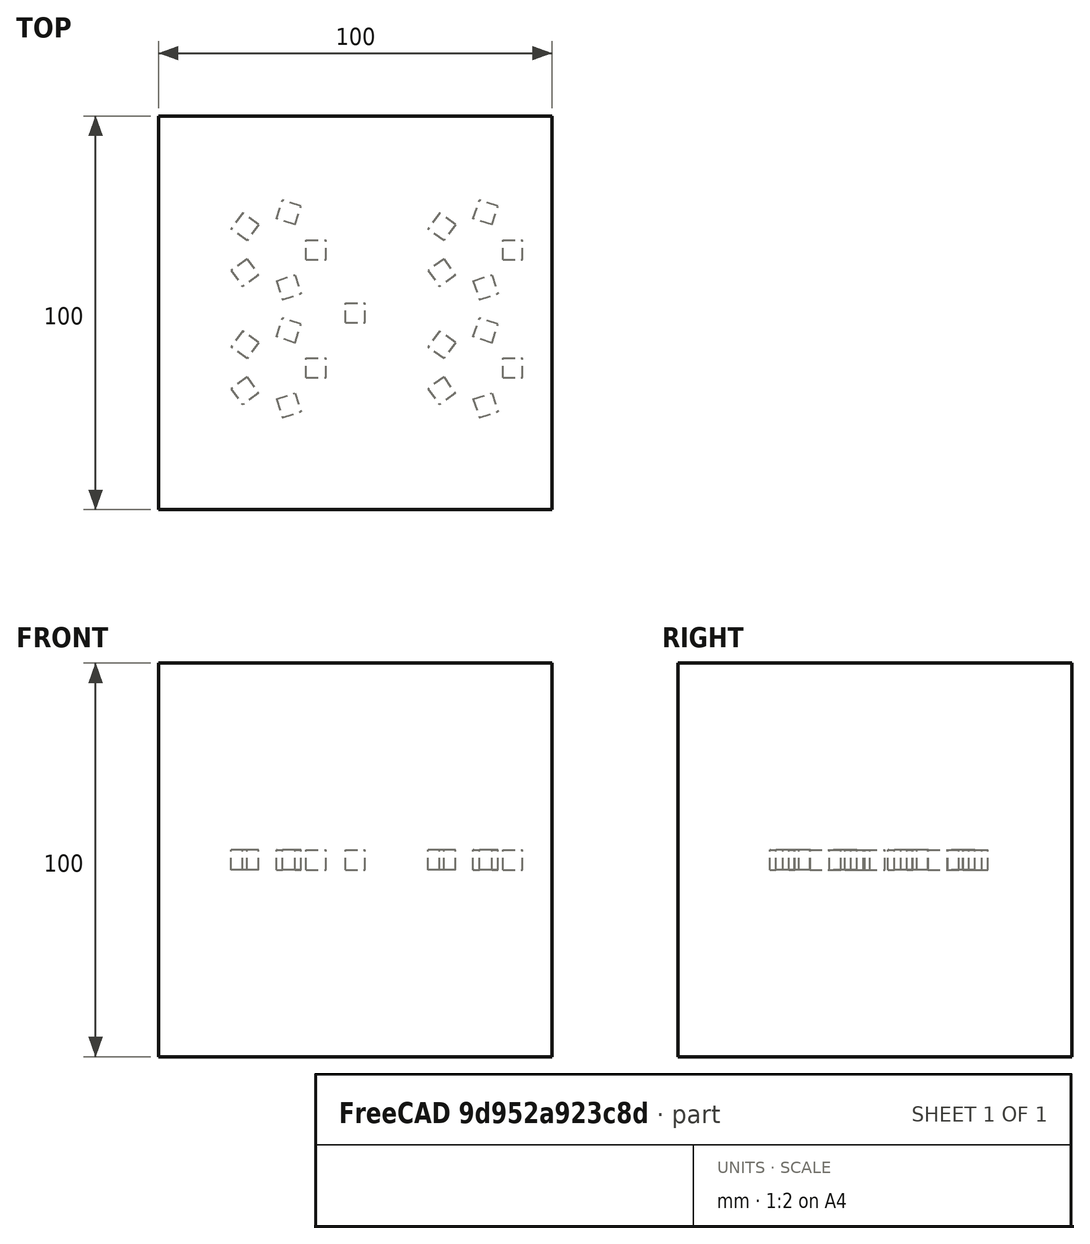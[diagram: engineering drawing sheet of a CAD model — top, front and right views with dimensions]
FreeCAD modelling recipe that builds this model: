
FCSTD DOCUMENT  (FreeCAD 0.19RUnknown)
Label: arrayTest-1
License: All rights reserved
LicenseURL: http://en.wikipedia.org/wiki/All_rights_reserved
objects: App::DocumentObjectGroupPython×1248, Part::FeaturePython×4, App::Part×3
note: 4 computed .brp shape members not serialized (recipe doc carries the construction recipe); baked Part::Feature solids carry a one-line shape summary decoded from their .brp

FEATURE [App::DocumentObjectGroupPython] HALFPI  # scripted group (container) (typed FeaturePython)
  name = HALFPI
  value = pi/2.
FEATURE [App::DocumentObjectGroupPython] PI  # scripted group (container) (typed FeaturePython)
  name = PI
  value = 1.*pi
FEATURE [App::DocumentObjectGroupPython] TWOPI  # scripted group (container) (typed FeaturePython)
  name = TWOPI
  value = 2.*pi
FEATURE [App::DocumentObjectGroupPython] Constants  # scripted group (container) (typed FeaturePython)
  Group = -> [HALFPI,PI,TWOPI]
FEATURE [App::DocumentObjectGroupPython] Variables  # scripted group (container) (typed FeaturePython)
FEATURE [App::DocumentObjectGroupPython] Quantities  # scripted group (container) (typed FeaturePython)
FEATURE [App::DocumentObjectGroupPython] Isotopes  # scripted group (container) (typed FeaturePython)
FEATURE [App::DocumentObjectGroupPython] Elements  # scripted group (container) (typed FeaturePython)
FEATURE [App::DocumentObjectGroupPython] G4Isotopes  # scripted group (container) (typed FeaturePython)
FEATURE [App::DocumentObjectGroupPython] H_element  # scripted group (container) (typed FeaturePython)
  Z = 1
  atom_value = 1.008
  formula = H
  name = H_element
FEATURE [App::DocumentObjectGroupPython] He_element  # scripted group (container) (typed FeaturePython)
  Z = 2
  atom_value = 4.0026
  formula = He
  name = He_element
FEATURE [App::DocumentObjectGroupPython] Li_element  # scripted group (container) (typed FeaturePython)
  Z = 3
  atom_value = 6.94
  formula = Li
  name = Li_element
FEATURE [App::DocumentObjectGroupPython] Be_element  # scripted group (container) (typed FeaturePython)
  Z = 4
  atom_value = 9.01218
  formula = Be
  name = Be_element
FEATURE [App::DocumentObjectGroupPython] B_element  # scripted group (container) (typed FeaturePython)
  Z = 5
  atom_value = 10.81
  formula = B
  name = B_element
FEATURE [App::DocumentObjectGroupPython] C_element  # scripted group (container) (typed FeaturePython)
  Z = 6
  atom_value = 12.011
  formula = C
  name = C_element
FEATURE [App::DocumentObjectGroupPython] N_element  # scripted group (container) (typed FeaturePython)
  Z = 7
  atom_value = 14.007
  formula = N
  name = N_element
FEATURE [App::DocumentObjectGroupPython] O_element  # scripted group (container) (typed FeaturePython)
  Z = 8
  atom_value = 15.999
  formula = O
  name = O_element
FEATURE [App::DocumentObjectGroupPython] F_element  # scripted group (container) (typed FeaturePython)
  Z = 9
  atom_value = 18.9984
  formula = F
  name = F_element
FEATURE [App::DocumentObjectGroupPython] Ne_element  # scripted group (container) (typed FeaturePython)
  Z = 10
  atom_value = 20.1797
  formula = Ne
  name = Ne_element
FEATURE [App::DocumentObjectGroupPython] Na_element  # scripted group (container) (typed FeaturePython)
  Z = 11
  atom_value = 22.9898
  formula = Na
  name = Na_element
FEATURE [App::DocumentObjectGroupPython] Mg_element  # scripted group (container) (typed FeaturePython)
  Z = 12
  atom_value = 24.305
  formula = Mg
  name = Mg_element
FEATURE [App::DocumentObjectGroupPython] Al_element  # scripted group (container) (typed FeaturePython)
  Z = 13
  atom_value = 26.9815
  formula = Al
  name = Al_element
FEATURE [App::DocumentObjectGroupPython] Si_element  # scripted group (container) (typed FeaturePython)
  Z = 14
  atom_value = 28.085
  formula = Si
  name = Si_element
FEATURE [App::DocumentObjectGroupPython] P_element  # scripted group (container) (typed FeaturePython)
  Z = 15
  atom_value = 30.9738
  formula = P
  name = P_element
FEATURE [App::DocumentObjectGroupPython] S_element  # scripted group (container) (typed FeaturePython)
  Z = 16
  atom_value = 32.06
  formula = S
  name = S_element
FEATURE [App::DocumentObjectGroupPython] Cl_element  # scripted group (container) (typed FeaturePython)
  Z = 17
  atom_value = 35.45
  formula = Cl
  name = Cl_element
FEATURE [App::DocumentObjectGroupPython] Ar_element  # scripted group (container) (typed FeaturePython)
  Z = 18
  atom_value = 39.95
  formula = Ar
  name = Ar_element
FEATURE [App::DocumentObjectGroupPython] K_element  # scripted group (container) (typed FeaturePython)
  Z = 19
  atom_value = 39.0983
  formula = K
  name = K_element
FEATURE [App::DocumentObjectGroupPython] Ca_element  # scripted group (container) (typed FeaturePython)
  Z = 20
  atom_value = 40.078
  formula = Ca
  name = Ca_element
FEATURE [App::DocumentObjectGroupPython] Sc_element  # scripted group (container) (typed FeaturePython)
  Z = 21
  atom_value = 44.9559
  formula = Sc
  name = Sc_element
FEATURE [App::DocumentObjectGroupPython] Ti_element  # scripted group (container) (typed FeaturePython)
  Z = 22
  atom_value = 47.867
  formula = Ti
  name = Ti_element
FEATURE [App::DocumentObjectGroupPython] V_element  # scripted group (container) (typed FeaturePython)
  Z = 23
  atom_value = 50.9415
  formula = V
  name = V_element
FEATURE [App::DocumentObjectGroupPython] Cr_element  # scripted group (container) (typed FeaturePython)
  Z = 24
  atom_value = 51.9961
  formula = Cr
  name = Cr_element
FEATURE [App::DocumentObjectGroupPython] Mn_element  # scripted group (container) (typed FeaturePython)
  Z = 25
  atom_value = 54.938
  formula = Mn
  name = Mn_element
FEATURE [App::DocumentObjectGroupPython] Fe_element  # scripted group (container) (typed FeaturePython)
  Z = 26
  atom_value = 55.845
  formula = Fe
  name = Fe_element
FEATURE [App::DocumentObjectGroupPython] Co_element  # scripted group (container) (typed FeaturePython)
  Z = 27
  atom_value = 58.9332
  formula = Co
  name = Co_element
FEATURE [App::DocumentObjectGroupPython] Ni_element  # scripted group (container) (typed FeaturePython)
  Z = 28
  atom_value = 58.6934
  formula = Ni
  name = Ni_element
FEATURE [App::DocumentObjectGroupPython] Cu_element  # scripted group (container) (typed FeaturePython)
  Z = 29
  atom_value = 63.546
  formula = Cu
  name = Cu_element
FEATURE [App::DocumentObjectGroupPython] Zn_element  # scripted group (container) (typed FeaturePython)
  Z = 30
  atom_value = 65.38
  formula = Zn
  name = Zn_element
FEATURE [App::DocumentObjectGroupPython] Ga_element  # scripted group (container) (typed FeaturePython)
  Z = 31
  atom_value = 69.723
  formula = Ga
  name = Ga_element
FEATURE [App::DocumentObjectGroupPython] Ge_element  # scripted group (container) (typed FeaturePython)
  Z = 32
  atom_value = 72.63
  formula = Ge
  name = Ge_element
FEATURE [App::DocumentObjectGroupPython] As_element  # scripted group (container) (typed FeaturePython)
  Z = 33
  atom_value = 74.9216
  formula = As
  name = As_element
FEATURE [App::DocumentObjectGroupPython] Se_element  # scripted group (container) (typed FeaturePython)
  Z = 34
  atom_value = 78.971
  formula = Se
  name = Se_element
FEATURE [App::DocumentObjectGroupPython] Br_element  # scripted group (container) (typed FeaturePython)
  Z = 35
  atom_value = 79.904
  formula = Br
  name = Br_element
FEATURE [App::DocumentObjectGroupPython] Kr_element  # scripted group (container) (typed FeaturePython)
  Z = 36
  atom_value = 83.798
  formula = Kr
  name = Kr_element
FEATURE [App::DocumentObjectGroupPython] Rb_element  # scripted group (container) (typed FeaturePython)
  Z = 37
  atom_value = 85.4678
  formula = Rb
  name = Rb_element
FEATURE [App::DocumentObjectGroupPython] Sr_element  # scripted group (container) (typed FeaturePython)
  Z = 38
  atom_value = 87.62
  formula = Sr
  name = Sr_element
FEATURE [App::DocumentObjectGroupPython] Y_element  # scripted group (container) (typed FeaturePython)
  Z = 39
  atom_value = 88.9058
  formula = Y
  name = Y_element
FEATURE [App::DocumentObjectGroupPython] Zr_element  # scripted group (container) (typed FeaturePython)
  Z = 40
  atom_value = 91.224
  formula = Zr
  name = Zr_element
FEATURE [App::DocumentObjectGroupPython] Nb_element  # scripted group (container) (typed FeaturePython)
  Z = 41
  atom_value = 92.9064
  formula = Nb
  name = Nb_element
FEATURE [App::DocumentObjectGroupPython] Mo_element  # scripted group (container) (typed FeaturePython)
  Z = 42
  atom_value = 95.95
  formula = Mo
  name = Mo_element
FEATURE [App::DocumentObjectGroupPython] Tc_element  # scripted group (container) (typed FeaturePython)
  Z = 43
  atom_value = 97
  formula = Tc
  name = Tc_element
FEATURE [App::DocumentObjectGroupPython] Ru_element  # scripted group (container) (typed FeaturePython)
  Z = 44
  atom_value = 101.07
  formula = Ru
  name = Ru_element
FEATURE [App::DocumentObjectGroupPython] Rh_element  # scripted group (container) (typed FeaturePython)
  Z = 45
  atom_value = 102.905
  formula = Rh
  name = Rh_element
FEATURE [App::DocumentObjectGroupPython] Pd_element  # scripted group (container) (typed FeaturePython)
  Z = 46
  atom_value = 106.42
  formula = Pd
  name = Pd_element
FEATURE [App::DocumentObjectGroupPython] Ag_element  # scripted group (container) (typed FeaturePython)
  Z = 47
  atom_value = 107.868
  formula = Ag
  name = Ag_element
FEATURE [App::DocumentObjectGroupPython] Cd_element  # scripted group (container) (typed FeaturePython)
  Z = 48
  atom_value = 112.414
  formula = Cd
  name = Cd_element
FEATURE [App::DocumentObjectGroupPython] In_element  # scripted group (container) (typed FeaturePython)
  Z = 49
  atom_value = 114.818
  formula = In
  name = In_element
FEATURE [App::DocumentObjectGroupPython] Sn_element  # scripted group (container) (typed FeaturePython)
  Z = 50
  atom_value = 118.71
  formula = Sn
  name = Sn_element
FEATURE [App::DocumentObjectGroupPython] Sb_element  # scripted group (container) (typed FeaturePython)
  Z = 51
  atom_value = 121.76
  formula = Sb
  name = Sb_element
FEATURE [App::DocumentObjectGroupPython] Te_element  # scripted group (container) (typed FeaturePython)
  Z = 52
  atom_value = 127.6
  formula = Te
  name = Te_element
FEATURE [App::DocumentObjectGroupPython] I_element  # scripted group (container) (typed FeaturePython)
  Z = 53
  atom_value = 126.904
  formula = I
  name = I_element
FEATURE [App::DocumentObjectGroupPython] Xe_element  # scripted group (container) (typed FeaturePython)
  Z = 54
  atom_value = 131.293
  formula = Xe
  name = Xe_element
FEATURE [App::DocumentObjectGroupPython] Cs_element  # scripted group (container) (typed FeaturePython)
  Z = 55
  atom_value = 132.905
  formula = Cs
  name = Cs_element
FEATURE [App::DocumentObjectGroupPython] Ba_element  # scripted group (container) (typed FeaturePython)
  Z = 56
  atom_value = 137.327
  formula = Ba
  name = Ba_element
FEATURE [App::DocumentObjectGroupPython] La_element  # scripted group (container) (typed FeaturePython)
  Z = 57
  atom_value = 138.905
  formula = La
  name = La_element
FEATURE [App::DocumentObjectGroupPython] Ce_element  # scripted group (container) (typed FeaturePython)
  Z = 58
  atom_value = 140.116
  formula = Ce
  name = Ce_element
FEATURE [App::DocumentObjectGroupPython] Pr_element  # scripted group (container) (typed FeaturePython)
  Z = 59
  atom_value = 140.908
  formula = Pr
  name = Pr_element
FEATURE [App::DocumentObjectGroupPython] Nd_element  # scripted group (container) (typed FeaturePython)
  Z = 60
  atom_value = 144.242
  formula = Nd
  name = Nd_element
FEATURE [App::DocumentObjectGroupPython] Pm_element  # scripted group (container) (typed FeaturePython)
  Z = 61
  atom_value = 145
  formula = Pm
  name = Pm_element
FEATURE [App::DocumentObjectGroupPython] Sm_element  # scripted group (container) (typed FeaturePython)
  Z = 62
  atom_value = 150.36
  formula = Sm
  name = Sm_element
FEATURE [App::DocumentObjectGroupPython] Eu_element  # scripted group (container) (typed FeaturePython)
  Z = 63
  atom_value = 151.964
  formula = Eu
  name = Eu_element
FEATURE [App::DocumentObjectGroupPython] Gd_element  # scripted group (container) (typed FeaturePython)
  Z = 64
  atom_value = 157.25
  formula = Gd
  name = Gd_element
FEATURE [App::DocumentObjectGroupPython] Tb_element  # scripted group (container) (typed FeaturePython)
  Z = 65
  atom_value = 158.925
  formula = Tb
  name = Tb_element
FEATURE [App::DocumentObjectGroupPython] Dy_element  # scripted group (container) (typed FeaturePython)
  Z = 66
  atom_value = 162.5
  formula = Dy
  name = Dy_element
FEATURE [App::DocumentObjectGroupPython] Ho_element  # scripted group (container) (typed FeaturePython)
  Z = 67
  atom_value = 164.93
  formula = Ho
  name = Ho_element
FEATURE [App::DocumentObjectGroupPython] Er_element  # scripted group (container) (typed FeaturePython)
  Z = 68
  atom_value = 167.259
  formula = Er
  name = Er_element
FEATURE [App::DocumentObjectGroupPython] Tm_element  # scripted group (container) (typed FeaturePython)
  Z = 69
  atom_value = 168.934
  formula = Tm
  name = Tm_element
FEATURE [App::DocumentObjectGroupPython] Yb_element  # scripted group (container) (typed FeaturePython)
  Z = 70
  atom_value = 173.045
  formula = Yb
  name = Yb_element
FEATURE [App::DocumentObjectGroupPython] Lu_element  # scripted group (container) (typed FeaturePython)
  Z = 71
  atom_value = 174.967
  formula = Lu
  name = Lu_element
FEATURE [App::DocumentObjectGroupPython] Hf_element  # scripted group (container) (typed FeaturePython)
  Z = 72
  atom_value = 178.49
  formula = Hf
  name = Hf_element
FEATURE [App::DocumentObjectGroupPython] Ta_element  # scripted group (container) (typed FeaturePython)
  Z = 73
  atom_value = 180.948
  formula = Ta
  name = Ta_element
FEATURE [App::DocumentObjectGroupPython] W_element  # scripted group (container) (typed FeaturePython)
  Z = 74
  atom_value = 183.84
  formula = W
  name = W_element
FEATURE [App::DocumentObjectGroupPython] Re_element  # scripted group (container) (typed FeaturePython)
  Z = 75
  atom_value = 186.207
  formula = Re
  name = Re_element
FEATURE [App::DocumentObjectGroupPython] Os_element  # scripted group (container) (typed FeaturePython)
  Z = 76
  atom_value = 190.23
  formula = Os
  name = Os_element
FEATURE [App::DocumentObjectGroupPython] Ir_element  # scripted group (container) (typed FeaturePython)
  Z = 77
  atom_value = 192.217
  formula = Ir
  name = Ir_element
FEATURE [App::DocumentObjectGroupPython] Pt_element  # scripted group (container) (typed FeaturePython)
  Z = 78
  atom_value = 195.084
  formula = Pt
  name = Pt_element
FEATURE [App::DocumentObjectGroupPython] Au_element  # scripted group (container) (typed FeaturePython)
  Z = 79
  atom_value = 196.967
  formula = Au
  name = Au_element
FEATURE [App::DocumentObjectGroupPython] Hg_element  # scripted group (container) (typed FeaturePython)
  Z = 80
  atom_value = 200.592
  formula = Hg
  name = Hg_element
FEATURE [App::DocumentObjectGroupPython] Tl_element  # scripted group (container) (typed FeaturePython)
  Z = 81
  atom_value = 204.38
  formula = Tl
  name = Tl_element
FEATURE [App::DocumentObjectGroupPython] Pb_element  # scripted group (container) (typed FeaturePython)
  Z = 82
  atom_value = 207.2
  formula = Pb
  name = Pb_element
FEATURE [App::DocumentObjectGroupPython] Bi_element  # scripted group (container) (typed FeaturePython)
  Z = 83
  atom_value = 208.98
  formula = Bi
  name = Bi_element
FEATURE [App::DocumentObjectGroupPython] Po_element  # scripted group (container) (typed FeaturePython)
  Z = 84
  atom_value = 209
  formula = Po
  name = Po_element
FEATURE [App::DocumentObjectGroupPython] At_element  # scripted group (container) (typed FeaturePython)
  Z = 85
  atom_value = 210
  formula = At
  name = At_element
FEATURE [App::DocumentObjectGroupPython] Rn_element  # scripted group (container) (typed FeaturePython)
  Z = 86
  atom_value = 222
  formula = Rn
  name = Rn_element
FEATURE [App::DocumentObjectGroupPython] Fr_element  # scripted group (container) (typed FeaturePython)
  Z = 87
  atom_value = 223
  formula = Fr
  name = Fr_element
FEATURE [App::DocumentObjectGroupPython] Ra_element  # scripted group (container) (typed FeaturePython)
  Z = 88
  atom_value = 226
  formula = Ra
  name = Ra_element
FEATURE [App::DocumentObjectGroupPython] Ac_element  # scripted group (container) (typed FeaturePython)
  Z = 89
  atom_value = 227
  formula = Ac
  name = Ac_element
FEATURE [App::DocumentObjectGroupPython] Th_element  # scripted group (container) (typed FeaturePython)
  Z = 90
  atom_value = 232.038
  formula = Th
  name = Th_element
FEATURE [App::DocumentObjectGroupPython] Pa_element  # scripted group (container) (typed FeaturePython)
  Z = 91
  atom_value = 231.036
  formula = Pa
  name = Pa_element
FEATURE [App::DocumentObjectGroupPython] U_element  # scripted group (container) (typed FeaturePython)
  Z = 92
  atom_value = 238.029
  formula = U
  name = U_element
FEATURE [App::DocumentObjectGroupPython] Np_element  # scripted group (container) (typed FeaturePython)
  Z = 93
  atom_value = 237
  formula = Np
  name = Np_element
FEATURE [App::DocumentObjectGroupPython] Pu_element  # scripted group (container) (typed FeaturePython)
  Z = 94
  atom_value = 244
  formula = Pu
  name = Pu_element
FEATURE [App::DocumentObjectGroupPython] Am_element  # scripted group (container) (typed FeaturePython)
  Z = 95
  atom_value = 243
  formula = Am
  name = Am_element
FEATURE [App::DocumentObjectGroupPython] Cm_element  # scripted group (container) (typed FeaturePython)
  Z = 96
  atom_value = 247
  formula = Cm
  name = Cm_element
FEATURE [App::DocumentObjectGroupPython] Bk_element  # scripted group (container) (typed FeaturePython)
  Z = 97
  atom_value = 247
  formula = Bk
  name = Bk_element
FEATURE [App::DocumentObjectGroupPython] Cf_element  # scripted group (container) (typed FeaturePython)
  Z = 98
  atom_value = 251
  formula = Cf
  name = Cf_element
FEATURE [App::DocumentObjectGroupPython] G4Elements  # scripted group (container) (typed FeaturePython)
  Group = -> [H_element,He_element,Li_element,Be_element,B_element,C_element,N_element,O_element,F_element,Ne_element,Na_element,Mg_element,Al_element,Si_element,P_element,S_element,Cl_element,Ar_element,K_element,Ca_element,Sc_element,Ti_element,V_element,Cr_element,Mn_element,Fe_element,Co_element,Ni_element,Cu_element,Zn_element,Ga_element,Ge_element,As_element,Se_element,Br_element,Kr_element,Rb_element,+61 more]
FEATURE [App::DocumentObjectGroupPython] H_element001  label="H_element : 0.101"  # scripted group (container) (typed FeaturePython)
  n = 0.101327
FEATURE [App::DocumentObjectGroupPython] C_element001  label="C_element : 0.775"  # scripted group (container) (typed FeaturePython)
  n = 0.7755
FEATURE [App::DocumentObjectGroupPython] N_element001  label="N_element : 0.035"  # scripted group (container) (typed FeaturePython)
  n = 0.035057
FEATURE [App::DocumentObjectGroupPython] O_element001  label="O_element : 0.052"  # scripted group (container) (typed FeaturePython)
  n = 0.0523159
FEATURE [App::DocumentObjectGroupPython] F_element001  label="F_element : 0.017"  # scripted group (container) (typed FeaturePython)
  n = 0.017422
FEATURE [App::DocumentObjectGroupPython] Ca_element001  label="Ca_element : 0.018"  # scripted group (container) (typed FeaturePython)
  n = 0.018378
FEATURE [App::DocumentObjectGroupPython] G4_A_150_TISSUE  label="G4_A-150_TISSUE"  # scripted group (container) (typed FeaturePython)
  Dunit = g/cm3
  Dvalue = 1.127
  Group = -> [H_element001,C_element001,N_element001,O_element001,F_element001,Ca_element001]
  conduct = 2
  density = 1
  expand = 3
  formula = G4_A-150_TISSUE
  name = G4_A-150_TISSUE
  specific = 4
FEATURE [App::DocumentObjectGroupPython] C_element002  label="C_element : 3"  # scripted group (container) (typed FeaturePython)
  n = 3
  ref = C_element
FEATURE [App::DocumentObjectGroupPython] H_element002  label="H_element : 6"  # scripted group (container) (typed FeaturePython)
  n = 6
  ref = H_element
FEATURE [App::DocumentObjectGroupPython] O_element002  label="O_element : 1"  # scripted group (container) (typed FeaturePython)
  n = 1
  ref = O_element
FEATURE [App::DocumentObjectGroupPython] G4_ACETONE  # scripted group (container) (typed FeaturePython)
  Dunit = g/cm3
  Dvalue = 0.7899
  Group = -> [C_element002,H_element002,O_element002]
  conduct = 2
  density = 1
  expand = 3
  formula = G4_ACETONE
  name = G4_ACETONE
  specific = 4
FEATURE [App::DocumentObjectGroupPython] C_element003  label="C_element : 2"  # scripted group (container) (typed FeaturePython)
  n = 2
  ref = C_element
FEATURE [App::DocumentObjectGroupPython] H_element003  label="H_element : 2"  # scripted group (container) (typed FeaturePython)
  n = 2
  ref = H_element
FEATURE [App::DocumentObjectGroupPython] G4_ACETYLENE  # scripted group (container) (typed FeaturePython)
  Dunit = g/cm3
  Dvalue = 0.0010967
  Group = -> [C_element003,H_element003]
  conduct = 2
  density = 1
  expand = 3
  formula = G4_ACETYLENE
  name = G4_ACETYLENE
  specific = 4
FEATURE [App::DocumentObjectGroupPython] C_element004  label="C_element : 5"  # scripted group (container) (typed FeaturePython)
  n = 5
  ref = C_element
FEATURE [App::DocumentObjectGroupPython] H_element004  label="H_element : 5"  # scripted group (container) (typed FeaturePython)
  n = 5
  ref = H_element
FEATURE [App::DocumentObjectGroupPython] N_element002  label="N_element : 5"  # scripted group (container) (typed FeaturePython)
  n = 5
  ref = N_element
FEATURE [App::DocumentObjectGroupPython] G4_ADENINE  # scripted group (container) (typed FeaturePython)
  Dunit = g/cm3
  Dvalue = 1.6
  Group = -> [C_element004,H_element004,N_element002]
  conduct = 2
  density = 1
  expand = 3
  formula = G4_ADENINE
  name = G4_ADENINE
  specific = 4
FEATURE [App::DocumentObjectGroupPython] H_element005  label="H_element : 0.114"  # scripted group (container) (typed FeaturePython)
  n = 0.114
FEATURE [App::DocumentObjectGroupPython] C_element005  label="C_element : 0.598"  # scripted group (container) (typed FeaturePython)
  n = 0.598
FEATURE [App::DocumentObjectGroupPython] N_element003  label="N_element : 0.007"  # scripted group (container) (typed FeaturePython)
  n = 0.007
FEATURE [App::DocumentObjectGroupPython] O_element003  label="O_element : 0.278"  # scripted group (container) (typed FeaturePython)
  n = 0.278
FEATURE [App::DocumentObjectGroupPython] Na_element001  label="Na_element : 0.001"  # scripted group (container) (typed FeaturePython)
  n = 0.001
FEATURE [App::DocumentObjectGroupPython] S_element001  label="S_element : 0.001"  # scripted group (container) (typed FeaturePython)
  n = 0.001
FEATURE [App::DocumentObjectGroupPython] Cl_element001  label="Cl_element : 0.001"  # scripted group (container) (typed FeaturePython)
  n = 0.001
FEATURE [App::DocumentObjectGroupPython] G4_ADIPOSE_TISSUE_ICRP  # scripted group (container) (typed FeaturePython)
  Dunit = g/cm3
  Dvalue = 0.95
  Group = -> [H_element005,C_element005,N_element003,O_element003,Na_element001,S_element001,Cl_element001]
  conduct = 2
  density = 1
  expand = 3
  formula = G4_ADIPOSE_TISSUE_ICRP
  name = G4_ADIPOSE_TISSUE_ICRP
  specific = 4
FEATURE [App::DocumentObjectGroupPython] C_element006  label="C_element : 0.000"  # scripted group (container) (typed FeaturePython)
  n = 0.000124
FEATURE [App::DocumentObjectGroupPython] N_element004  label="N_element : 0.755"  # scripted group (container) (typed FeaturePython)
  n = 0.755268
FEATURE [App::DocumentObjectGroupPython] O_element004  label="O_element : 0.232"  # scripted group (container) (typed FeaturePython)
  n = 0.231781
FEATURE [App::DocumentObjectGroupPython] Ar_element001  label="Ar_element : 0.013"  # scripted group (container) (typed FeaturePython)
  n = 0.012827
FEATURE [App::DocumentObjectGroupPython] G4_AIR  # scripted group (container) (typed FeaturePython)
  Dunit = g/cm3
  Dvalue = 0.00120479
  Group = -> [C_element006,N_element004,O_element004,Ar_element001]
  conduct = 2
  density = 1
  expand = 3
  formula = G4_AIR
  name = G4_AIR
  specific = 4
FEATURE [App::DocumentObjectGroupPython] C_element007  label="C_element : 006"  # scripted group (container) (typed FeaturePython)
  n = 3
  ref = C_element
FEATURE [App::DocumentObjectGroupPython] H_element006  label="H_element : 7"  # scripted group (container) (typed FeaturePython)
  n = 7
  ref = H_element
FEATURE [App::DocumentObjectGroupPython] N_element005  label="N_element : 1"  # scripted group (container) (typed FeaturePython)
  n = 1
  ref = N_element
FEATURE [App::DocumentObjectGroupPython] O_element005  label="O_element : 2"  # scripted group (container) (typed FeaturePython)
  n = 2
  ref = O_element
FEATURE [App::DocumentObjectGroupPython] G4_ALANINE  # scripted group (container) (typed FeaturePython)
  Dunit = g/cm3
  Dvalue = 1.42
  Group = -> [C_element007,H_element006,N_element005,O_element005]
  conduct = 2
  density = 1
  expand = 3
  formula = G4_ALANINE
  name = G4_ALANINE
  specific = 4
FEATURE [App::DocumentObjectGroupPython] Al_element001  label="Al_element : 2"  # scripted group (container) (typed FeaturePython)
  n = 2
  ref = Al_element
FEATURE [App::DocumentObjectGroupPython] O_element006  label="O_element : 3"  # scripted group (container) (typed FeaturePython)
  n = 3
  ref = O_element
FEATURE [App::DocumentObjectGroupPython] G4_ALUMINUM_OXIDE  # scripted group (container) (typed FeaturePython)
  Dunit = g/cm3
  Dvalue = 3.97
  Group = -> [Al_element001,O_element006]
  conduct = 2
  density = 1
  expand = 3
  formula = G4_ALUMINUM_OXIDE
  name = G4_ALUMINUM_OXIDE
  specific = 4
FEATURE [App::DocumentObjectGroupPython] H_element007  label="H_element : 0.106"  # scripted group (container) (typed FeaturePython)
  n = 0.10593
FEATURE [App::DocumentObjectGroupPython] C_element008  label="C_element : 0.789"  # scripted group (container) (typed FeaturePython)
  n = 0.788974
FEATURE [App::DocumentObjectGroupPython] O_element007  label="O_element : 0.105"  # scripted group (container) (typed FeaturePython)
  n = 0.105096
FEATURE [App::DocumentObjectGroupPython] G4_AMBER  # scripted group (container) (typed FeaturePython)
  Dunit = g/cm3
  Dvalue = 1.1
  Group = -> [H_element007,C_element008,O_element007]
  conduct = 2
  density = 1
  expand = 3
  formula = G4_AMBER
  name = G4_AMBER
  specific = 4
FEATURE [App::DocumentObjectGroupPython] N_element006  label="N_element : 006"  # scripted group (container) (typed FeaturePython)
  n = 1
  ref = N_element
FEATURE [App::DocumentObjectGroupPython] H_element008  label="H_element : 3"  # scripted group (container) (typed FeaturePython)
  n = 3
  ref = H_element
FEATURE [App::DocumentObjectGroupPython] G4_AMMONIA  # scripted group (container) (typed FeaturePython)
  Dunit = g/cm3
  Dvalue = 0.000826019
  Group = -> [N_element006,H_element008]
  conduct = 2
  density = 1
  expand = 3
  formula = G4_AMMONIA
  name = G4_AMMONIA
  specific = 4
FEATURE [App::DocumentObjectGroupPython] C_element009  label="C_element : 6"  # scripted group (container) (typed FeaturePython)
  n = 6
  ref = C_element
FEATURE [App::DocumentObjectGroupPython] H_element009  label="H_element : 008"  # scripted group (container) (typed FeaturePython)
  n = 7
  ref = H_element
FEATURE [App::DocumentObjectGroupPython] N_element007  label="N_element : 007"  # scripted group (container) (typed FeaturePython)
  n = 1
  ref = N_element
FEATURE [App::DocumentObjectGroupPython] G4_ANILINE  # scripted group (container) (typed FeaturePython)
  Dunit = g/cm3
  Dvalue = 1.0235
  Group = -> [C_element009,H_element009,N_element007]
  conduct = 2
  density = 1
  expand = 3
  formula = G4_ANILINE
  name = G4_ANILINE
  specific = 4
FEATURE [App::DocumentObjectGroupPython] C_element010  label="C_element : 14"  # scripted group (container) (typed FeaturePython)
  n = 14
  ref = C_element
FEATURE [App::DocumentObjectGroupPython] H_element010  label="H_element : 10"  # scripted group (container) (typed FeaturePython)
  n = 10
  ref = H_element
FEATURE [App::DocumentObjectGroupPython] G4_ANTHRACENE  # scripted group (container) (typed FeaturePython)
  Dunit = g/cm3
  Dvalue = 1.283
  Group = -> [C_element010,H_element010]
  conduct = 2
  density = 1
  expand = 3
  formula = G4_ANTHRACENE
  name = G4_ANTHRACENE
  specific = 4
FEATURE [App::DocumentObjectGroupPython] H_element011  label="H_element : 0.065"  # scripted group (container) (typed FeaturePython)
  n = 0.0654709
FEATURE [App::DocumentObjectGroupPython] C_element011  label="C_element : 0.537"  # scripted group (container) (typed FeaturePython)
  n = 0.536944
FEATURE [App::DocumentObjectGroupPython] N_element008  label="N_element : 0.021"  # scripted group (container) (typed FeaturePython)
  n = 0.0215
FEATURE [App::DocumentObjectGroupPython] O_element008  label="O_element : 0.032"  # scripted group (container) (typed FeaturePython)
  n = 0.032085
FEATURE [App::DocumentObjectGroupPython] F_element002  label="F_element : 0.167"  # scripted group (container) (typed FeaturePython)
  n = 0.167411
FEATURE [App::DocumentObjectGroupPython] Ca_element002  label="Ca_element : 0.177"  # scripted group (container) (typed FeaturePython)
  n = 0.176589
FEATURE [App::DocumentObjectGroupPython] G4_B_100_BONE  label="G4_B-100_BONE"  # scripted group (container) (typed FeaturePython)
  Dunit = g/cm3
  Dvalue = 1.45
  Group = -> [H_element011,C_element011,N_element008,O_element008,F_element002,Ca_element002]
  conduct = 2
  density = 1
  expand = 3
  formula = G4_B-100_BONE
  name = G4_B-100_BONE
  specific = 4
FEATURE [App::DocumentObjectGroupPython] H_element012  label="H_element : 0.057"  # scripted group (container) (typed FeaturePython)
  n = 0.057441
FEATURE [App::DocumentObjectGroupPython] C_element012  label="C_element : 0.790"  # scripted group (container) (typed FeaturePython)
  n = 0.774591
FEATURE [App::DocumentObjectGroupPython] O_element009  label="O_element : 0.168"  # scripted group (container) (typed FeaturePython)
  n = 0.167968
FEATURE [App::DocumentObjectGroupPython] G4_BAKELITE  # scripted group (container) (typed FeaturePython)
  Dunit = g/cm3
  Dvalue = 1.25
  Group = -> [H_element012,C_element012,O_element009]
  conduct = 2
  density = 1
  expand = 3
  formula = G4_BAKELITE
  name = G4_BAKELITE
  specific = 4
FEATURE [App::DocumentObjectGroupPython] Ba_element001  label="Ba_element : 1"  # scripted group (container) (typed FeaturePython)
  n = 1
  ref = Ba_element
FEATURE [App::DocumentObjectGroupPython] F_element003  label="F_element : 2"  # scripted group (container) (typed FeaturePython)
  n = 2
  ref = F_element
FEATURE [App::DocumentObjectGroupPython] G4_BARIUM_FLUORIDE  # scripted group (container) (typed FeaturePython)
  Dunit = g/cm3
  Dvalue = 4.89
  Group = -> [Ba_element001,F_element003]
  conduct = 2
  density = 1
  expand = 3
  formula = G4_BARIUM_FLUORIDE
  name = G4_BARIUM_FLUORIDE
  specific = 4
FEATURE [App::DocumentObjectGroupPython] Ba_element002  label="Ba_element : 002"  # scripted group (container) (typed FeaturePython)
  n = 1
  ref = Ba_element
FEATURE [App::DocumentObjectGroupPython] S_element002  label="S_element : 1"  # scripted group (container) (typed FeaturePython)
  n = 1
  ref = S_element
FEATURE [App::DocumentObjectGroupPython] O_element010  label="O_element : 4"  # scripted group (container) (typed FeaturePython)
  n = 4
  ref = O_element
FEATURE [App::DocumentObjectGroupPython] G4_BARIUM_SULFATE  # scripted group (container) (typed FeaturePython)
  Dunit = g/cm3
  Dvalue = 4.5
  Group = -> [Ba_element002,S_element002,O_element010]
  conduct = 2
  density = 1
  expand = 3
  formula = G4_BARIUM_SULFATE
  name = G4_BARIUM_SULFATE
  specific = 4
FEATURE [App::DocumentObjectGroupPython] C_element013  label="C_element : 007"  # scripted group (container) (typed FeaturePython)
  n = 6
  ref = C_element
FEATURE [App::DocumentObjectGroupPython] H_element013  label="H_element : 009"  # scripted group (container) (typed FeaturePython)
  n = 6
  ref = H_element
FEATURE [App::DocumentObjectGroupPython] G4_BENZENE  # scripted group (container) (typed FeaturePython)
  Dunit = g/cm3
  Dvalue = 0.87865
  Group = -> [C_element013,H_element013]
  conduct = 2
  density = 1
  expand = 3
  formula = G4_BENZENE
  name = G4_BENZENE
  specific = 4
FEATURE [App::DocumentObjectGroupPython] Be_element001  label="Be_element : 1"  # scripted group (container) (typed FeaturePython)
  n = 1
  ref = Be_element
FEATURE [App::DocumentObjectGroupPython] O_element011  label="O_element : 005"  # scripted group (container) (typed FeaturePython)
  n = 1
  ref = O_element
FEATURE [App::DocumentObjectGroupPython] G4_BERYLLIUM_OXIDE  # scripted group (container) (typed FeaturePython)
  Dunit = g/cm3
  Dvalue = 3.01
  Group = -> [Be_element001,O_element011]
  conduct = 2
  density = 1
  expand = 3
  formula = G4_BERYLLIUM_OXIDE
  name = G4_BERYLLIUM_OXIDE
  specific = 4
FEATURE [App::DocumentObjectGroupPython] Bi_element001  label="Bi_element : 4"  # scripted group (container) (typed FeaturePython)
  n = 4
  ref = Bi_element
FEATURE [App::DocumentObjectGroupPython] Ge_element001  label="Ge_element : 3"  # scripted group (container) (typed FeaturePython)
  n = 3
  ref = Ge_element
FEATURE [App::DocumentObjectGroupPython] O_element012  label="O_element : 12"  # scripted group (container) (typed FeaturePython)
  n = 12
  ref = O_element
FEATURE [App::DocumentObjectGroupPython] G4_BGO  # scripted group (container) (typed FeaturePython)
  Dunit = g/cm3
  Dvalue = 7.13
  Group = -> [Bi_element001,Ge_element001,O_element012]
  conduct = 2
  density = 1
  expand = 3
  formula = G4_BGO
  name = G4_BGO
  specific = 4
FEATURE [App::DocumentObjectGroupPython] H_element014  label="H_element : 0.102"  # scripted group (container) (typed FeaturePython)
  n = 0.102
FEATURE [App::DocumentObjectGroupPython] C_element014  label="C_element : 0.110"  # scripted group (container) (typed FeaturePython)
  n = 0.11
FEATURE [App::DocumentObjectGroupPython] N_element009  label="N_element : 0.033"  # scripted group (container) (typed FeaturePython)
  n = 0.033
FEATURE [App::DocumentObjectGroupPython] O_element013  label="O_element : 0.745"  # scripted group (container) (typed FeaturePython)
  n = 0.745
FEATURE [App::DocumentObjectGroupPython] Na_element002  label="Na_element : 0.002"  # scripted group (container) (typed FeaturePython)
  n = 0.001
FEATURE [App::DocumentObjectGroupPython] P_element001  label="P_element : 0.001"  # scripted group (container) (typed FeaturePython)
  n = 0.001
FEATURE [App::DocumentObjectGroupPython] S_element003  label="S_element : 0.002"  # scripted group (container) (typed FeaturePython)
  n = 0.002
FEATURE [App::DocumentObjectGroupPython] Cl_element002  label="Cl_element : 0.003"  # scripted group (container) (typed FeaturePython)
  n = 0.003
FEATURE [App::DocumentObjectGroupPython] K_element001  label="K_element : 0.002"  # scripted group (container) (typed FeaturePython)
  n = 0.002
FEATURE [App::DocumentObjectGroupPython] Fe_element001  label="Fe_element : 0.001"  # scripted group (container) (typed FeaturePython)
  n = 0.001
FEATURE [App::DocumentObjectGroupPython] G4_BLOOD_ICRP  # scripted group (container) (typed FeaturePython)
  Dunit = g/cm3
  Dvalue = 1.06
  Group = -> [H_element014,C_element014,N_element009,O_element013,Na_element002,P_element001,S_element003,Cl_element002,K_element001,Fe_element001]
  conduct = 2
  density = 1
  expand = 3
  formula = G4_BLOOD_ICRP
  name = G4_BLOOD_ICRP
  specific = 4
FEATURE [App::DocumentObjectGroupPython] H_element015  label="H_element : 0.064"  # scripted group (container) (typed FeaturePython)
  n = 0.064
FEATURE [App::DocumentObjectGroupPython] C_element015  label="C_element : 0.278"  # scripted group (container) (typed FeaturePython)
  n = 0.278
FEATURE [App::DocumentObjectGroupPython] N_element010  label="N_element : 0.027"  # scripted group (container) (typed FeaturePython)
  n = 0.027
FEATURE [App::DocumentObjectGroupPython] O_element014  label="O_element : 0.410"  # scripted group (container) (typed FeaturePython)
  n = 0.41
FEATURE [App::DocumentObjectGroupPython] Mg_element001  label="Mg_element : 0.002"  # scripted group (container) (typed FeaturePython)
  n = 0.002
FEATURE [App::DocumentObjectGroupPython] P_element002  label="P_element : 0.070"  # scripted group (container) (typed FeaturePython)
  n = 0.07
FEATURE [App::DocumentObjectGroupPython] S_element004  label="S_element : 0.003"  # scripted group (container) (typed FeaturePython)
  n = 0.002
FEATURE [App::DocumentObjectGroupPython] Ca_element003  label="Ca_element : 0.147"  # scripted group (container) (typed FeaturePython)
  n = 0.147
FEATURE [App::DocumentObjectGroupPython] G4_BONE_COMPACT_ICRU  # scripted group (container) (typed FeaturePython)
  Dunit = g/cm3
  Dvalue = 1.85
  Group = -> [H_element015,C_element015,N_element010,O_element014,Mg_element001,P_element002,S_element004,Ca_element003]
  conduct = 2
  density = 1
  expand = 3
  formula = G4_BONE_COMPACT_ICRU
  name = G4_BONE_COMPACT_ICRU
  specific = 4
FEATURE [App::DocumentObjectGroupPython] H_element016  label="H_element : 0.034"  # scripted group (container) (typed FeaturePython)
  n = 0.034
FEATURE [App::DocumentObjectGroupPython] C_element016  label="C_element : 0.155"  # scripted group (container) (typed FeaturePython)
  n = 0.155
FEATURE [App::DocumentObjectGroupPython] N_element011  label="N_element : 0.042"  # scripted group (container) (typed FeaturePython)
  n = 0.042
FEATURE [App::DocumentObjectGroupPython] O_element015  label="O_element : 0.435"  # scripted group (container) (typed FeaturePython)
  n = 0.435
FEATURE [App::DocumentObjectGroupPython] Na_element003  label="Na_element : 0.003"  # scripted group (container) (typed FeaturePython)
  n = 0.001
FEATURE [App::DocumentObjectGroupPython] Mg_element002  label="Mg_element : 0.003"  # scripted group (container) (typed FeaturePython)
  n = 0.002
FEATURE [App::DocumentObjectGroupPython] P_element003  label="P_element : 0.103"  # scripted group (container) (typed FeaturePython)
  n = 0.103
FEATURE [App::DocumentObjectGroupPython] S_element005  label="S_element : 0.004"  # scripted group (container) (typed FeaturePython)
  n = 0.003
FEATURE [App::DocumentObjectGroupPython] Ca_element004  label="Ca_element : 0.225"  # scripted group (container) (typed FeaturePython)
  n = 0.225
FEATURE [App::DocumentObjectGroupPython] G4_BONE_CORTICAL_ICRP  # scripted group (container) (typed FeaturePython)
  Dunit = g/cm3
  Dvalue = 1.92
  Group = -> [H_element016,C_element016,N_element011,O_element015,Na_element003,Mg_element002,P_element003,S_element005,Ca_element004]
  conduct = 2
  density = 1
  expand = 3
  formula = G4_BONE_CORTICAL_ICRP
  name = G4_BONE_CORTICAL_ICRP
  specific = 4
FEATURE [App::DocumentObjectGroupPython] B_element001  label="B_element : 4"  # scripted group (container) (typed FeaturePython)
  n = 4
  ref = B_element
FEATURE [App::DocumentObjectGroupPython] C_element017  label="C_element : 1"  # scripted group (container) (typed FeaturePython)
  n = 1
  ref = C_element
FEATURE [App::DocumentObjectGroupPython] G4_BORON_CARBIDE  # scripted group (container) (typed FeaturePython)
  Dunit = g/cm3
  Dvalue = 2.52
  Group = -> [B_element001,C_element017]
  conduct = 2
  density = 1
  expand = 3
  formula = G4_BORON_CARBIDE
  name = G4_BORON_CARBIDE
  specific = 4
FEATURE [App::DocumentObjectGroupPython] B_element002  label="B_element : 2"  # scripted group (container) (typed FeaturePython)
  n = 2
  ref = B_element
FEATURE [App::DocumentObjectGroupPython] O_element016  label="O_element : 006"  # scripted group (container) (typed FeaturePython)
  n = 3
  ref = O_element
FEATURE [App::DocumentObjectGroupPython] G4_BORON_OXIDE  # scripted group (container) (typed FeaturePython)
  Dunit = g/cm3
  Dvalue = 1.812
  Group = -> [B_element002,O_element016]
  conduct = 2
  density = 1
  expand = 3
  formula = G4_BORON_OXIDE
  name = G4_BORON_OXIDE
  specific = 4
FEATURE [App::DocumentObjectGroupPython] H_element017  label="H_element : 0.107"  # scripted group (container) (typed FeaturePython)
  n = 0.107
FEATURE [App::DocumentObjectGroupPython] C_element018  label="C_element : 0.145"  # scripted group (container) (typed FeaturePython)
  n = 0.145
FEATURE [App::DocumentObjectGroupPython] N_element012  label="N_element : 0.022"  # scripted group (container) (typed FeaturePython)
  n = 0.022
FEATURE [App::DocumentObjectGroupPython] O_element017  label="O_element : 0.712"  # scripted group (container) (typed FeaturePython)
  n = 0.712
FEATURE [App::DocumentObjectGroupPython] Na_element004  label="Na_element : 0.004"  # scripted group (container) (typed FeaturePython)
  n = 0.002
FEATURE [App::DocumentObjectGroupPython] P_element004  label="P_element : 0.004"  # scripted group (container) (typed FeaturePython)
  n = 0.004
FEATURE [App::DocumentObjectGroupPython] S_element006  label="S_element : 0.005"  # scripted group (container) (typed FeaturePython)
  n = 0.002
FEATURE [App::DocumentObjectGroupPython] Cl_element003  label="Cl_element : 0.004"  # scripted group (container) (typed FeaturePython)
  n = 0.003
FEATURE [App::DocumentObjectGroupPython] K_element002  label="K_element : 0.003"  # scripted group (container) (typed FeaturePython)
  n = 0.003
FEATURE [App::DocumentObjectGroupPython] G4_BRAIN_ICRP  # scripted group (container) (typed FeaturePython)
  Dunit = g/cm3
  Dvalue = 1.04
  Group = -> [H_element017,C_element018,N_element012,O_element017,Na_element004,P_element004,S_element006,Cl_element003,K_element002]
  conduct = 2
  density = 1
  expand = 3
  formula = G4_BRAIN_ICRP
  name = G4_BRAIN_ICRP
  specific = 4
FEATURE [App::DocumentObjectGroupPython] C_element019  label="C_element : 4"  # scripted group (container) (typed FeaturePython)
  n = 4
  ref = C_element
FEATURE [App::DocumentObjectGroupPython] H_element018  label="H_element : 010"  # scripted group (container) (typed FeaturePython)
  n = 10
  ref = H_element
FEATURE [App::DocumentObjectGroupPython] G4_BUTANE  # scripted group (container) (typed FeaturePython)
  Dunit = g/cm3
  Dvalue = 0.00249343
  Group = -> [C_element019,H_element018]
  conduct = 2
  density = 1
  expand = 3
  formula = G4_BUTANE
  name = G4_BUTANE
  specific = 4
FEATURE [App::DocumentObjectGroupPython] C_element020  label="C_element : 008"  # scripted group (container) (typed FeaturePython)
  n = 4
  ref = C_element
FEATURE [App::DocumentObjectGroupPython] H_element019  label="H_element : 011"  # scripted group (container) (typed FeaturePython)
  n = 10
  ref = H_element
FEATURE [App::DocumentObjectGroupPython] O_element018  label="O_element : 007"  # scripted group (container) (typed FeaturePython)
  n = 1
  ref = O_element
FEATURE [App::DocumentObjectGroupPython] G4_N_BUTYL_ALCOHOL  label="G4_N-BUTYL_ALCOHOL"  # scripted group (container) (typed FeaturePython)
  Dunit = g/cm3
  Dvalue = 0.8098
  Group = -> [C_element020,H_element019,O_element018]
  conduct = 2
  density = 1
  expand = 3
  formula = G4_N-BUTYL_ALCOHOL
  name = G4_N-BUTYL_ALCOHOL
  specific = 4
FEATURE [App::DocumentObjectGroupPython] H_element020  label="H_element : 0.025"  # scripted group (container) (typed FeaturePython)
  n = 0.02468
FEATURE [App::DocumentObjectGroupPython] C_element021  label="C_element : 0.502"  # scripted group (container) (typed FeaturePython)
  n = 0.501611
FEATURE [App::DocumentObjectGroupPython] O_element019  label="O_element : 0.005"  # scripted group (container) (typed FeaturePython)
  n = 0.004527
FEATURE [App::DocumentObjectGroupPython] F_element004  label="F_element : 0.465"  # scripted group (container) (typed FeaturePython)
  n = 0.465209
FEATURE [App::DocumentObjectGroupPython] Si_element001  label="Si_element : 0.004"  # scripted group (container) (typed FeaturePython)
  n = 0.003973
FEATURE [App::DocumentObjectGroupPython] G4_C_552  label="G4_C-552"  # scripted group (container) (typed FeaturePython)
  Dunit = g/cm3
  Dvalue = 1.76
  Group = -> [H_element020,C_element021,O_element019,F_element004,Si_element001]
  conduct = 2
  density = 1
  expand = 3
  formula = G4_C-552
  name = G4_C-552
  specific = 4
FEATURE [App::DocumentObjectGroupPython] Cd_element001  label="Cd_element : 1"  # scripted group (container) (typed FeaturePython)
  n = 1
  ref = Cd_element
FEATURE [App::DocumentObjectGroupPython] Te_element001  label="Te_element : 1"  # scripted group (container) (typed FeaturePython)
  n = 1
  ref = Te_element
FEATURE [App::DocumentObjectGroupPython] G4_CADMIUM_TELLURIDE  # scripted group (container) (typed FeaturePython)
  Dunit = g/cm3
  Dvalue = 6.2
  Group = -> [Cd_element001,Te_element001]
  conduct = 2
  density = 1
  expand = 3
  formula = G4_CADMIUM_TELLURIDE
  name = G4_CADMIUM_TELLURIDE
  specific = 4
FEATURE [App::DocumentObjectGroupPython] Cd_element002  label="Cd_element : 002"  # scripted group (container) (typed FeaturePython)
  n = 1
  ref = Cd_element
FEATURE [App::DocumentObjectGroupPython] W_element001  label="W_element : 1"  # scripted group (container) (typed FeaturePython)
  n = 1
  ref = W_element
FEATURE [App::DocumentObjectGroupPython] O_element020  label="O_element : 008"  # scripted group (container) (typed FeaturePython)
  n = 4
  ref = O_element
FEATURE [App::DocumentObjectGroupPython] G4_CADMIUM_TUNGSTATE  # scripted group (container) (typed FeaturePython)
  Dunit = g/cm3
  Dvalue = 7.9
  Group = -> [Cd_element002,W_element001,O_element020]
  conduct = 2
  density = 1
  expand = 3
  formula = G4_CADMIUM_TUNGSTATE
  name = G4_CADMIUM_TUNGSTATE
  specific = 4
FEATURE [App::DocumentObjectGroupPython] Ca_element005  label="Ca_element : 1"  # scripted group (container) (typed FeaturePython)
  n = 1
  ref = Ca_element
FEATURE [App::DocumentObjectGroupPython] C_element022  label="C_element : 009"  # scripted group (container) (typed FeaturePython)
  n = 1
  ref = C_element
FEATURE [App::DocumentObjectGroupPython] O_element021  label="O_element : 009"  # scripted group (container) (typed FeaturePython)
  n = 3
  ref = O_element
FEATURE [App::DocumentObjectGroupPython] G4_CALCIUM_CARBONATE  # scripted group (container) (typed FeaturePython)
  Dunit = g/cm3
  Dvalue = 2.8
  Group = -> [Ca_element005,C_element022,O_element021]
  conduct = 2
  density = 1
  expand = 3
  formula = G4_CALCIUM_CARBONATE
  name = G4_CALCIUM_CARBONATE
  specific = 4
FEATURE [App::DocumentObjectGroupPython] Ca_element006  label="Ca_element : 002"  # scripted group (container) (typed FeaturePython)
  n = 1
  ref = Ca_element
FEATURE [App::DocumentObjectGroupPython] F_element005  label="F_element : 003"  # scripted group (container) (typed FeaturePython)
  n = 2
  ref = F_element
FEATURE [App::DocumentObjectGroupPython] G4_CALCIUM_FLUORIDE  # scripted group (container) (typed FeaturePython)
  Dunit = g/cm3
  Dvalue = 3.18
  Group = -> [Ca_element006,F_element005]
  conduct = 2
  density = 1
  expand = 3
  formula = G4_CALCIUM_FLUORIDE
  name = G4_CALCIUM_FLUORIDE
  specific = 4
FEATURE [App::DocumentObjectGroupPython] Ca_element007  label="Ca_element : 003"  # scripted group (container) (typed FeaturePython)
  n = 1
  ref = Ca_element
FEATURE [App::DocumentObjectGroupPython] O_element022  label="O_element : 010"  # scripted group (container) (typed FeaturePython)
  n = 1
  ref = O_element
FEATURE [App::DocumentObjectGroupPython] G4_CALCIUM_OXIDE  # scripted group (container) (typed FeaturePython)
  Dunit = g/cm3
  Dvalue = 3.3
  Group = -> [Ca_element007,O_element022]
  conduct = 2
  density = 1
  expand = 3
  formula = G4_CALCIUM_OXIDE
  name = G4_CALCIUM_OXIDE
  specific = 4
FEATURE [App::DocumentObjectGroupPython] Ca_element008  label="Ca_element : 004"  # scripted group (container) (typed FeaturePython)
  n = 1
  ref = Ca_element
FEATURE [App::DocumentObjectGroupPython] S_element007  label="S_element : 002"  # scripted group (container) (typed FeaturePython)
  n = 1
  ref = S_element
FEATURE [App::DocumentObjectGroupPython] O_element023  label="O_element : 011"  # scripted group (container) (typed FeaturePython)
  n = 4
  ref = O_element
FEATURE [App::DocumentObjectGroupPython] G4_CALCIUM_SULFATE  # scripted group (container) (typed FeaturePython)
  Dunit = g/cm3
  Dvalue = 2.96
  Group = -> [Ca_element008,S_element007,O_element023]
  conduct = 2
  density = 1
  expand = 3
  formula = G4_CALCIUM_SULFATE
  name = G4_CALCIUM_SULFATE
  specific = 4
FEATURE [App::DocumentObjectGroupPython] Ca_element009  label="Ca_element : 005"  # scripted group (container) (typed FeaturePython)
  n = 1
  ref = Ca_element
FEATURE [App::DocumentObjectGroupPython] W_element002  label="W_element : 002"  # scripted group (container) (typed FeaturePython)
  n = 1
  ref = W_element
FEATURE [App::DocumentObjectGroupPython] O_element024  label="O_element : 012"  # scripted group (container) (typed FeaturePython)
  n = 4
  ref = O_element
FEATURE [App::DocumentObjectGroupPython] G4_CALCIUM_TUNGSTATE  # scripted group (container) (typed FeaturePython)
  Dunit = g/cm3
  Dvalue = 6.062
  Group = -> [Ca_element009,W_element002,O_element024]
  conduct = 2
  density = 1
  expand = 3
  formula = G4_CALCIUM_TUNGSTATE
  name = G4_CALCIUM_TUNGSTATE
  specific = 4
FEATURE [App::DocumentObjectGroupPython] C_element023  label="C_element : 010"  # scripted group (container) (typed FeaturePython)
  n = 1
  ref = C_element
FEATURE [App::DocumentObjectGroupPython] O_element025  label="O_element : 013"  # scripted group (container) (typed FeaturePython)
  n = 2
  ref = O_element
FEATURE [App::DocumentObjectGroupPython] G4_CARBON_DIOXIDE  # scripted group (container) (typed FeaturePython)
  Dunit = g/cm3
  Dvalue = 0.00184212
  Group = -> [C_element023,O_element025]
  conduct = 2
  density = 1
  expand = 3
  formula = G4_CARBON_DIOXIDE
  name = G4_CARBON_DIOXIDE
  specific = 4
FEATURE [App::DocumentObjectGroupPython] C_element024  label="C_element : 011"  # scripted group (container) (typed FeaturePython)
  n = 1
  ref = C_element
FEATURE [App::DocumentObjectGroupPython] Cl_element004  label="Cl_element : 4"  # scripted group (container) (typed FeaturePython)
  n = 4
  ref = Cl_element
FEATURE [App::DocumentObjectGroupPython] G4_CARBON_TETRACHLORIDE  # scripted group (container) (typed FeaturePython)
  Dunit = g/cm3
  Dvalue = 1.594
  Group = -> [C_element024,Cl_element004]
  conduct = 2
  density = 1
  expand = 3
  formula = G4_CARBON_TETRACHLORIDE
  name = G4_CARBON_TETRACHLORIDE
  specific = 4
FEATURE [App::DocumentObjectGroupPython] C_element025  label="C_element : 012"  # scripted group (container) (typed FeaturePython)
  n = 6
  ref = C_element
FEATURE [App::DocumentObjectGroupPython] H_element021  label="H_element : 012"  # scripted group (container) (typed FeaturePython)
  n = 10
  ref = H_element
FEATURE [App::DocumentObjectGroupPython] O_element026  label="O_element : 5"  # scripted group (container) (typed FeaturePython)
  n = 5
  ref = O_element
FEATURE [App::DocumentObjectGroupPython] G4_CELLULOSE_CELLOPHANE  # scripted group (container) (typed FeaturePython)
  Dunit = g/cm3
  Dvalue = 1.42
  Group = -> [C_element025,H_element021,O_element026]
  conduct = 2
  density = 1
  expand = 3
  formula = G4_CELLULOSE_CELLOPHANE
  name = G4_CELLULOSE_CELLOPHANE
  specific = 4
FEATURE [App::DocumentObjectGroupPython] H_element022  label="H_element : 0.067"  # scripted group (container) (typed FeaturePython)
  n = 0.067125
FEATURE [App::DocumentObjectGroupPython] C_element026  label="C_element : 0.545"  # scripted group (container) (typed FeaturePython)
  n = 0.545403
FEATURE [App::DocumentObjectGroupPython] O_element027  label="O_element : 0.387"  # scripted group (container) (typed FeaturePython)
  n = 0.387472
FEATURE [App::DocumentObjectGroupPython] G4_CELLULOSE_BUTYRATE  # scripted group (container) (typed FeaturePython)
  Dunit = g/cm3
  Dvalue = 1.2
  Group = -> [H_element022,C_element026,O_element027]
  conduct = 2
  density = 1
  expand = 3
  formula = G4_CELLULOSE_BUTYRATE
  name = G4_CELLULOSE_BUTYRATE
  specific = 4
FEATURE [App::DocumentObjectGroupPython] H_element023  label="H_element : 0.029"  # scripted group (container) (typed FeaturePython)
  n = 0.029216
FEATURE [App::DocumentObjectGroupPython] C_element027  label="C_element : 0.271"  # scripted group (container) (typed FeaturePython)
  n = 0.271296
FEATURE [App::DocumentObjectGroupPython] N_element013  label="N_element : 0.121"  # scripted group (container) (typed FeaturePython)
  n = 0.121276
FEATURE [App::DocumentObjectGroupPython] O_element028  label="O_element : 0.578"  # scripted group (container) (typed FeaturePython)
  n = 0.578212
FEATURE [App::DocumentObjectGroupPython] G4_CELLULOSE_NITRATE  # scripted group (container) (typed FeaturePython)
  Dunit = g/cm3
  Dvalue = 1.49
  Group = -> [H_element023,C_element027,N_element013,O_element028]
  conduct = 2
  density = 1
  expand = 3
  formula = G4_CELLULOSE_NITRATE
  name = G4_CELLULOSE_NITRATE
  specific = 4
FEATURE [App::DocumentObjectGroupPython] H_element024  label="H_element : 0.108"  # scripted group (container) (typed FeaturePython)
  n = 0.107596
FEATURE [App::DocumentObjectGroupPython] N_element014  label="N_element : 0.001"  # scripted group (container) (typed FeaturePython)
  n = 0.0008
FEATURE [App::DocumentObjectGroupPython] O_element029  label="O_element : 0.875"  # scripted group (container) (typed FeaturePython)
  n = 0.874976
FEATURE [App::DocumentObjectGroupPython] S_element008  label="S_element : 0.015"  # scripted group (container) (typed FeaturePython)
  n = 0.014627
FEATURE [App::DocumentObjectGroupPython] Ce_element001  label="Ce_element : 0.002"  # scripted group (container) (typed FeaturePython)
  n = 0.002001
FEATURE [App::DocumentObjectGroupPython] G4_CERIC_SULFATE  # scripted group (container) (typed FeaturePython)
  Dunit = g/cm3
  Dvalue = 1.03
  Group = -> [H_element024,N_element014,O_element029,S_element008,Ce_element001]
  conduct = 2
  density = 1
  expand = 3
  formula = G4_CERIC_SULFATE
  name = G4_CERIC_SULFATE
  specific = 4
FEATURE [App::DocumentObjectGroupPython] Cs_element001  label="Cs_element : 1"  # scripted group (container) (typed FeaturePython)
  n = 1
  ref = Cs_element
FEATURE [App::DocumentObjectGroupPython] F_element006  label="F_element : 1"  # scripted group (container) (typed FeaturePython)
  n = 1
  ref = F_element
FEATURE [App::DocumentObjectGroupPython] G4_CESIUM_FLUORIDE  # scripted group (container) (typed FeaturePython)
  Dunit = g/cm3
  Dvalue = 4.115
  Group = -> [Cs_element001,F_element006]
  conduct = 2
  density = 1
  expand = 3
  formula = G4_CESIUM_FLUORIDE
  name = G4_CESIUM_FLUORIDE
  specific = 4
FEATURE [App::DocumentObjectGroupPython] Cs_element002  label="Cs_element : 002"  # scripted group (container) (typed FeaturePython)
  n = 1
  ref = Cs_element
FEATURE [App::DocumentObjectGroupPython] I_element001  label="I_element : 1"  # scripted group (container) (typed FeaturePython)
  n = 1
  ref = I_element
FEATURE [App::DocumentObjectGroupPython] G4_CESIUM_IODIDE  # scripted group (container) (typed FeaturePython)
  Dunit = g/cm3
  Dvalue = 4.51
  Group = -> [Cs_element002,I_element001]
  conduct = 2
  density = 1
  expand = 3
  formula = G4_CESIUM_IODIDE
  name = G4_CESIUM_IODIDE
  specific = 4
FEATURE [App::DocumentObjectGroupPython] C_element028  label="C_element : 013"  # scripted group (container) (typed FeaturePython)
  n = 6
  ref = C_element
FEATURE [App::DocumentObjectGroupPython] H_element025  label="H_element : 013"  # scripted group (container) (typed FeaturePython)
  n = 5
  ref = H_element
FEATURE [App::DocumentObjectGroupPython] Cl_element005  label="Cl_element : 1"  # scripted group (container) (typed FeaturePython)
  n = 1
  ref = Cl_element
FEATURE [App::DocumentObjectGroupPython] G4_CHLOROBENZENE  # scripted group (container) (typed FeaturePython)
  Dunit = g/cm3
  Dvalue = 1.1058
  Group = -> [C_element028,H_element025,Cl_element005]
  conduct = 2
  density = 1
  expand = 3
  formula = G4_CHLOROBENZENE
  name = G4_CHLOROBENZENE
  specific = 4
FEATURE [App::DocumentObjectGroupPython] C_element029  label="C_element : 014"  # scripted group (container) (typed FeaturePython)
  n = 1
  ref = C_element
FEATURE [App::DocumentObjectGroupPython] H_element026  label="H_element : 1"  # scripted group (container) (typed FeaturePython)
  n = 1
  ref = H_element
FEATURE [App::DocumentObjectGroupPython] Cl_element006  label="Cl_element : 3"  # scripted group (container) (typed FeaturePython)
  n = 3
  ref = Cl_element
FEATURE [App::DocumentObjectGroupPython] G4_CHLOROFORM  # scripted group (container) (typed FeaturePython)
  Dunit = g/cm3
  Dvalue = 1.4832
  Group = -> [C_element029,H_element026,Cl_element006]
  conduct = 2
  density = 1
  expand = 3
  formula = G4_CHLOROFORM
  name = G4_CHLOROFORM
  specific = 4
FEATURE [App::DocumentObjectGroupPython] H_element027  label="H_element : 0.010"  # scripted group (container) (typed FeaturePython)
  n = 0.01
FEATURE [App::DocumentObjectGroupPython] C_element030  label="C_element : 0.001"  # scripted group (container) (typed FeaturePython)
  n = 0.001
FEATURE [App::DocumentObjectGroupPython] O_element030  label="O_element : 0.529"  # scripted group (container) (typed FeaturePython)
  n = 0.529107
FEATURE [App::DocumentObjectGroupPython] Na_element005  label="Na_element : 0.016"  # scripted group (container) (typed FeaturePython)
  n = 0.016
FEATURE [App::DocumentObjectGroupPython] Mg_element003  label="Mg_element : 0.004"  # scripted group (container) (typed FeaturePython)
  n = 0.002
FEATURE [App::DocumentObjectGroupPython] Al_element002  label="Al_element : 0.034"  # scripted group (container) (typed FeaturePython)
  n = 0.033872
FEATURE [App::DocumentObjectGroupPython] Si_element002  label="Si_element : 0.337"  # scripted group (container) (typed FeaturePython)
  n = 0.337021
FEATURE [App::DocumentObjectGroupPython] K_element003  label="K_element : 0.013"  # scripted group (container) (typed FeaturePython)
  n = 0.013
FEATURE [App::DocumentObjectGroupPython] Ca_element010  label="Ca_element : 0.044"  # scripted group (container) (typed FeaturePython)
  n = 0.044
FEATURE [App::DocumentObjectGroupPython] Fe_element002  label="Fe_element : 0.014"  # scripted group (container) (typed FeaturePython)
  n = 0.014
FEATURE [App::DocumentObjectGroupPython] G4_CONCRETE  # scripted group (container) (typed FeaturePython)
  Dunit = g/cm3
  Dvalue = 2.3
  Group = -> [H_element027,C_element030,O_element030,Na_element005,Mg_element003,Al_element002,Si_element002,K_element003,Ca_element010,Fe_element002]
  conduct = 2
  density = 1
  expand = 3
  formula = G4_CONCRETE
  name = G4_CONCRETE
  specific = 4
FEATURE [App::DocumentObjectGroupPython] C_element031  label="C_element : 015"  # scripted group (container) (typed FeaturePython)
  n = 6
  ref = C_element
FEATURE [App::DocumentObjectGroupPython] H_element028  label="H_element : 12"  # scripted group (container) (typed FeaturePython)
  n = 12
  ref = H_element
FEATURE [App::DocumentObjectGroupPython] G4_CYCLOHEXANE  # scripted group (container) (typed FeaturePython)
  Dunit = g/cm3
  Dvalue = 0.779
  Group = -> [C_element031,H_element028]
  conduct = 2
  density = 1
  expand = 3
  formula = G4_CYCLOHEXANE
  name = G4_CYCLOHEXANE
  specific = 4
FEATURE [App::DocumentObjectGroupPython] C_element032  label="C_element : 016"  # scripted group (container) (typed FeaturePython)
  n = 6
  ref = C_element
FEATURE [App::DocumentObjectGroupPython] H_element029  label="H_element : 4"  # scripted group (container) (typed FeaturePython)
  n = 4
  ref = H_element
FEATURE [App::DocumentObjectGroupPython] Cl_element007  label="Cl_element : 2"  # scripted group (container) (typed FeaturePython)
  n = 2
  ref = Cl_element
FEATURE [App::DocumentObjectGroupPython] G4_1_2_DICHLOROBENZENE  label="G4_1.2-DICHLOROBENZENE"  # scripted group (container) (typed FeaturePython)
  Dunit = g/cm3
  Dvalue = 1.3048
  Group = -> [C_element032,H_element029,Cl_element007]
  conduct = 2
  density = 1
  expand = 3
  formula = G4_1.2-DICHLOROBENZENE
  name = G4_1.2-DICHLOROBENZENE
  specific = 4
FEATURE [App::DocumentObjectGroupPython] C_element033  label="C_element : 017"  # scripted group (container) (typed FeaturePython)
  n = 4
  ref = C_element
FEATURE [App::DocumentObjectGroupPython] H_element030  label="H_element : 8"  # scripted group (container) (typed FeaturePython)
  n = 8
  ref = H_element
FEATURE [App::DocumentObjectGroupPython] O_element031  label="O_element : 014"  # scripted group (container) (typed FeaturePython)
  n = 1
  ref = O_element
FEATURE [App::DocumentObjectGroupPython] Cl_element008  label="Cl_element : 005"  # scripted group (container) (typed FeaturePython)
  n = 2
  ref = Cl_element
FEATURE [App::DocumentObjectGroupPython] G4_DICHLORODIETHYL_ETHER  # scripted group (container) (typed FeaturePython)
  Dunit = g/cm3
  Dvalue = 1.2199
  Group = -> [C_element033,H_element030,O_element031,Cl_element008]
  conduct = 2
  density = 1
  expand = 3
  formula = G4_DICHLORODIETHYL_ETHER
  name = G4_DICHLORODIETHYL_ETHER
  specific = 4
FEATURE [App::DocumentObjectGroupPython] C_element034  label="C_element : 018"  # scripted group (container) (typed FeaturePython)
  n = 2
  ref = C_element
FEATURE [App::DocumentObjectGroupPython] H_element031  label="H_element : 014"  # scripted group (container) (typed FeaturePython)
  n = 4
  ref = H_element
FEATURE [App::DocumentObjectGroupPython] Cl_element009  label="Cl_element : 006"  # scripted group (container) (typed FeaturePython)
  n = 2
  ref = Cl_element
FEATURE [App::DocumentObjectGroupPython] G4_1_2_DICHLOROETHANE  label="G4_1.2-DICHLOROETHANE"  # scripted group (container) (typed FeaturePython)
  Dunit = g/cm3
  Dvalue = 1.2351
  Group = -> [C_element034,H_element031,Cl_element009]
  conduct = 2
  density = 1
  expand = 3
  formula = G4_1.2-DICHLOROETHANE
  name = G4_1.2-DICHLOROETHANE
  specific = 4
FEATURE [App::DocumentObjectGroupPython] C_element035  label="C_element : 019"  # scripted group (container) (typed FeaturePython)
  n = 4
  ref = C_element
FEATURE [App::DocumentObjectGroupPython] H_element032  label="H_element : 015"  # scripted group (container) (typed FeaturePython)
  n = 10
  ref = H_element
FEATURE [App::DocumentObjectGroupPython] O_element032  label="O_element : 015"  # scripted group (container) (typed FeaturePython)
  n = 1
  ref = O_element
FEATURE [App::DocumentObjectGroupPython] G4_DIETHYL_ETHER  # scripted group (container) (typed FeaturePython)
  Dunit = g/cm3
  Dvalue = 0.71378
  Group = -> [C_element035,H_element032,O_element032]
  conduct = 2
  density = 1
  expand = 3
  formula = G4_DIETHYL_ETHER
  name = G4_DIETHYL_ETHER
  specific = 4
FEATURE [App::DocumentObjectGroupPython] C_element036  label="C_element : 020"  # scripted group (container) (typed FeaturePython)
  n = 3
  ref = C_element
FEATURE [App::DocumentObjectGroupPython] H_element033  label="H_element : 016"  # scripted group (container) (typed FeaturePython)
  n = 7
  ref = H_element
FEATURE [App::DocumentObjectGroupPython] N_element015  label="N_element : 008"  # scripted group (container) (typed FeaturePython)
  n = 1
  ref = N_element
FEATURE [App::DocumentObjectGroupPython] O_element033  label="O_element : 016"  # scripted group (container) (typed FeaturePython)
  n = 1
  ref = O_element
FEATURE [App::DocumentObjectGroupPython] G4_N_N_DIMETHYL_FORMAMIDE  label="G4_N.N-DIMETHYL_FORMAMIDE"  # scripted group (container) (typed FeaturePython)
  Dunit = g/cm3
  Dvalue = 0.9487
  Group = -> [C_element036,H_element033,N_element015,O_element033]
  conduct = 2
  density = 1
  expand = 3
  formula = G4_N.N-DIMETHYL_FORMAMIDE
  name = G4_N.N-DIMETHYL_FORMAMIDE
  specific = 4
FEATURE [App::DocumentObjectGroupPython] C_element037  label="C_element : 021"  # scripted group (container) (typed FeaturePython)
  n = 2
  ref = C_element
FEATURE [App::DocumentObjectGroupPython] H_element034  label="H_element : 017"  # scripted group (container) (typed FeaturePython)
  n = 6
  ref = H_element
FEATURE [App::DocumentObjectGroupPython] O_element034  label="O_element : 017"  # scripted group (container) (typed FeaturePython)
  n = 1
  ref = O_element
FEATURE [App::DocumentObjectGroupPython] S_element009  label="S_element : 003"  # scripted group (container) (typed FeaturePython)
  n = 1
  ref = S_element
FEATURE [App::DocumentObjectGroupPython] G4_DIMETHYL_SULFOXIDE  # scripted group (container) (typed FeaturePython)
  Dunit = g/cm3
  Dvalue = 1.1014
  Group = -> [C_element037,H_element034,O_element034,S_element009]
  conduct = 2
  density = 1
  expand = 3
  formula = G4_DIMETHYL_SULFOXIDE
  name = G4_DIMETHYL_SULFOXIDE
  specific = 4
FEATURE [App::DocumentObjectGroupPython] C_element038  label="C_element : 022"  # scripted group (container) (typed FeaturePython)
  n = 2
  ref = C_element
FEATURE [App::DocumentObjectGroupPython] H_element035  label="H_element : 018"  # scripted group (container) (typed FeaturePython)
  n = 6
  ref = H_element
FEATURE [App::DocumentObjectGroupPython] G4_ETHANE  # scripted group (container) (typed FeaturePython)
  Dunit = g/cm3
  Dvalue = 0.00125324
  Group = -> [C_element038,H_element035]
  conduct = 2
  density = 1
  expand = 3
  formula = G4_ETHANE
  name = G4_ETHANE
  specific = 4
FEATURE [App::DocumentObjectGroupPython] C_element039  label="C_element : 023"  # scripted group (container) (typed FeaturePython)
  n = 2
  ref = C_element
FEATURE [App::DocumentObjectGroupPython] H_element036  label="H_element : 019"  # scripted group (container) (typed FeaturePython)
  n = 6
  ref = H_element
FEATURE [App::DocumentObjectGroupPython] O_element035  label="O_element : 018"  # scripted group (container) (typed FeaturePython)
  n = 1
  ref = O_element
FEATURE [App::DocumentObjectGroupPython] G4_ETHYL_ALCOHOL  # scripted group (container) (typed FeaturePython)
  Dunit = g/cm3
  Dvalue = 0.7893
  Group = -> [C_element039,H_element036,O_element035]
  conduct = 2
  density = 1
  expand = 3
  formula = G4_ETHYL_ALCOHOL
  name = G4_ETHYL_ALCOHOL
  specific = 4
FEATURE [App::DocumentObjectGroupPython] H_element037  label="H_element : 0.090"  # scripted group (container) (typed FeaturePython)
  n = 0.090027
FEATURE [App::DocumentObjectGroupPython] C_element040  label="C_element : 0.585"  # scripted group (container) (typed FeaturePython)
  n = 0.585182
FEATURE [App::DocumentObjectGroupPython] O_element036  label="O_element : 0.325"  # scripted group (container) (typed FeaturePython)
  n = 0.324791
FEATURE [App::DocumentObjectGroupPython] G4_ETHYL_CELLULOSE  # scripted group (container) (typed FeaturePython)
  Dunit = g/cm3
  Dvalue = 1.13
  Group = -> [H_element037,C_element040,O_element036]
  conduct = 2
  density = 1
  expand = 3
  formula = G4_ETHYL_CELLULOSE
  name = G4_ETHYL_CELLULOSE
  specific = 4
FEATURE [App::DocumentObjectGroupPython] C_element041  label="C_element : 024"  # scripted group (container) (typed FeaturePython)
  n = 2
  ref = C_element
FEATURE [App::DocumentObjectGroupPython] H_element038  label="H_element : 020"  # scripted group (container) (typed FeaturePython)
  n = 4
  ref = H_element
FEATURE [App::DocumentObjectGroupPython] G4_ETHYLENE  # scripted group (container) (typed FeaturePython)
  Dunit = g/cm3
  Dvalue = 0.00117497
  Group = -> [C_element041,H_element038]
  conduct = 2
  density = 1
  expand = 3
  formula = G4_ETHYLENE
  name = G4_ETHYLENE
  specific = 4
FEATURE [App::DocumentObjectGroupPython] H_element039  label="H_element : 0.096"  # scripted group (container) (typed FeaturePython)
  n = 0.096
FEATURE [App::DocumentObjectGroupPython] C_element042  label="C_element : 0.195"  # scripted group (container) (typed FeaturePython)
  n = 0.195
FEATURE [App::DocumentObjectGroupPython] N_element016  label="N_element : 0.057"  # scripted group (container) (typed FeaturePython)
  n = 0.057
FEATURE [App::DocumentObjectGroupPython] O_element037  label="O_element : 0.646"  # scripted group (container) (typed FeaturePython)
  n = 0.646
FEATURE [App::DocumentObjectGroupPython] Na_element006  label="Na_element : 0.017"  # scripted group (container) (typed FeaturePython)
  n = 0.001
FEATURE [App::DocumentObjectGroupPython] P_element005  label="P_element : 0.104"  # scripted group (container) (typed FeaturePython)
  n = 0.001
FEATURE [App::DocumentObjectGroupPython] S_element010  label="S_element : 0.016"  # scripted group (container) (typed FeaturePython)
  n = 0.003
FEATURE [App::DocumentObjectGroupPython] Cl_element010  label="Cl_element : 0.005"  # scripted group (container) (typed FeaturePython)
  n = 0.001
FEATURE [App::DocumentObjectGroupPython] G4_EYE_LENS_ICRP  # scripted group (container) (typed FeaturePython)
  Dunit = g/cm3
  Dvalue = 1.07
  Group = -> [H_element039,C_element042,N_element016,O_element037,Na_element006,P_element005,S_element010,Cl_element010]
  conduct = 2
  density = 1
  expand = 3
  formula = G4_EYE_LENS_ICRP
  name = G4_EYE_LENS_ICRP
  specific = 4
FEATURE [App::DocumentObjectGroupPython] Fe_element003  label="Fe_element : 2"  # scripted group (container) (typed FeaturePython)
  n = 2
  ref = Fe_element
FEATURE [App::DocumentObjectGroupPython] O_element038  label="O_element : 019"  # scripted group (container) (typed FeaturePython)
  n = 3
  ref = O_element
FEATURE [App::DocumentObjectGroupPython] G4_FERRIC_OXIDE  # scripted group (container) (typed FeaturePython)
  Dunit = g/cm3
  Dvalue = 5.2
  Group = -> [Fe_element003,O_element038]
  conduct = 2
  density = 1
  expand = 3
  formula = G4_FERRIC_OXIDE
  name = G4_FERRIC_OXIDE
  specific = 4
FEATURE [App::DocumentObjectGroupPython] Fe_element004  label="Fe_element : 1"  # scripted group (container) (typed FeaturePython)
  n = 1
  ref = Fe_element
FEATURE [App::DocumentObjectGroupPython] B_element003  label="B_element : 1"  # scripted group (container) (typed FeaturePython)
  n = 1
  ref = B_element
FEATURE [App::DocumentObjectGroupPython] G4_FERROBORIDE  # scripted group (container) (typed FeaturePython)
  Dunit = g/cm3
  Dvalue = 7.15
  Group = -> [Fe_element004,B_element003]
  conduct = 2
  density = 1
  expand = 3
  formula = G4_FERROBORIDE
  name = G4_FERROBORIDE
  specific = 4
FEATURE [App::DocumentObjectGroupPython] Fe_element005  label="Fe_element : 003"  # scripted group (container) (typed FeaturePython)
  n = 1
  ref = Fe_element
FEATURE [App::DocumentObjectGroupPython] O_element039  label="O_element : 020"  # scripted group (container) (typed FeaturePython)
  n = 1
  ref = O_element
FEATURE [App::DocumentObjectGroupPython] G4_FERROUS_OXIDE  # scripted group (container) (typed FeaturePython)
  Dunit = g/cm3
  Dvalue = 5.7
  Group = -> [Fe_element005,O_element039]
  conduct = 2
  density = 1
  expand = 3
  formula = G4_FERROUS_OXIDE
  name = G4_FERROUS_OXIDE
  specific = 4
FEATURE [App::DocumentObjectGroupPython] H_element040  label="H_element : 0.115"  # scripted group (container) (typed FeaturePython)
  n = 0.108259
FEATURE [App::DocumentObjectGroupPython] N_element017  label="N_element : 0.000"  # scripted group (container) (typed FeaturePython)
  n = 2.7e-05
FEATURE [App::DocumentObjectGroupPython] O_element040  label="O_element : 0.879"  # scripted group (container) (typed FeaturePython)
  n = 0.878636
FEATURE [App::DocumentObjectGroupPython] Na_element007  label="Na_element : 0.000"  # scripted group (container) (typed FeaturePython)
  n = 2.2e-05
FEATURE [App::DocumentObjectGroupPython] S_element011  label="S_element : 0.013"  # scripted group (container) (typed FeaturePython)
  n = 0.012968
FEATURE [App::DocumentObjectGroupPython] Cl_element011  label="Cl_element : 0.000"  # scripted group (container) (typed FeaturePython)
  n = 3.4e-05
FEATURE [App::DocumentObjectGroupPython] Fe_element006  label="Fe_element : 0.000"  # scripted group (container) (typed FeaturePython)
  n = 5.4e-05
FEATURE [App::DocumentObjectGroupPython] G4_FERROUS_SULFATE  # scripted group (container) (typed FeaturePython)
  Dunit = g/cm3
  Dvalue = 1.024
  Group = -> [H_element040,N_element017,O_element040,Na_element007,S_element011,Cl_element011,Fe_element006]
  conduct = 2
  density = 1
  expand = 3
  formula = G4_FERROUS_SULFATE
  name = G4_FERROUS_SULFATE
  specific = 4
FEATURE [App::DocumentObjectGroupPython] C_element043  label="C_element : 0.099"  # scripted group (container) (typed FeaturePython)
  n = 0.099335
FEATURE [App::DocumentObjectGroupPython] F_element007  label="F_element : 0.314"  # scripted group (container) (typed FeaturePython)
  n = 0.314247
FEATURE [App::DocumentObjectGroupPython] Cl_element012  label="Cl_element : 0.586"  # scripted group (container) (typed FeaturePython)
  n = 0.586418
FEATURE [App::DocumentObjectGroupPython] G4_FREON_12  label="G4_FREON-12"  # scripted group (container) (typed FeaturePython)
  Dunit = g/cm3
  Dvalue = 1.12
  Group = -> [C_element043,F_element007,Cl_element012]
  conduct = 2
  density = 1
  expand = 3
  formula = G4_FREON-12
  name = G4_FREON-12
  specific = 4
FEATURE [App::DocumentObjectGroupPython] C_element044  label="C_element : 0.057"  # scripted group (container) (typed FeaturePython)
  n = 0.057245
FEATURE [App::DocumentObjectGroupPython] F_element008  label="F_element : 0.181"  # scripted group (container) (typed FeaturePython)
  n = 0.181096
FEATURE [App::DocumentObjectGroupPython] Br_element001  label="Br_element : 0.762"  # scripted group (container) (typed FeaturePython)
  n = 0.761659
FEATURE [App::DocumentObjectGroupPython] G4_FREON_12B2  label="G4_FREON-12B2"  # scripted group (container) (typed FeaturePython)
  Dunit = g/cm3
  Dvalue = 1.8
  Group = -> [C_element044,F_element008,Br_element001]
  conduct = 2
  density = 1
  expand = 3
  formula = G4_FREON-12B2
  name = G4_FREON-12B2
  specific = 4
FEATURE [App::DocumentObjectGroupPython] C_element045  label="C_element : 0.115"  # scripted group (container) (typed FeaturePython)
  n = 0.114983
FEATURE [App::DocumentObjectGroupPython] F_element009  label="F_element : 0.546"  # scripted group (container) (typed FeaturePython)
  n = 0.545621
FEATURE [App::DocumentObjectGroupPython] Cl_element013  label="Cl_element : 0.339"  # scripted group (container) (typed FeaturePython)
  n = 0.339396
FEATURE [App::DocumentObjectGroupPython] G4_FREON_13  label="G4_FREON-13"  # scripted group (container) (typed FeaturePython)
  Dunit = g/cm3
  Dvalue = 0.95
  Group = -> [C_element045,F_element009,Cl_element013]
  conduct = 2
  density = 1
  expand = 3
  formula = G4_FREON-13
  name = G4_FREON-13
  specific = 4
FEATURE [App::DocumentObjectGroupPython] C_element046  label="C_element : 025"  # scripted group (container) (typed FeaturePython)
  n = 1
  ref = C_element
FEATURE [App::DocumentObjectGroupPython] F_element010  label="F_element : 3"  # scripted group (container) (typed FeaturePython)
  n = 3
  ref = F_element
FEATURE [App::DocumentObjectGroupPython] Br_element002  label="Br_element : 1"  # scripted group (container) (typed FeaturePython)
  n = 1
  ref = Br_element
FEATURE [App::DocumentObjectGroupPython] G4_FREON_13B1  label="G4_FREON-13B1"  # scripted group (container) (typed FeaturePython)
  Dunit = g/cm3
  Dvalue = 1.5
  Group = -> [C_element046,F_element010,Br_element002]
  conduct = 2
  density = 1
  expand = 3
  formula = G4_FREON-13B1
  name = G4_FREON-13B1
  specific = 4
FEATURE [App::DocumentObjectGroupPython] C_element047  label="C_element : 0.061"  # scripted group (container) (typed FeaturePython)
  n = 0.061309
FEATURE [App::DocumentObjectGroupPython] F_element011  label="F_element : 0.291"  # scripted group (container) (typed FeaturePython)
  n = 0.290924
FEATURE [App::DocumentObjectGroupPython] I_element002  label="I_element : 0.648"  # scripted group (container) (typed FeaturePython)
  n = 0.647767
FEATURE [App::DocumentObjectGroupPython] G4_FREON_13I1  label="G4_FREON-13I1"  # scripted group (container) (typed FeaturePython)
  Dunit = g/cm3
  Dvalue = 1.8
  Group = -> [C_element047,F_element011,I_element002]
  conduct = 2
  density = 1
  expand = 3
  formula = G4_FREON-13I1
  name = G4_FREON-13I1
  specific = 4
FEATURE [App::DocumentObjectGroupPython] Gd_element001  label="Gd_element : 2"  # scripted group (container) (typed FeaturePython)
  n = 2
  ref = Gd_element
FEATURE [App::DocumentObjectGroupPython] O_element041  label="O_element : 021"  # scripted group (container) (typed FeaturePython)
  n = 2
  ref = O_element
FEATURE [App::DocumentObjectGroupPython] S_element012  label="S_element : 004"  # scripted group (container) (typed FeaturePython)
  n = 1
  ref = S_element
FEATURE [App::DocumentObjectGroupPython] G4_GADOLINIUM_OXYSULFIDE  # scripted group (container) (typed FeaturePython)
  Dunit = g/cm3
  Dvalue = 7.44
  Group = -> [Gd_element001,O_element041,S_element012]
  conduct = 2
  density = 1
  expand = 3
  formula = G4_GADOLINIUM_OXYSULFIDE
  name = G4_GADOLINIUM_OXYSULFIDE
  specific = 4
FEATURE [App::DocumentObjectGroupPython] Ga_element001  label="Ga_element : 1"  # scripted group (container) (typed FeaturePython)
  n = 1
  ref = Ga_element
FEATURE [App::DocumentObjectGroupPython] As_element001  label="As_element : 1"  # scripted group (container) (typed FeaturePython)
  n = 1
  ref = As_element
FEATURE [App::DocumentObjectGroupPython] G4_GALLIUM_ARSENIDE  # scripted group (container) (typed FeaturePython)
  Dunit = g/cm3
  Dvalue = 5.31
  Group = -> [Ga_element001,As_element001]
  conduct = 2
  density = 1
  expand = 3
  formula = G4_GALLIUM_ARSENIDE
  name = G4_GALLIUM_ARSENIDE
  specific = 4
FEATURE [App::DocumentObjectGroupPython] H_element041  label="H_element : 0.081"  # scripted group (container) (typed FeaturePython)
  n = 0.08118
FEATURE [App::DocumentObjectGroupPython] C_element048  label="C_element : 0.416"  # scripted group (container) (typed FeaturePython)
  n = 0.41606
FEATURE [App::DocumentObjectGroupPython] N_element018  label="N_element : 0.111"  # scripted group (container) (typed FeaturePython)
  n = 0.11124
FEATURE [App::DocumentObjectGroupPython] O_element042  label="O_element : 0.381"  # scripted group (container) (typed FeaturePython)
  n = 0.38064
FEATURE [App::DocumentObjectGroupPython] S_element013  label="S_element : 0.011"  # scripted group (container) (typed FeaturePython)
  n = 0.01088
FEATURE [App::DocumentObjectGroupPython] G4_GEL_PHOTO_EMULSION  # scripted group (container) (typed FeaturePython)
  Dunit = g/cm3
  Dvalue = 1.2914
  Group = -> [H_element041,C_element048,N_element018,O_element042,S_element013]
  conduct = 2
  density = 1
  expand = 3
  formula = G4_GEL_PHOTO_EMULSION
  name = G4_GEL_PHOTO_EMULSION
  specific = 4
FEATURE [App::DocumentObjectGroupPython] B_element004  label="B_element : 0.040"  # scripted group (container) (typed FeaturePython)
  n = 0.0400639
FEATURE [App::DocumentObjectGroupPython] O_element043  label="O_element : 0.540"  # scripted group (container) (typed FeaturePython)
  n = 0.539561
FEATURE [App::DocumentObjectGroupPython] Na_element008  label="Na_element : 0.028"  # scripted group (container) (typed FeaturePython)
  n = 0.0281909
FEATURE [App::DocumentObjectGroupPython] Al_element003  label="Al_element : 0.012"  # scripted group (container) (typed FeaturePython)
  n = 0.011644
FEATURE [App::DocumentObjectGroupPython] Si_element003  label="Si_element : 0.377"  # scripted group (container) (typed FeaturePython)
  n = 0.377219
FEATURE [App::DocumentObjectGroupPython] K_element004  label="K_element : 0.014"  # scripted group (container) (typed FeaturePython)
  n = 0.00332099
FEATURE [App::DocumentObjectGroupPython] G4_Pyrex_Glass  # scripted group (container) (typed FeaturePython)
  Dunit = g/cm3
  Dvalue = 2.23
  Group = -> [B_element004,O_element043,Na_element008,Al_element003,Si_element003,K_element004]
  conduct = 2
  density = 1
  expand = 3
  formula = G4_Pyrex_Glass
  name = G4_Pyrex_Glass
  specific = 4
FEATURE [App::DocumentObjectGroupPython] O_element044  label="O_element : 0.156"  # scripted group (container) (typed FeaturePython)
  n = 0.156453
FEATURE [App::DocumentObjectGroupPython] Si_element004  label="Si_element : 0.081"  # scripted group (container) (typed FeaturePython)
  n = 0.080866
FEATURE [App::DocumentObjectGroupPython] Ti_element001  label="Ti_element : 0.008"  # scripted group (container) (typed FeaturePython)
  n = 0.008092
FEATURE [App::DocumentObjectGroupPython] As_element002  label="As_element : 0.003"  # scripted group (container) (typed FeaturePython)
  n = 0.002651
FEATURE [App::DocumentObjectGroupPython] Pb_element001  label="Pb_element : 0.752"  # scripted group (container) (typed FeaturePython)
  n = 0.751938
FEATURE [App::DocumentObjectGroupPython] G4_GLASS_LEAD  # scripted group (container) (typed FeaturePython)
  Dunit = g/cm3
  Dvalue = 6.22
  Group = -> [O_element044,Si_element004,Ti_element001,As_element002,Pb_element001]
  conduct = 2
  density = 1
  expand = 3
  formula = G4_GLASS_LEAD
  name = G4_GLASS_LEAD
  specific = 4
FEATURE [App::DocumentObjectGroupPython] O_element045  label="O_element : 0.460"  # scripted group (container) (typed FeaturePython)
  n = 0.4598
FEATURE [App::DocumentObjectGroupPython] Na_element009  label="Na_element : 0.096"  # scripted group (container) (typed FeaturePython)
  n = 0.0964411
FEATURE [App::DocumentObjectGroupPython] Si_element005  label="Si_element : 0.378"  # scripted group (container) (typed FeaturePython)
  n = 0.336553
FEATURE [App::DocumentObjectGroupPython] Ca_element011  label="Ca_element : 0.107"  # scripted group (container) (typed FeaturePython)
  n = 0.107205
FEATURE [App::DocumentObjectGroupPython] G4_GLASS_PLATE  # scripted group (container) (typed FeaturePython)
  Dunit = g/cm3
  Dvalue = 2.4
  Group = -> [O_element045,Na_element009,Si_element005,Ca_element011]
  conduct = 2
  density = 1
  expand = 3
  formula = G4_GLASS_PLATE
  name = G4_GLASS_PLATE
  specific = 4
FEATURE [App::DocumentObjectGroupPython] C_element049  label="C_element : 026"  # scripted group (container) (typed FeaturePython)
  n = 5
  ref = C_element
FEATURE [App::DocumentObjectGroupPython] H_element042  label="H_element : 021"  # scripted group (container) (typed FeaturePython)
  n = 10
  ref = H_element
FEATURE [App::DocumentObjectGroupPython] N_element019  label="N_element : 2"  # scripted group (container) (typed FeaturePython)
  n = 2
  ref = N_element
FEATURE [App::DocumentObjectGroupPython] O_element046  label="O_element : 022"  # scripted group (container) (typed FeaturePython)
  n = 3
  ref = O_element
FEATURE [App::DocumentObjectGroupPython] G4_GLUTAMINE  # scripted group (container) (typed FeaturePython)
  Dunit = g/cm3
  Dvalue = 1.46
  Group = -> [C_element049,H_element042,N_element019,O_element046]
  conduct = 2
  density = 1
  expand = 3
  formula = G4_GLUTAMINE
  name = G4_GLUTAMINE
  specific = 4
FEATURE [App::DocumentObjectGroupPython] C_element050  label="C_element : 027"  # scripted group (container) (typed FeaturePython)
  n = 3
  ref = C_element
FEATURE [App::DocumentObjectGroupPython] H_element043  label="H_element : 022"  # scripted group (container) (typed FeaturePython)
  n = 8
  ref = H_element
FEATURE [App::DocumentObjectGroupPython] O_element047  label="O_element : 023"  # scripted group (container) (typed FeaturePython)
  n = 3
  ref = O_element
FEATURE [App::DocumentObjectGroupPython] G4_GLYCEROL  # scripted group (container) (typed FeaturePython)
  Dunit = g/cm3
  Dvalue = 1.2613
  Group = -> [C_element050,H_element043,O_element047]
  conduct = 2
  density = 1
  expand = 3
  formula = G4_GLYCEROL
  name = G4_GLYCEROL
  specific = 4
FEATURE [App::DocumentObjectGroupPython] C_element051  label="C_element : 028"  # scripted group (container) (typed FeaturePython)
  n = 5
  ref = C_element
FEATURE [App::DocumentObjectGroupPython] H_element044  label="H_element : 023"  # scripted group (container) (typed FeaturePython)
  n = 5
  ref = H_element
FEATURE [App::DocumentObjectGroupPython] N_element020  label="N_element : 009"  # scripted group (container) (typed FeaturePython)
  n = 5
  ref = N_element
FEATURE [App::DocumentObjectGroupPython] O_element048  label="O_element : 024"  # scripted group (container) (typed FeaturePython)
  n = 1
  ref = O_element
FEATURE [App::DocumentObjectGroupPython] G4_GUANINE  # scripted group (container) (typed FeaturePython)
  Dunit = g/cm3
  Dvalue = 2.2
  Group = -> [C_element051,H_element044,N_element020,O_element048]
  conduct = 2
  density = 1
  expand = 3
  formula = G4_GUANINE
  name = G4_GUANINE
  specific = 4
FEATURE [App::DocumentObjectGroupPython] Ca_element012  label="Ca_element : 006"  # scripted group (container) (typed FeaturePython)
  n = 1
  ref = Ca_element
FEATURE [App::DocumentObjectGroupPython] S_element014  label="S_element : 005"  # scripted group (container) (typed FeaturePython)
  n = 1
  ref = S_element
FEATURE [App::DocumentObjectGroupPython] O_element049  label="O_element : 6"  # scripted group (container) (typed FeaturePython)
  n = 6
  ref = O_element
FEATURE [App::DocumentObjectGroupPython] H_element045  label="H_element : 024"  # scripted group (container) (typed FeaturePython)
  n = 4
  ref = H_element
FEATURE [App::DocumentObjectGroupPython] G4_GYPSUM  # scripted group (container) (typed FeaturePython)
  Dunit = g/cm3
  Dvalue = 2.32
  Group = -> [Ca_element012,S_element014,O_element049,H_element045]
  conduct = 2
  density = 1
  expand = 3
  formula = G4_GYPSUM
  name = G4_GYPSUM
  specific = 4
FEATURE [App::DocumentObjectGroupPython] C_element052  label="C_element : 7"  # scripted group (container) (typed FeaturePython)
  n = 7
  ref = C_element
FEATURE [App::DocumentObjectGroupPython] H_element046  label="H_element : 16"  # scripted group (container) (typed FeaturePython)
  n = 16
  ref = H_element
FEATURE [App::DocumentObjectGroupPython] G4_N_HEPTANE  label="G4_N-HEPTANE"  # scripted group (container) (typed FeaturePython)
  Dunit = g/cm3
  Dvalue = 0.68376
  Group = -> [C_element052,H_element046]
  conduct = 2
  density = 1
  expand = 3
  formula = G4_N-HEPTANE
  name = G4_N-HEPTANE
  specific = 4
FEATURE [App::DocumentObjectGroupPython] C_element053  label="C_element : 029"  # scripted group (container) (typed FeaturePython)
  n = 6
  ref = C_element
FEATURE [App::DocumentObjectGroupPython] H_element047  label="H_element : 14"  # scripted group (container) (typed FeaturePython)
  n = 14
  ref = H_element
FEATURE [App::DocumentObjectGroupPython] G4_N_HEXANE  label="G4_N-HEXANE"  # scripted group (container) (typed FeaturePython)
  Dunit = g/cm3
  Dvalue = 0.6603
  Group = -> [C_element053,H_element047]
  conduct = 2
  density = 1
  expand = 3
  formula = G4_N-HEXANE
  name = G4_N-HEXANE
  specific = 4
FEATURE [App::DocumentObjectGroupPython] C_element054  label="C_element : 22"  # scripted group (container) (typed FeaturePython)
  n = 22
  ref = C_element
FEATURE [App::DocumentObjectGroupPython] H_element048  label="H_element : 025"  # scripted group (container) (typed FeaturePython)
  n = 10
  ref = H_element
FEATURE [App::DocumentObjectGroupPython] N_element021  label="N_element : 010"  # scripted group (container) (typed FeaturePython)
  n = 2
  ref = N_element
FEATURE [App::DocumentObjectGroupPython] O_element050  label="O_element : 025"  # scripted group (container) (typed FeaturePython)
  n = 5
  ref = O_element
FEATURE [App::DocumentObjectGroupPython] G4_KAPTON  # scripted group (container) (typed FeaturePython)
  Dunit = g/cm3
  Dvalue = 1.42
  Group = -> [C_element054,H_element048,N_element021,O_element050]
  conduct = 2
  density = 1
  expand = 3
  formula = G4_KAPTON
  name = G4_KAPTON
  specific = 4
FEATURE [App::DocumentObjectGroupPython] La_element001  label="La_element : 1"  # scripted group (container) (typed FeaturePython)
  n = 1
  ref = La_element
FEATURE [App::DocumentObjectGroupPython] Br_element003  label="Br_element : 002"  # scripted group (container) (typed FeaturePython)
  n = 1
  ref = Br_element
FEATURE [App::DocumentObjectGroupPython] O_element051  label="O_element : 026"  # scripted group (container) (typed FeaturePython)
  n = 1
  ref = O_element
FEATURE [App::DocumentObjectGroupPython] G4_LANTHANUM_OXYBROMIDE  # scripted group (container) (typed FeaturePython)
  Dunit = g/cm3
  Dvalue = 6.28
  Group = -> [La_element001,Br_element003,O_element051]
  conduct = 2
  density = 1
  expand = 3
  formula = G4_LANTHANUM_OXYBROMIDE
  name = G4_LANTHANUM_OXYBROMIDE
  specific = 4
FEATURE [App::DocumentObjectGroupPython] La_element002  label="La_element : 2"  # scripted group (container) (typed FeaturePython)
  n = 2
  ref = La_element
FEATURE [App::DocumentObjectGroupPython] O_element052  label="O_element : 027"  # scripted group (container) (typed FeaturePython)
  n = 2
  ref = O_element
FEATURE [App::DocumentObjectGroupPython] S_element015  label="S_element : 006"  # scripted group (container) (typed FeaturePython)
  n = 1
  ref = S_element
FEATURE [App::DocumentObjectGroupPython] G4_LANTHANUM_OXYSULFIDE  # scripted group (container) (typed FeaturePython)
  Dunit = g/cm3
  Dvalue = 5.86
  Group = -> [La_element002,O_element052,S_element015]
  conduct = 2
  density = 1
  expand = 3
  formula = G4_LANTHANUM_OXYSULFIDE
  name = G4_LANTHANUM_OXYSULFIDE
  specific = 4
FEATURE [App::DocumentObjectGroupPython] O_element053  label="O_element : 0.072"  # scripted group (container) (typed FeaturePython)
  n = 0.071682
FEATURE [App::DocumentObjectGroupPython] Pb_element002  label="Pb_element : 0.928"  # scripted group (container) (typed FeaturePython)
  n = 0.928318
FEATURE [App::DocumentObjectGroupPython] G4_LEAD_OXIDE  # scripted group (container) (typed FeaturePython)
  Dunit = g/cm3
  Dvalue = 9.53
  Group = -> [O_element053,Pb_element002]
  conduct = 2
  density = 1
  expand = 3
  formula = G4_LEAD_OXIDE
  name = G4_LEAD_OXIDE
  specific = 4
FEATURE [App::DocumentObjectGroupPython] Li_element001  label="Li_element : 1"  # scripted group (container) (typed FeaturePython)
  n = 1
  ref = Li_element
FEATURE [App::DocumentObjectGroupPython] N_element022  label="N_element : 011"  # scripted group (container) (typed FeaturePython)
  n = 1
  ref = N_element
FEATURE [App::DocumentObjectGroupPython] H_element049  label="H_element : 026"  # scripted group (container) (typed FeaturePython)
  n = 2
  ref = H_element
FEATURE [App::DocumentObjectGroupPython] G4_LITHIUM_AMIDE  # scripted group (container) (typed FeaturePython)
  Dunit = g/cm3
  Dvalue = 1.178
  Group = -> [Li_element001,N_element022,H_element049]
  conduct = 2
  density = 1
  expand = 3
  formula = G4_LITHIUM_AMIDE
  name = G4_LITHIUM_AMIDE
  specific = 4
FEATURE [App::DocumentObjectGroupPython] Li_element002  label="Li_element : 2"  # scripted group (container) (typed FeaturePython)
  n = 2
  ref = Li_element
FEATURE [App::DocumentObjectGroupPython] C_element055  label="C_element : 030"  # scripted group (container) (typed FeaturePython)
  n = 1
  ref = C_element
FEATURE [App::DocumentObjectGroupPython] O_element054  label="O_element : 028"  # scripted group (container) (typed FeaturePython)
  n = 3
  ref = O_element
FEATURE [App::DocumentObjectGroupPython] G4_LITHIUM_CARBONATE  # scripted group (container) (typed FeaturePython)
  Dunit = g/cm3
  Dvalue = 2.11
  Group = -> [Li_element002,C_element055,O_element054]
  conduct = 2
  density = 1
  expand = 3
  formula = G4_LITHIUM_CARBONATE
  name = G4_LITHIUM_CARBONATE
  specific = 4
FEATURE [App::DocumentObjectGroupPython] Li_element003  label="Li_element : 003"  # scripted group (container) (typed FeaturePython)
  n = 1
  ref = Li_element
FEATURE [App::DocumentObjectGroupPython] F_element012  label="F_element : 004"  # scripted group (container) (typed FeaturePython)
  n = 1
  ref = F_element
FEATURE [App::DocumentObjectGroupPython] G4_LITHIUM_FLUORIDE  # scripted group (container) (typed FeaturePython)
  Dunit = g/cm3
  Dvalue = 2.635
  Group = -> [Li_element003,F_element012]
  conduct = 2
  density = 1
  expand = 3
  formula = G4_LITHIUM_FLUORIDE
  name = G4_LITHIUM_FLUORIDE
  specific = 4
FEATURE [App::DocumentObjectGroupPython] Li_element004  label="Li_element : 004"  # scripted group (container) (typed FeaturePython)
  n = 1
  ref = Li_element
FEATURE [App::DocumentObjectGroupPython] H_element050  label="H_element : 027"  # scripted group (container) (typed FeaturePython)
  n = 1
  ref = H_element
FEATURE [App::DocumentObjectGroupPython] G4_LITHIUM_HYDRIDE  # scripted group (container) (typed FeaturePython)
  Dunit = g/cm3
  Dvalue = 0.82
  Group = -> [Li_element004,H_element050]
  conduct = 2
  density = 1
  expand = 3
  formula = G4_LITHIUM_HYDRIDE
  name = G4_LITHIUM_HYDRIDE
  specific = 4
FEATURE [App::DocumentObjectGroupPython] Li_element005  label="Li_element : 005"  # scripted group (container) (typed FeaturePython)
  n = 1
  ref = Li_element
FEATURE [App::DocumentObjectGroupPython] I_element003  label="I_element : 002"  # scripted group (container) (typed FeaturePython)
  n = 1
  ref = I_element
FEATURE [App::DocumentObjectGroupPython] G4_LITHIUM_IODIDE  # scripted group (container) (typed FeaturePython)
  Dunit = g/cm3
  Dvalue = 3.494
  Group = -> [Li_element005,I_element003]
  conduct = 2
  density = 1
  expand = 3
  formula = G4_LITHIUM_IODIDE
  name = G4_LITHIUM_IODIDE
  specific = 4
FEATURE [App::DocumentObjectGroupPython] Li_element006  label="Li_element : 006"  # scripted group (container) (typed FeaturePython)
  n = 2
  ref = Li_element
FEATURE [App::DocumentObjectGroupPython] O_element055  label="O_element : 029"  # scripted group (container) (typed FeaturePython)
  n = 1
  ref = O_element
FEATURE [App::DocumentObjectGroupPython] G4_LITHIUM_OXIDE  # scripted group (container) (typed FeaturePython)
  Dunit = g/cm3
  Dvalue = 2.013
  Group = -> [Li_element006,O_element055]
  conduct = 2
  density = 1
  expand = 3
  formula = G4_LITHIUM_OXIDE
  name = G4_LITHIUM_OXIDE
  specific = 4
FEATURE [App::DocumentObjectGroupPython] Li_element007  label="Li_element : 007"  # scripted group (container) (typed FeaturePython)
  n = 2
  ref = Li_element
FEATURE [App::DocumentObjectGroupPython] B_element005  label="B_element : 005"  # scripted group (container) (typed FeaturePython)
  n = 4
  ref = B_element
FEATURE [App::DocumentObjectGroupPython] O_element056  label="O_element : 7"  # scripted group (container) (typed FeaturePython)
  n = 7
  ref = O_element
FEATURE [App::DocumentObjectGroupPython] G4_LITHIUM_TETRABORATE  # scripted group (container) (typed FeaturePython)
  Dunit = g/cm3
  Dvalue = 2.44
  Group = -> [Li_element007,B_element005,O_element056]
  conduct = 2
  density = 1
  expand = 3
  formula = G4_LITHIUM_TETRABORATE
  name = G4_LITHIUM_TETRABORATE
  specific = 4
FEATURE [App::DocumentObjectGroupPython] H_element051  label="H_element : 0.105"  # scripted group (container) (typed FeaturePython)
  n = 0.105
FEATURE [App::DocumentObjectGroupPython] C_element056  label="C_element : 0.083"  # scripted group (container) (typed FeaturePython)
  n = 0.083
FEATURE [App::DocumentObjectGroupPython] N_element023  label="N_element : 0.023"  # scripted group (container) (typed FeaturePython)
  n = 0.023
FEATURE [App::DocumentObjectGroupPython] O_element057  label="O_element : 0.779"  # scripted group (container) (typed FeaturePython)
  n = 0.779
FEATURE [App::DocumentObjectGroupPython] Na_element010  label="Na_element : 0.097"  # scripted group (container) (typed FeaturePython)
  n = 0.002
FEATURE [App::DocumentObjectGroupPython] P_element006  label="P_element : 0.105"  # scripted group (container) (typed FeaturePython)
  n = 0.001
FEATURE [App::DocumentObjectGroupPython] S_element016  label="S_element : 0.017"  # scripted group (container) (typed FeaturePython)
  n = 0.002
FEATURE [App::DocumentObjectGroupPython] Cl_element014  label="Cl_element : 0.587"  # scripted group (container) (typed FeaturePython)
  n = 0.003
FEATURE [App::DocumentObjectGroupPython] K_element005  label="K_element : 0.015"  # scripted group (container) (typed FeaturePython)
  n = 0.002
FEATURE [App::DocumentObjectGroupPython] G4_LUNG_ICRP  # scripted group (container) (typed FeaturePython)
  Dunit = g/cm3
  Dvalue = 1.04
  Group = -> [H_element051,C_element056,N_element023,O_element057,Na_element010,P_element006,S_element016,Cl_element014,K_element005]
  conduct = 2
  density = 1
  expand = 3
  formula = G4_LUNG_ICRP
  name = G4_LUNG_ICRP
  specific = 4
FEATURE [App::DocumentObjectGroupPython] H_element052  label="H_element : 0.116"  # scripted group (container) (typed FeaturePython)
  n = 0.114318
FEATURE [App::DocumentObjectGroupPython] C_element057  label="C_element : 0.656"  # scripted group (container) (typed FeaturePython)
  n = 0.655824
FEATURE [App::DocumentObjectGroupPython] O_element058  label="O_element : 0.092"  # scripted group (container) (typed FeaturePython)
  n = 0.0921831
FEATURE [App::DocumentObjectGroupPython] Mg_element004  label="Mg_element : 0.135"  # scripted group (container) (typed FeaturePython)
  n = 0.134792
FEATURE [App::DocumentObjectGroupPython] Ca_element013  label="Ca_element : 0.003"  # scripted group (container) (typed FeaturePython)
  n = 0.002883
FEATURE [App::DocumentObjectGroupPython] G4_M3_WAX  # scripted group (container) (typed FeaturePython)
  Dunit = g/cm3
  Dvalue = 1.05
  Group = -> [H_element052,C_element057,O_element058,Mg_element004,Ca_element013]
  conduct = 2
  density = 1
  expand = 3
  formula = G4_M3_WAX
  name = G4_M3_WAX
  specific = 4
FEATURE [App::DocumentObjectGroupPython] Mg_element005  label="Mg_element : 1"  # scripted group (container) (typed FeaturePython)
  n = 1
  ref = Mg_element
FEATURE [App::DocumentObjectGroupPython] C_element058  label="C_element : 031"  # scripted group (container) (typed FeaturePython)
  n = 1
  ref = C_element
FEATURE [App::DocumentObjectGroupPython] O_element059  label="O_element : 030"  # scripted group (container) (typed FeaturePython)
  n = 3
  ref = O_element
FEATURE [App::DocumentObjectGroupPython] G4_MAGNESIUM_CARBONATE  # scripted group (container) (typed FeaturePython)
  Dunit = g/cm3
  Dvalue = 2.958
  Group = -> [Mg_element005,C_element058,O_element059]
  conduct = 2
  density = 1
  expand = 3
  formula = G4_MAGNESIUM_CARBONATE
  name = G4_MAGNESIUM_CARBONATE
  specific = 4
FEATURE [App::DocumentObjectGroupPython] Mg_element006  label="Mg_element : 002"  # scripted group (container) (typed FeaturePython)
  n = 1
  ref = Mg_element
FEATURE [App::DocumentObjectGroupPython] F_element013  label="F_element : 005"  # scripted group (container) (typed FeaturePython)
  n = 2
  ref = F_element
FEATURE [App::DocumentObjectGroupPython] G4_MAGNESIUM_FLUORIDE  # scripted group (container) (typed FeaturePython)
  Dunit = g/cm3
  Dvalue = 3
  Group = -> [Mg_element006,F_element013]
  conduct = 2
  density = 1
  expand = 3
  formula = G4_MAGNESIUM_FLUORIDE
  name = G4_MAGNESIUM_FLUORIDE
  specific = 4
FEATURE [App::DocumentObjectGroupPython] Mg_element007  label="Mg_element : 003"  # scripted group (container) (typed FeaturePython)
  n = 1
  ref = Mg_element
FEATURE [App::DocumentObjectGroupPython] O_element060  label="O_element : 031"  # scripted group (container) (typed FeaturePython)
  n = 1
  ref = O_element
FEATURE [App::DocumentObjectGroupPython] G4_MAGNESIUM_OXIDE  # scripted group (container) (typed FeaturePython)
  Dunit = g/cm3
  Dvalue = 3.58
  Group = -> [Mg_element007,O_element060]
  conduct = 2
  density = 1
  expand = 3
  formula = G4_MAGNESIUM_OXIDE
  name = G4_MAGNESIUM_OXIDE
  specific = 4
FEATURE [App::DocumentObjectGroupPython] Mg_element008  label="Mg_element : 004"  # scripted group (container) (typed FeaturePython)
  n = 1
  ref = Mg_element
FEATURE [App::DocumentObjectGroupPython] B_element006  label="B_element : 006"  # scripted group (container) (typed FeaturePython)
  n = 4
  ref = B_element
FEATURE [App::DocumentObjectGroupPython] O_element061  label="O_element : 032"  # scripted group (container) (typed FeaturePython)
  n = 7
  ref = O_element
FEATURE [App::DocumentObjectGroupPython] G4_MAGNESIUM_TETRABORATE  # scripted group (container) (typed FeaturePython)
  Dunit = g/cm3
  Dvalue = 2.53
  Group = -> [Mg_element008,B_element006,O_element061]
  conduct = 2
  density = 1
  expand = 3
  formula = G4_MAGNESIUM_TETRABORATE
  name = G4_MAGNESIUM_TETRABORATE
  specific = 4
FEATURE [App::DocumentObjectGroupPython] Hg_element001  label="Hg_element : 1"  # scripted group (container) (typed FeaturePython)
  n = 1
  ref = Hg_element
FEATURE [App::DocumentObjectGroupPython] I_element004  label="I_element : 2"  # scripted group (container) (typed FeaturePython)
  n = 2
  ref = I_element
FEATURE [App::DocumentObjectGroupPython] G4_MERCURIC_IODIDE  # scripted group (container) (typed FeaturePython)
  Dunit = g/cm3
  Dvalue = 6.36
  Group = -> [Hg_element001,I_element004]
  conduct = 2
  density = 1
  expand = 3
  formula = G4_MERCURIC_IODIDE
  name = G4_MERCURIC_IODIDE
  specific = 4
FEATURE [App::DocumentObjectGroupPython] C_element059  label="C_element : 032"  # scripted group (container) (typed FeaturePython)
  n = 1
  ref = C_element
FEATURE [App::DocumentObjectGroupPython] H_element053  label="H_element : 028"  # scripted group (container) (typed FeaturePython)
  n = 4
  ref = H_element
FEATURE [App::DocumentObjectGroupPython] G4_METHANE  # scripted group (container) (typed FeaturePython)
  Dunit = g/cm3
  Dvalue = 0.000667151
  Group = -> [C_element059,H_element053]
  conduct = 2
  density = 1
  expand = 3
  formula = G4_METHANE
  name = G4_METHANE
  specific = 4
FEATURE [App::DocumentObjectGroupPython] C_element060  label="C_element : 033"  # scripted group (container) (typed FeaturePython)
  n = 1
  ref = C_element
FEATURE [App::DocumentObjectGroupPython] H_element054  label="H_element : 029"  # scripted group (container) (typed FeaturePython)
  n = 4
  ref = H_element
FEATURE [App::DocumentObjectGroupPython] O_element062  label="O_element : 033"  # scripted group (container) (typed FeaturePython)
  n = 1
  ref = O_element
FEATURE [App::DocumentObjectGroupPython] G4_METHANOL  # scripted group (container) (typed FeaturePython)
  Dunit = g/cm3
  Dvalue = 0.7914
  Group = -> [C_element060,H_element054,O_element062]
  conduct = 2
  density = 1
  expand = 3
  formula = G4_METHANOL
  name = G4_METHANOL
  specific = 4
FEATURE [App::DocumentObjectGroupPython] H_element055  label="H_element : 0.134"  # scripted group (container) (typed FeaturePython)
  n = 0.13404
FEATURE [App::DocumentObjectGroupPython] C_element061  label="C_element : 0.778"  # scripted group (container) (typed FeaturePython)
  n = 0.77796
FEATURE [App::DocumentObjectGroupPython] O_element063  label="O_element : 0.035"  # scripted group (container) (typed FeaturePython)
  n = 0.03502
FEATURE [App::DocumentObjectGroupPython] Mg_element009  label="Mg_element : 0.039"  # scripted group (container) (typed FeaturePython)
  n = 0.038594
FEATURE [App::DocumentObjectGroupPython] Ti_element002  label="Ti_element : 0.014"  # scripted group (container) (typed FeaturePython)
  n = 0.014386
FEATURE [App::DocumentObjectGroupPython] G4_MIX_D_WAX  # scripted group (container) (typed FeaturePython)
  Dunit = g/cm3
  Dvalue = 0.99
  Group = -> [H_element055,C_element061,O_element063,Mg_element009,Ti_element002]
  conduct = 2
  density = 1
  expand = 3
  formula = G4_MIX_D_WAX
  name = G4_MIX_D_WAX
  specific = 4
FEATURE [App::DocumentObjectGroupPython] H_element056  label="H_element : 0.135"  # scripted group (container) (typed FeaturePython)
  n = 0.081192
FEATURE [App::DocumentObjectGroupPython] C_element062  label="C_element : 0.583"  # scripted group (container) (typed FeaturePython)
  n = 0.583442
FEATURE [App::DocumentObjectGroupPython] N_element024  label="N_element : 0.018"  # scripted group (container) (typed FeaturePython)
  n = 0.017798
FEATURE [App::DocumentObjectGroupPython] O_element064  label="O_element : 0.186"  # scripted group (container) (typed FeaturePython)
  n = 0.186381
FEATURE [App::DocumentObjectGroupPython] Mg_element010  label="Mg_element : 0.130"  # scripted group (container) (typed FeaturePython)
  n = 0.130287
FEATURE [App::DocumentObjectGroupPython] Cl_element015  label="Cl_element : 0.588"  # scripted group (container) (typed FeaturePython)
  n = 0.0009
FEATURE [App::DocumentObjectGroupPython] G4_MS20_TISSUE  # scripted group (container) (typed FeaturePython)
  Dunit = g/cm3
  Dvalue = 1
  Group = -> [H_element056,C_element062,N_element024,O_element064,Mg_element010,Cl_element015]
  conduct = 2
  density = 1
  expand = 3
  formula = G4_MS20_TISSUE
  name = G4_MS20_TISSUE
  specific = 4
FEATURE [App::DocumentObjectGroupPython] H_element057  label="H_element : 0.136"  # scripted group (container) (typed FeaturePython)
  n = 0.102
FEATURE [App::DocumentObjectGroupPython] C_element063  label="C_element : 0.143"  # scripted group (container) (typed FeaturePython)
  n = 0.143
FEATURE [App::DocumentObjectGroupPython] N_element025  label="N_element : 0.034"  # scripted group (container) (typed FeaturePython)
  n = 0.034
FEATURE [App::DocumentObjectGroupPython] O_element065  label="O_element : 0.710"  # scripted group (container) (typed FeaturePython)
  n = 0.71
FEATURE [App::DocumentObjectGroupPython] Na_element011  label="Na_element : 0.098"  # scripted group (container) (typed FeaturePython)
  n = 0.001
FEATURE [App::DocumentObjectGroupPython] P_element007  label="P_element : 0.002"  # scripted group (container) (typed FeaturePython)
  n = 0.002
FEATURE [App::DocumentObjectGroupPython] S_element017  label="S_element : 0.018"  # scripted group (container) (typed FeaturePython)
  n = 0.003
FEATURE [App::DocumentObjectGroupPython] Cl_element016  label="Cl_element : 0.589"  # scripted group (container) (typed FeaturePython)
  n = 0.001
FEATURE [App::DocumentObjectGroupPython] K_element006  label="K_element : 0.004"  # scripted group (container) (typed FeaturePython)
  n = 0.004
FEATURE [App::DocumentObjectGroupPython] G4_MUSCLE_SKELETAL_ICRP  # scripted group (container) (typed FeaturePython)
  Dunit = g/cm3
  Dvalue = 1.05
  Group = -> [H_element057,C_element063,N_element025,O_element065,Na_element011,P_element007,S_element017,Cl_element016,K_element006]
  conduct = 2
  density = 1
  expand = 3
  formula = G4_MUSCLE_SKELETAL_ICRP
  name = G4_MUSCLE_SKELETAL_ICRP
  specific = 4
FEATURE [App::DocumentObjectGroupPython] H_element058  label="H_element : 0.137"  # scripted group (container) (typed FeaturePython)
  n = 0.102102
FEATURE [App::DocumentObjectGroupPython] C_element064  label="C_element : 0.123"  # scripted group (container) (typed FeaturePython)
  n = 0.123123
FEATURE [App::DocumentObjectGroupPython] N_element026  label="N_element : 0.756"  # scripted group (container) (typed FeaturePython)
  n = 0.035035
FEATURE [App::DocumentObjectGroupPython] O_element066  label="O_element : 0.730"  # scripted group (container) (typed FeaturePython)
  n = 0.72973
FEATURE [App::DocumentObjectGroupPython] Na_element012  label="Na_element : 0.099"  # scripted group (container) (typed FeaturePython)
  n = 0.001001
FEATURE [App::DocumentObjectGroupPython] P_element008  label="P_element : 0.106"  # scripted group (container) (typed FeaturePython)
  n = 0.002002
FEATURE [App::DocumentObjectGroupPython] S_element018  label="S_element : 0.019"  # scripted group (container) (typed FeaturePython)
  n = 0.004004
FEATURE [App::DocumentObjectGroupPython] K_element007  label="K_element : 0.016"  # scripted group (container) (typed FeaturePython)
  n = 0.003003
FEATURE [App::DocumentObjectGroupPython] G4_MUSCLE_STRIATED_ICRU  # scripted group (container) (typed FeaturePython)
  Dunit = g/cm3
  Dvalue = 1.04
  Group = -> [H_element058,C_element064,N_element026,O_element066,Na_element012,P_element008,S_element018,K_element007]
  conduct = 2
  density = 1
  expand = 3
  formula = G4_MUSCLE_STRIATED_ICRU
  name = G4_MUSCLE_STRIATED_ICRU
  specific = 4
FEATURE [App::DocumentObjectGroupPython] H_element059  label="H_element : 0.098"  # scripted group (container) (typed FeaturePython)
  n = 0.0982341
FEATURE [App::DocumentObjectGroupPython] C_element065  label="C_element : 0.156"  # scripted group (container) (typed FeaturePython)
  n = 0.156214
FEATURE [App::DocumentObjectGroupPython] N_element027  label="N_element : 0.757"  # scripted group (container) (typed FeaturePython)
  n = 0.035451
FEATURE [App::DocumentObjectGroupPython] O_element067  label="O_element : 0.880"  # scripted group (container) (typed FeaturePython)
  n = 0.710101
FEATURE [App::DocumentObjectGroupPython] G4_MUSCLE_WITH_SUCROSE  # scripted group (container) (typed FeaturePython)
  Dunit = g/cm3
  Dvalue = 1.11
  Group = -> [H_element059,C_element065,N_element027,O_element067]
  conduct = 2
  density = 1
  expand = 3
  formula = G4_MUSCLE_WITH_SUCROSE
  name = G4_MUSCLE_WITH_SUCROSE
  specific = 4
FEATURE [App::DocumentObjectGroupPython] H_element060  label="H_element : 0.138"  # scripted group (container) (typed FeaturePython)
  n = 0.101969
FEATURE [App::DocumentObjectGroupPython] C_element066  label="C_element : 0.120"  # scripted group (container) (typed FeaturePython)
  n = 0.120058
FEATURE [App::DocumentObjectGroupPython] N_element028  label="N_element : 0.758"  # scripted group (container) (typed FeaturePython)
  n = 0.035451
FEATURE [App::DocumentObjectGroupPython] O_element068  label="O_element : 0.743"  # scripted group (container) (typed FeaturePython)
  n = 0.742522
FEATURE [App::DocumentObjectGroupPython] G4_MUSCLE_WITHOUT_SUCROSE  # scripted group (container) (typed FeaturePython)
  Dunit = g/cm3
  Dvalue = 1.07
  Group = -> [H_element060,C_element066,N_element028,O_element068]
  conduct = 2
  density = 1
  expand = 3
  formula = G4_MUSCLE_WITHOUT_SUCROSE
  name = G4_MUSCLE_WITHOUT_SUCROSE
  specific = 4
FEATURE [App::DocumentObjectGroupPython] C_element067  label="C_element : 10"  # scripted group (container) (typed FeaturePython)
  n = 10
  ref = C_element
FEATURE [App::DocumentObjectGroupPython] H_element061  label="H_element : 030"  # scripted group (container) (typed FeaturePython)
  n = 8
  ref = H_element
FEATURE [App::DocumentObjectGroupPython] G4_NAPHTHALENE  # scripted group (container) (typed FeaturePython)
  Dunit = g/cm3
  Dvalue = 1.145
  Group = -> [C_element067,H_element061]
  conduct = 2
  density = 1
  expand = 3
  formula = G4_NAPHTHALENE
  name = G4_NAPHTHALENE
  specific = 4
FEATURE [App::DocumentObjectGroupPython] C_element068  label="C_element : 034"  # scripted group (container) (typed FeaturePython)
  n = 6
  ref = C_element
FEATURE [App::DocumentObjectGroupPython] H_element062  label="H_element : 031"  # scripted group (container) (typed FeaturePython)
  n = 5
  ref = H_element
FEATURE [App::DocumentObjectGroupPython] N_element029  label="N_element : 012"  # scripted group (container) (typed FeaturePython)
  n = 1
  ref = N_element
FEATURE [App::DocumentObjectGroupPython] O_element069  label="O_element : 034"  # scripted group (container) (typed FeaturePython)
  n = 2
  ref = O_element
FEATURE [App::DocumentObjectGroupPython] G4_NITROBENZENE  # scripted group (container) (typed FeaturePython)
  Dunit = g/cm3
  Dvalue = 1.19867
  Group = -> [C_element068,H_element062,N_element029,O_element069]
  conduct = 2
  density = 1
  expand = 3
  formula = G4_NITROBENZENE
  name = G4_NITROBENZENE
  specific = 4
FEATURE [App::DocumentObjectGroupPython] N_element030  label="N_element : 013"  # scripted group (container) (typed FeaturePython)
  n = 2
  ref = N_element
FEATURE [App::DocumentObjectGroupPython] O_element070  label="O_element : 035"  # scripted group (container) (typed FeaturePython)
  n = 1
  ref = O_element
FEATURE [App::DocumentObjectGroupPython] G4_NITROUS_OXIDE  # scripted group (container) (typed FeaturePython)
  Dunit = g/cm3
  Dvalue = 0.00183094
  Group = -> [N_element030,O_element070]
  conduct = 2
  density = 1
  expand = 3
  formula = G4_NITROUS_OXIDE
  name = G4_NITROUS_OXIDE
  specific = 4
FEATURE [App::DocumentObjectGroupPython] H_element063  label="H_element : 0.104"  # scripted group (container) (typed FeaturePython)
  n = 0.103509
FEATURE [App::DocumentObjectGroupPython] C_element069  label="C_element : 0.648"  # scripted group (container) (typed FeaturePython)
  n = 0.648416
FEATURE [App::DocumentObjectGroupPython] N_element031  label="N_element : 0.100"  # scripted group (container) (typed FeaturePython)
  n = 0.0995361
FEATURE [App::DocumentObjectGroupPython] O_element071  label="O_element : 0.149"  # scripted group (container) (typed FeaturePython)
  n = 0.148539
FEATURE [App::DocumentObjectGroupPython] G4_NYLON_8062  label="G4_NYLON-8062"  # scripted group (container) (typed FeaturePython)
  Dunit = g/cm3
  Dvalue = 1.08
  Group = -> [H_element063,C_element069,N_element031,O_element071]
  conduct = 2
  density = 1
  expand = 3
  formula = G4_NYLON-8062
  name = G4_NYLON-8062
  specific = 4
FEATURE [App::DocumentObjectGroupPython] C_element070  label="C_element : 035"  # scripted group (container) (typed FeaturePython)
  n = 6
  ref = C_element
FEATURE [App::DocumentObjectGroupPython] H_element064  label="H_element : 11"  # scripted group (container) (typed FeaturePython)
  n = 11
  ref = H_element
FEATURE [App::DocumentObjectGroupPython] N_element032  label="N_element : 014"  # scripted group (container) (typed FeaturePython)
  n = 1
  ref = N_element
FEATURE [App::DocumentObjectGroupPython] O_element072  label="O_element : 036"  # scripted group (container) (typed FeaturePython)
  n = 1
  ref = O_element
FEATURE [App::DocumentObjectGroupPython] G4_NYLON_6_6  label="G4_NYLON-6-6"  # scripted group (container) (typed FeaturePython)
  Dunit = g/cm3
  Dvalue = 1.14
  Group = -> [C_element070,H_element064,N_element032,O_element072]
  conduct = 2
  density = 1
  expand = 3
  formula = G4_NYLON-6-6
  name = G4_NYLON-6-6
  specific = 4
FEATURE [App::DocumentObjectGroupPython] H_element065  label="H_element : 0.139"  # scripted group (container) (typed FeaturePython)
  n = 0.107062
FEATURE [App::DocumentObjectGroupPython] C_element071  label="C_element : 0.680"  # scripted group (container) (typed FeaturePython)
  n = 0.680449
FEATURE [App::DocumentObjectGroupPython] N_element033  label="N_element : 0.099"  # scripted group (container) (typed FeaturePython)
  n = 0.099189
FEATURE [App::DocumentObjectGroupPython] O_element073  label="O_element : 0.113"  # scripted group (container) (typed FeaturePython)
  n = 0.1133
FEATURE [App::DocumentObjectGroupPython] G4_NYLON_6_10  label="G4_NYLON-6-10"  # scripted group (container) (typed FeaturePython)
  Dunit = g/cm3
  Dvalue = 1.14
  Group = -> [H_element065,C_element071,N_element033,O_element073]
  conduct = 2
  density = 1
  expand = 3
  formula = G4_NYLON-6-10
  name = G4_NYLON-6-10
  specific = 4
FEATURE [App::DocumentObjectGroupPython] H_element066  label="H_element : 0.140"  # scripted group (container) (typed FeaturePython)
  n = 0.115476
FEATURE [App::DocumentObjectGroupPython] C_element072  label="C_element : 0.721"  # scripted group (container) (typed FeaturePython)
  n = 0.720818
FEATURE [App::DocumentObjectGroupPython] N_element034  label="N_element : 0.076"  # scripted group (container) (typed FeaturePython)
  n = 0.0764169
FEATURE [App::DocumentObjectGroupPython] O_element074  label="O_element : 0.087"  # scripted group (container) (typed FeaturePython)
  n = 0.0872889
FEATURE [App::DocumentObjectGroupPython] G4_NYLON_11_RILSAN  label="G4_NYLON-11_RILSAN"  # scripted group (container) (typed FeaturePython)
  Dunit = g/cm3
  Dvalue = 1.425
  Group = -> [H_element066,C_element072,N_element034,O_element074]
  conduct = 2
  density = 1
  expand = 3
  formula = G4_NYLON-11_RILSAN
  name = G4_NYLON-11_RILSAN
  specific = 4
FEATURE [App::DocumentObjectGroupPython] C_element073  label="C_element : 8"  # scripted group (container) (typed FeaturePython)
  n = 8
  ref = C_element
FEATURE [App::DocumentObjectGroupPython] H_element067  label="H_element : 18"  # scripted group (container) (typed FeaturePython)
  n = 18
  ref = H_element
FEATURE [App::DocumentObjectGroupPython] G4_OCTANE  # scripted group (container) (typed FeaturePython)
  Dunit = g/cm3
  Dvalue = 0.7026
  Group = -> [C_element073,H_element067]
  conduct = 2
  density = 1
  expand = 3
  formula = G4_OCTANE
  name = G4_OCTANE
  specific = 4
FEATURE [App::DocumentObjectGroupPython] C_element074  label="C_element : 25"  # scripted group (container) (typed FeaturePython)
  n = 25
  ref = C_element
FEATURE [App::DocumentObjectGroupPython] H_element068  label="H_element : 52"  # scripted group (container) (typed FeaturePython)
  n = 52
  ref = H_element
FEATURE [App::DocumentObjectGroupPython] G4_PARAFFIN  # scripted group (container) (typed FeaturePython)
  Dunit = g/cm3
  Dvalue = 0.93
  Group = -> [C_element074,H_element068]
  conduct = 2
  density = 1
  expand = 3
  formula = G4_PARAFFIN
  name = G4_PARAFFIN
  specific = 4
FEATURE [App::DocumentObjectGroupPython] C_element075  label="C_element : 036"  # scripted group (container) (typed FeaturePython)
  n = 5
  ref = C_element
FEATURE [App::DocumentObjectGroupPython] H_element069  label="H_element : 032"  # scripted group (container) (typed FeaturePython)
  n = 12
  ref = H_element
FEATURE [App::DocumentObjectGroupPython] G4_N_PENTANE  label="G4_N-PENTANE"  # scripted group (container) (typed FeaturePython)
  Dunit = g/cm3
  Dvalue = 0.6262
  Group = -> [C_element075,H_element069]
  conduct = 2
  density = 1
  expand = 3
  formula = G4_N-PENTANE
  name = G4_N-PENTANE
  specific = 4
FEATURE [App::DocumentObjectGroupPython] H_element070  label="H_element : 0.014"  # scripted group (container) (typed FeaturePython)
  n = 0.0141
FEATURE [App::DocumentObjectGroupPython] C_element076  label="C_element : 0.072"  # scripted group (container) (typed FeaturePython)
  n = 0.072261
FEATURE [App::DocumentObjectGroupPython] N_element035  label="N_element : 0.019"  # scripted group (container) (typed FeaturePython)
  n = 0.01932
FEATURE [App::DocumentObjectGroupPython] O_element075  label="O_element : 0.066"  # scripted group (container) (typed FeaturePython)
  n = 0.066101
FEATURE [App::DocumentObjectGroupPython] S_element019  label="S_element : 0.020"  # scripted group (container) (typed FeaturePython)
  n = 0.00189
FEATURE [App::DocumentObjectGroupPython] Br_element004  label="Br_element : 0.349"  # scripted group (container) (typed FeaturePython)
  n = 0.349103
FEATURE [App::DocumentObjectGroupPython] Ag_element001  label="Ag_element : 0.474"  # scripted group (container) (typed FeaturePython)
  n = 0.474105
FEATURE [App::DocumentObjectGroupPython] I_element005  label="I_element : 0.003"  # scripted group (container) (typed FeaturePython)
  n = 0.00312
FEATURE [App::DocumentObjectGroupPython] G4_PHOTO_EMULSION  # scripted group (container) (typed FeaturePython)
  Dunit = g/cm3
  Dvalue = 3.815
  Group = -> [H_element070,C_element076,N_element035,O_element075,S_element019,Br_element004,Ag_element001,I_element005]
  conduct = 2
  density = 1
  expand = 3
  formula = G4_PHOTO_EMULSION
  name = G4_PHOTO_EMULSION
  specific = 4
FEATURE [App::DocumentObjectGroupPython] C_element077  label="C_element : 9"  # scripted group (container) (typed FeaturePython)
  n = 9
  ref = C_element
FEATURE [App::DocumentObjectGroupPython] H_element071  label="H_element : 033"  # scripted group (container) (typed FeaturePython)
  n = 10
  ref = H_element
FEATURE [App::DocumentObjectGroupPython] G4_PLASTIC_SC_VINYLTOLUENE  # scripted group (container) (typed FeaturePython)
  Dunit = g/cm3
  Dvalue = 1.032
  Group = -> [C_element077,H_element071]
  conduct = 2
  density = 1
  expand = 3
  formula = G4_PLASTIC_SC_VINYLTOLUENE
  name = G4_PLASTIC_SC_VINYLTOLUENE
  specific = 4
FEATURE [App::DocumentObjectGroupPython] Pu_element001  label="Pu_element : 1"  # scripted group (container) (typed FeaturePython)
  n = 1
  ref = Pu_element
FEATURE [App::DocumentObjectGroupPython] O_element076  label="O_element : 037"  # scripted group (container) (typed FeaturePython)
  n = 2
  ref = O_element
FEATURE [App::DocumentObjectGroupPython] G4_PLUTONIUM_DIOXIDE  # scripted group (container) (typed FeaturePython)
  Dunit = g/cm3
  Dvalue = 11.46
  Group = -> [Pu_element001,O_element076]
  conduct = 2
  density = 1
  expand = 3
  formula = G4_PLUTONIUM_DIOXIDE
  name = G4_PLUTONIUM_DIOXIDE
  specific = 4
FEATURE [App::DocumentObjectGroupPython] C_element078  label="C_element : 037"  # scripted group (container) (typed FeaturePython)
  n = 3
  ref = C_element
FEATURE [App::DocumentObjectGroupPython] H_element072  label="H_element : 034"  # scripted group (container) (typed FeaturePython)
  n = 3
  ref = H_element
FEATURE [App::DocumentObjectGroupPython] N_element036  label="N_element : 015"  # scripted group (container) (typed FeaturePython)
  n = 1
  ref = N_element
FEATURE [App::DocumentObjectGroupPython] G4_POLYACRYLONITRILE  # scripted group (container) (typed FeaturePython)
  Dunit = g/cm3
  Dvalue = 1.17
  Group = -> [C_element078,H_element072,N_element036]
  conduct = 2
  density = 1
  expand = 3
  formula = G4_POLYACRYLONITRILE
  name = G4_POLYACRYLONITRILE
  specific = 4
FEATURE [App::DocumentObjectGroupPython] C_element079  label="C_element : 16"  # scripted group (container) (typed FeaturePython)
  n = 16
  ref = C_element
FEATURE [App::DocumentObjectGroupPython] H_element073  label="H_element : 035"  # scripted group (container) (typed FeaturePython)
  n = 14
  ref = H_element
FEATURE [App::DocumentObjectGroupPython] O_element077  label="O_element : 038"  # scripted group (container) (typed FeaturePython)
  n = 3
  ref = O_element
FEATURE [App::DocumentObjectGroupPython] G4_POLYCARBONATE  # scripted group (container) (typed FeaturePython)
  Dunit = g/cm3
  Dvalue = 1.2
  Group = -> [C_element079,H_element073,O_element077]
  conduct = 2
  density = 1
  expand = 3
  formula = G4_POLYCARBONATE
  name = G4_POLYCARBONATE
  specific = 4
FEATURE [App::DocumentObjectGroupPython] C_element080  label="C_element : 038"  # scripted group (container) (typed FeaturePython)
  n = 8
  ref = C_element
FEATURE [App::DocumentObjectGroupPython] H_element074  label="H_element : 036"  # scripted group (container) (typed FeaturePython)
  n = 7
  ref = H_element
FEATURE [App::DocumentObjectGroupPython] Cl_element017  label="Cl_element : 007"  # scripted group (container) (typed FeaturePython)
  n = 1
  ref = Cl_element
FEATURE [App::DocumentObjectGroupPython] G4_POLYCHLOROSTYRENE  # scripted group (container) (typed FeaturePython)
  Dunit = g/cm3
  Dvalue = 1.3
  Group = -> [C_element080,H_element074,Cl_element017]
  conduct = 2
  density = 1
  expand = 3
  formula = G4_POLYCHLOROSTYRENE
  name = G4_POLYCHLOROSTYRENE
  specific = 4
FEATURE [App::DocumentObjectGroupPython] C_element081  label="C_element : 039"  # scripted group (container) (typed FeaturePython)
  n = 1
  ref = C_element
FEATURE [App::DocumentObjectGroupPython] H_element075  label="H_element : 037"  # scripted group (container) (typed FeaturePython)
  n = 2
  ref = H_element
FEATURE [App::DocumentObjectGroupPython] G4_POLYETHYLENE  # scripted group (container) (typed FeaturePython)
  Dunit = g/cm3
  Dvalue = 0.94
  Group = -> [C_element081,H_element075]
  conduct = 2
  density = 1
  expand = 3
  formula = G4_POLYETHYLENE
  name = G4_POLYETHYLENE
  specific = 4
FEATURE [App::DocumentObjectGroupPython] C_element082  label="C_element : 040"  # scripted group (container) (typed FeaturePython)
  n = 10
  ref = C_element
FEATURE [App::DocumentObjectGroupPython] H_element076  label="H_element : 038"  # scripted group (container) (typed FeaturePython)
  n = 8
  ref = H_element
FEATURE [App::DocumentObjectGroupPython] O_element078  label="O_element : 039"  # scripted group (container) (typed FeaturePython)
  n = 4
  ref = O_element
FEATURE [App::DocumentObjectGroupPython] G4_MYLAR  # scripted group (container) (typed FeaturePython)
  Dunit = g/cm3
  Dvalue = 1.4
  Group = -> [C_element082,H_element076,O_element078]
  conduct = 2
  density = 1
  expand = 3
  formula = G4_MYLAR
  name = G4_MYLAR
  specific = 4
FEATURE [App::DocumentObjectGroupPython] C_element083  label="C_element : 041"  # scripted group (container) (typed FeaturePython)
  n = 5
  ref = C_element
FEATURE [App::DocumentObjectGroupPython] H_element077  label="H_element : 039"  # scripted group (container) (typed FeaturePython)
  n = 8
  ref = H_element
FEATURE [App::DocumentObjectGroupPython] O_element079  label="O_element : 040"  # scripted group (container) (typed FeaturePython)
  n = 2
  ref = O_element
FEATURE [App::DocumentObjectGroupPython] G4_PLEXIGLASS  # scripted group (container) (typed FeaturePython)
  Dunit = g/cm3
  Dvalue = 1.19
  Group = -> [C_element083,H_element077,O_element079]
  conduct = 2
  density = 1
  expand = 3
  formula = G4_PLEXIGLASS
  name = G4_PLEXIGLASS
  specific = 4
FEATURE [App::DocumentObjectGroupPython] C_element084  label="C_element : 042"  # scripted group (container) (typed FeaturePython)
  n = 1
  ref = C_element
FEATURE [App::DocumentObjectGroupPython] H_element078  label="H_element : 040"  # scripted group (container) (typed FeaturePython)
  n = 2
  ref = H_element
FEATURE [App::DocumentObjectGroupPython] O_element080  label="O_element : 041"  # scripted group (container) (typed FeaturePython)
  n = 1
  ref = O_element
FEATURE [App::DocumentObjectGroupPython] G4_POLYOXYMETHYLENE  # scripted group (container) (typed FeaturePython)
  Dunit = g/cm3
  Dvalue = 1.425
  Group = -> [C_element084,H_element078,O_element080]
  conduct = 2
  density = 1
  expand = 3
  formula = G4_POLYOXYMETHYLENE
  name = G4_POLYOXYMETHYLENE
  specific = 4
FEATURE [App::DocumentObjectGroupPython] C_element085  label="C_element : 043"  # scripted group (container) (typed FeaturePython)
  n = 2
  ref = C_element
FEATURE [App::DocumentObjectGroupPython] H_element079  label="H_element : 041"  # scripted group (container) (typed FeaturePython)
  n = 4
  ref = H_element
FEATURE [App::DocumentObjectGroupPython] G4_POLYPROPYLENE  # scripted group (container) (typed FeaturePython)
  Dunit = g/cm3
  Dvalue = 0.9
  Group = -> [C_element085,H_element079]
  conduct = 2
  density = 1
  expand = 3
  formula = G4_POLYPROPYLENE
  name = G4_POLYPROPYLENE
  specific = 4
FEATURE [App::DocumentObjectGroupPython] C_element086  label="C_element : 044"  # scripted group (container) (typed FeaturePython)
  n = 8
  ref = C_element
FEATURE [App::DocumentObjectGroupPython] H_element080  label="H_element : 042"  # scripted group (container) (typed FeaturePython)
  n = 8
  ref = H_element
FEATURE [App::DocumentObjectGroupPython] G4_POLYSTYRENE  # scripted group (container) (typed FeaturePython)
  Dunit = g/cm3
  Dvalue = 1.06
  Group = -> [C_element086,H_element080]
  conduct = 2
  density = 1
  expand = 3
  formula = G4_POLYSTYRENE
  name = G4_POLYSTYRENE
  specific = 4
FEATURE [App::DocumentObjectGroupPython] C_element087  label="C_element : 045"  # scripted group (container) (typed FeaturePython)
  n = 2
  ref = C_element
FEATURE [App::DocumentObjectGroupPython] F_element014  label="F_element : 4"  # scripted group (container) (typed FeaturePython)
  n = 4
  ref = F_element
FEATURE [App::DocumentObjectGroupPython] G4_TEFLON  # scripted group (container) (typed FeaturePython)
  Dunit = g/cm3
  Dvalue = 2.2
  Group = -> [C_element087,F_element014]
  conduct = 2
  density = 1
  expand = 3
  formula = G4_TEFLON
  name = G4_TEFLON
  specific = 4
FEATURE [App::DocumentObjectGroupPython] C_element088  label="C_element : 046"  # scripted group (container) (typed FeaturePython)
  n = 2
  ref = C_element
FEATURE [App::DocumentObjectGroupPython] F_element015  label="F_element : 006"  # scripted group (container) (typed FeaturePython)
  n = 3
  ref = F_element
FEATURE [App::DocumentObjectGroupPython] Cl_element018  label="Cl_element : 008"  # scripted group (container) (typed FeaturePython)
  n = 1
  ref = Cl_element
FEATURE [App::DocumentObjectGroupPython] G4_POLYTRIFLUOROCHLOROETHYLENE  # scripted group (container) (typed FeaturePython)
  Dunit = g/cm3
  Dvalue = 2.1
  Group = -> [C_element088,F_element015,Cl_element018]
  conduct = 2
  density = 1
  expand = 3
  formula = G4_POLYTRIFLUOROCHLOROETHYLENE
  name = G4_POLYTRIFLUOROCHLOROETHYLENE
  specific = 4
FEATURE [App::DocumentObjectGroupPython] C_element089  label="C_element : 047"  # scripted group (container) (typed FeaturePython)
  n = 4
  ref = C_element
FEATURE [App::DocumentObjectGroupPython] H_element081  label="H_element : 043"  # scripted group (container) (typed FeaturePython)
  n = 6
  ref = H_element
FEATURE [App::DocumentObjectGroupPython] O_element081  label="O_element : 042"  # scripted group (container) (typed FeaturePython)
  n = 2
  ref = O_element
FEATURE [App::DocumentObjectGroupPython] G4_POLYVINYL_ACETATE  # scripted group (container) (typed FeaturePython)
  Dunit = g/cm3
  Dvalue = 1.19
  Group = -> [C_element089,H_element081,O_element081]
  conduct = 2
  density = 1
  expand = 3
  formula = G4_POLYVINYL_ACETATE
  name = G4_POLYVINYL_ACETATE
  specific = 4
FEATURE [App::DocumentObjectGroupPython] C_element090  label="C_element : 048"  # scripted group (container) (typed FeaturePython)
  n = 2
  ref = C_element
FEATURE [App::DocumentObjectGroupPython] H_element082  label="H_element : 044"  # scripted group (container) (typed FeaturePython)
  n = 4
  ref = H_element
FEATURE [App::DocumentObjectGroupPython] O_element082  label="O_element : 043"  # scripted group (container) (typed FeaturePython)
  n = 1
  ref = O_element
FEATURE [App::DocumentObjectGroupPython] G4_POLYVINYL_ALCOHOL  # scripted group (container) (typed FeaturePython)
  Dunit = g/cm3
  Dvalue = 1.3
  Group = -> [C_element090,H_element082,O_element082]
  conduct = 2
  density = 1
  expand = 3
  formula = G4_POLYVINYL_ALCOHOL
  name = G4_POLYVINYL_ALCOHOL
  specific = 4
FEATURE [App::DocumentObjectGroupPython] C_element091  label="C_element : 049"  # scripted group (container) (typed FeaturePython)
  n = 8
  ref = C_element
FEATURE [App::DocumentObjectGroupPython] H_element083  label="H_element : 045"  # scripted group (container) (typed FeaturePython)
  n = 14
  ref = H_element
FEATURE [App::DocumentObjectGroupPython] O_element083  label="O_element : 044"  # scripted group (container) (typed FeaturePython)
  n = 2
  ref = O_element
FEATURE [App::DocumentObjectGroupPython] G4_POLYVINYL_BUTYRAL  # scripted group (container) (typed FeaturePython)
  Dunit = g/cm3
  Dvalue = 1.12
  Group = -> [C_element091,H_element083,O_element083]
  conduct = 2
  density = 1
  expand = 3
  formula = G4_POLYVINYL_BUTYRAL
  name = G4_POLYVINYL_BUTYRAL
  specific = 4
FEATURE [App::DocumentObjectGroupPython] C_element092  label="C_element : 050"  # scripted group (container) (typed FeaturePython)
  n = 2
  ref = C_element
FEATURE [App::DocumentObjectGroupPython] H_element084  label="H_element : 046"  # scripted group (container) (typed FeaturePython)
  n = 3
  ref = H_element
FEATURE [App::DocumentObjectGroupPython] Cl_element019  label="Cl_element : 009"  # scripted group (container) (typed FeaturePython)
  n = 1
  ref = Cl_element
FEATURE [App::DocumentObjectGroupPython] G4_POLYVINYL_CHLORIDE  # scripted group (container) (typed FeaturePython)
  Dunit = g/cm3
  Dvalue = 1.3
  Group = -> [C_element092,H_element084,Cl_element019]
  conduct = 2
  density = 1
  expand = 3
  formula = G4_POLYVINYL_CHLORIDE
  name = G4_POLYVINYL_CHLORIDE
  specific = 4
FEATURE [App::DocumentObjectGroupPython] C_element093  label="C_element : 051"  # scripted group (container) (typed FeaturePython)
  n = 2
  ref = C_element
FEATURE [App::DocumentObjectGroupPython] H_element085  label="H_element : 047"  # scripted group (container) (typed FeaturePython)
  n = 2
  ref = H_element
FEATURE [App::DocumentObjectGroupPython] Cl_element020  label="Cl_element : 010"  # scripted group (container) (typed FeaturePython)
  n = 2
  ref = Cl_element
FEATURE [App::DocumentObjectGroupPython] G4_POLYVINYLIDENE_CHLORIDE  # scripted group (container) (typed FeaturePython)
  Dunit = g/cm3
  Dvalue = 1.7
  Group = -> [C_element093,H_element085,Cl_element020]
  conduct = 2
  density = 1
  expand = 3
  formula = G4_POLYVINYLIDENE_CHLORIDE
  name = G4_POLYVINYLIDENE_CHLORIDE
  specific = 4
FEATURE [App::DocumentObjectGroupPython] C_element094  label="C_element : 052"  # scripted group (container) (typed FeaturePython)
  n = 2
  ref = C_element
FEATURE [App::DocumentObjectGroupPython] H_element086  label="H_element : 048"  # scripted group (container) (typed FeaturePython)
  n = 2
  ref = H_element
FEATURE [App::DocumentObjectGroupPython] F_element016  label="F_element : 007"  # scripted group (container) (typed FeaturePython)
  n = 2
  ref = F_element
FEATURE [App::DocumentObjectGroupPython] G4_POLYVINYLIDENE_FLUORIDE  # scripted group (container) (typed FeaturePython)
  Dunit = g/cm3
  Dvalue = 1.76
  Group = -> [C_element094,H_element086,F_element016]
  conduct = 2
  density = 1
  expand = 3
  formula = G4_POLYVINYLIDENE_FLUORIDE
  name = G4_POLYVINYLIDENE_FLUORIDE
  specific = 4
FEATURE [App::DocumentObjectGroupPython] C_element095  label="C_element : 053"  # scripted group (container) (typed FeaturePython)
  n = 6
  ref = C_element
FEATURE [App::DocumentObjectGroupPython] H_element087  label="H_element : 9"  # scripted group (container) (typed FeaturePython)
  n = 9
  ref = H_element
FEATURE [App::DocumentObjectGroupPython] N_element037  label="N_element : 016"  # scripted group (container) (typed FeaturePython)
  n = 1
  ref = N_element
FEATURE [App::DocumentObjectGroupPython] O_element084  label="O_element : 045"  # scripted group (container) (typed FeaturePython)
  n = 1
  ref = O_element
FEATURE [App::DocumentObjectGroupPython] G4_POLYVINYL_PYRROLIDONE  # scripted group (container) (typed FeaturePython)
  Dunit = g/cm3
  Dvalue = 1.25
  Group = -> [C_element095,H_element087,N_element037,O_element084]
  conduct = 2
  density = 1
  expand = 3
  formula = G4_POLYVINYL_PYRROLIDONE
  name = G4_POLYVINYL_PYRROLIDONE
  specific = 4
FEATURE [App::DocumentObjectGroupPython] K_element008  label="K_element : 1"  # scripted group (container) (typed FeaturePython)
  n = 1
  ref = K_element
FEATURE [App::DocumentObjectGroupPython] I_element006  label="I_element : 003"  # scripted group (container) (typed FeaturePython)
  n = 1
  ref = I_element
FEATURE [App::DocumentObjectGroupPython] G4_POTASSIUM_IODIDE  # scripted group (container) (typed FeaturePython)
  Dunit = g/cm3
  Dvalue = 3.13
  Group = -> [K_element008,I_element006]
  conduct = 2
  density = 1
  expand = 3
  formula = G4_POTASSIUM_IODIDE
  name = G4_POTASSIUM_IODIDE
  specific = 4
FEATURE [App::DocumentObjectGroupPython] K_element009  label="K_element : 2"  # scripted group (container) (typed FeaturePython)
  n = 2
  ref = K_element
FEATURE [App::DocumentObjectGroupPython] O_element085  label="O_element : 046"  # scripted group (container) (typed FeaturePython)
  n = 1
  ref = O_element
FEATURE [App::DocumentObjectGroupPython] G4_POTASSIUM_OXIDE  # scripted group (container) (typed FeaturePython)
  Dunit = g/cm3
  Dvalue = 2.32
  Group = -> [K_element009,O_element085]
  conduct = 2
  density = 1
  expand = 3
  formula = G4_POTASSIUM_OXIDE
  name = G4_POTASSIUM_OXIDE
  specific = 4
FEATURE [App::DocumentObjectGroupPython] C_element096  label="C_element : 054"  # scripted group (container) (typed FeaturePython)
  n = 3
  ref = C_element
FEATURE [App::DocumentObjectGroupPython] H_element088  label="H_element : 049"  # scripted group (container) (typed FeaturePython)
  n = 8
  ref = H_element
FEATURE [App::DocumentObjectGroupPython] G4_PROPANE  # scripted group (container) (typed FeaturePython)
  Dunit = g/cm3
  Dvalue = 0.00187939
  Group = -> [C_element096,H_element088]
  conduct = 2
  density = 1
  expand = 3
  formula = G4_PROPANE
  name = G4_PROPANE
  specific = 4
FEATURE [App::DocumentObjectGroupPython] C_element097  label="C_element : 055"  # scripted group (container) (typed FeaturePython)
  n = 3
  ref = C_element
FEATURE [App::DocumentObjectGroupPython] H_element089  label="H_element : 050"  # scripted group (container) (typed FeaturePython)
  n = 8
  ref = H_element
FEATURE [App::DocumentObjectGroupPython] G4_lPROPANE  # scripted group (container) (typed FeaturePython)
  Dunit = g/cm3
  Dvalue = 0.43
  Group = -> [C_element097,H_element089]
  conduct = 2
  density = 1
  expand = 3
  formula = G4_lPROPANE
  name = G4_lPROPANE
  specific = 4
FEATURE [App::DocumentObjectGroupPython] C_element098  label="C_element : 056"  # scripted group (container) (typed FeaturePython)
  n = 3
  ref = C_element
FEATURE [App::DocumentObjectGroupPython] H_element090  label="H_element : 051"  # scripted group (container) (typed FeaturePython)
  n = 8
  ref = H_element
FEATURE [App::DocumentObjectGroupPython] O_element086  label="O_element : 047"  # scripted group (container) (typed FeaturePython)
  n = 1
  ref = O_element
FEATURE [App::DocumentObjectGroupPython] G4_N_PROPYL_ALCOHOL  label="G4_N-PROPYL_ALCOHOL"  # scripted group (container) (typed FeaturePython)
  Dunit = g/cm3
  Dvalue = 0.8035
  Group = -> [C_element098,H_element090,O_element086]
  conduct = 2
  density = 1
  expand = 3
  formula = G4_N-PROPYL_ALCOHOL
  name = G4_N-PROPYL_ALCOHOL
  specific = 4
FEATURE [App::DocumentObjectGroupPython] C_element099  label="C_element : 057"  # scripted group (container) (typed FeaturePython)
  n = 5
  ref = C_element
FEATURE [App::DocumentObjectGroupPython] H_element091  label="H_element : 052"  # scripted group (container) (typed FeaturePython)
  n = 5
  ref = H_element
FEATURE [App::DocumentObjectGroupPython] N_element038  label="N_element : 017"  # scripted group (container) (typed FeaturePython)
  n = 1
  ref = N_element
FEATURE [App::DocumentObjectGroupPython] G4_PYRIDINE  # scripted group (container) (typed FeaturePython)
  Dunit = g/cm3
  Dvalue = 0.9819
  Group = -> [C_element099,H_element091,N_element038]
  conduct = 2
  density = 1
  expand = 3
  formula = G4_PYRIDINE
  name = G4_PYRIDINE
  specific = 4
FEATURE [App::DocumentObjectGroupPython] H_element092  label="H_element : 0.144"  # scripted group (container) (typed FeaturePython)
  n = 0.143711
FEATURE [App::DocumentObjectGroupPython] C_element100  label="C_element : 0.856"  # scripted group (container) (typed FeaturePython)
  n = 0.856289
FEATURE [App::DocumentObjectGroupPython] G4_RUBBER_BUTYL  # scripted group (container) (typed FeaturePython)
  Dunit = g/cm3
  Dvalue = 0.92
  Group = -> [H_element092,C_element100]
  conduct = 2
  density = 1
  expand = 3
  formula = G4_RUBBER_BUTYL
  name = G4_RUBBER_BUTYL
  specific = 4
FEATURE [App::DocumentObjectGroupPython] H_element093  label="H_element : 0.118"  # scripted group (container) (typed FeaturePython)
  n = 0.118371
FEATURE [App::DocumentObjectGroupPython] C_element101  label="C_element : 0.882"  # scripted group (container) (typed FeaturePython)
  n = 0.881629
FEATURE [App::DocumentObjectGroupPython] G4_RUBBER_NATURAL  # scripted group (container) (typed FeaturePython)
  Dunit = g/cm3
  Dvalue = 0.92
  Group = -> [H_element093,C_element101]
  conduct = 2
  density = 1
  expand = 3
  formula = G4_RUBBER_NATURAL
  name = G4_RUBBER_NATURAL
  specific = 4
FEATURE [App::DocumentObjectGroupPython] H_element094  label="H_element : 0.145"  # scripted group (container) (typed FeaturePython)
  n = 0.05692
FEATURE [App::DocumentObjectGroupPython] C_element102  label="C_element : 0.543"  # scripted group (container) (typed FeaturePython)
  n = 0.542646
FEATURE [App::DocumentObjectGroupPython] Cl_element021  label="Cl_element : 0.400"  # scripted group (container) (typed FeaturePython)
  n = 0.400434
FEATURE [App::DocumentObjectGroupPython] G4_RUBBER_NEOPRENE  # scripted group (container) (typed FeaturePython)
  Dunit = g/cm3
  Dvalue = 1.23
  Group = -> [H_element094,C_element102,Cl_element021]
  conduct = 2
  density = 1
  expand = 3
  formula = G4_RUBBER_NEOPRENE
  name = G4_RUBBER_NEOPRENE
  specific = 4
FEATURE [App::DocumentObjectGroupPython] Si_element006  label="Si_element : 1"  # scripted group (container) (typed FeaturePython)
  n = 1
  ref = Si_element
FEATURE [App::DocumentObjectGroupPython] O_element087  label="O_element : 048"  # scripted group (container) (typed FeaturePython)
  n = 2
  ref = O_element
FEATURE [App::DocumentObjectGroupPython] G4_SILICON_DIOXIDE  # scripted group (container) (typed FeaturePython)
  Dunit = g/cm3
  Dvalue = 2.32
  Group = -> [Si_element006,O_element087]
  conduct = 2
  density = 1
  expand = 3
  formula = G4_SILICON_DIOXIDE
  name = G4_SILICON_DIOXIDE
  specific = 4
FEATURE [App::DocumentObjectGroupPython] Ag_element002  label="Ag_element : 1"  # scripted group (container) (typed FeaturePython)
  n = 1
  ref = Ag_element
FEATURE [App::DocumentObjectGroupPython] Br_element005  label="Br_element : 003"  # scripted group (container) (typed FeaturePython)
  n = 1
  ref = Br_element
FEATURE [App::DocumentObjectGroupPython] G4_SILVER_BROMIDE  # scripted group (container) (typed FeaturePython)
  Dunit = g/cm3
  Dvalue = 6.473
  Group = -> [Ag_element002,Br_element005]
  conduct = 2
  density = 1
  expand = 3
  formula = G4_SILVER_BROMIDE
  name = G4_SILVER_BROMIDE
  specific = 4
FEATURE [App::DocumentObjectGroupPython] Ag_element003  label="Ag_element : 002"  # scripted group (container) (typed FeaturePython)
  n = 1
  ref = Ag_element
FEATURE [App::DocumentObjectGroupPython] Cl_element022  label="Cl_element : 011"  # scripted group (container) (typed FeaturePython)
  n = 1
  ref = Cl_element
FEATURE [App::DocumentObjectGroupPython] G4_SILVER_CHLORIDE  # scripted group (container) (typed FeaturePython)
  Dunit = g/cm3
  Dvalue = 5.56
  Group = -> [Ag_element003,Cl_element022]
  conduct = 2
  density = 1
  expand = 3
  formula = G4_SILVER_CHLORIDE
  name = G4_SILVER_CHLORIDE
  specific = 4
FEATURE [App::DocumentObjectGroupPython] Br_element006  label="Br_element : 0.423"  # scripted group (container) (typed FeaturePython)
  n = 0.422895
FEATURE [App::DocumentObjectGroupPython] Ag_element004  label="Ag_element : 0.574"  # scripted group (container) (typed FeaturePython)
  n = 0.573748
FEATURE [App::DocumentObjectGroupPython] I_element007  label="I_element : 0.649"  # scripted group (container) (typed FeaturePython)
  n = 0.003357
FEATURE [App::DocumentObjectGroupPython] G4_SILVER_HALIDES  # scripted group (container) (typed FeaturePython)
  Dunit = g/cm3
  Dvalue = 6.47
  Group = -> [Br_element006,Ag_element004,I_element007]
  conduct = 2
  density = 1
  expand = 3
  formula = G4_SILVER_HALIDES
  name = G4_SILVER_HALIDES
  specific = 4
FEATURE [App::DocumentObjectGroupPython] Ag_element005  label="Ag_element : 003"  # scripted group (container) (typed FeaturePython)
  n = 1
  ref = Ag_element
FEATURE [App::DocumentObjectGroupPython] I_element008  label="I_element : 004"  # scripted group (container) (typed FeaturePython)
  n = 1
  ref = I_element
FEATURE [App::DocumentObjectGroupPython] G4_SILVER_IODIDE  # scripted group (container) (typed FeaturePython)
  Dunit = g/cm3
  Dvalue = 6.01
  Group = -> [Ag_element005,I_element008]
  conduct = 2
  density = 1
  expand = 3
  formula = G4_SILVER_IODIDE
  name = G4_SILVER_IODIDE
  specific = 4
FEATURE [App::DocumentObjectGroupPython] H_element095  label="H_element : 0.100"  # scripted group (container) (typed FeaturePython)
  n = 0.1
FEATURE [App::DocumentObjectGroupPython] C_element103  label="C_element : 0.204"  # scripted group (container) (typed FeaturePython)
  n = 0.204
FEATURE [App::DocumentObjectGroupPython] N_element039  label="N_element : 0.759"  # scripted group (container) (typed FeaturePython)
  n = 0.042
FEATURE [App::DocumentObjectGroupPython] O_element088  label="O_element : 0.645"  # scripted group (container) (typed FeaturePython)
  n = 0.645
FEATURE [App::DocumentObjectGroupPython] Na_element013  label="Na_element : 0.100"  # scripted group (container) (typed FeaturePython)
  n = 0.002
FEATURE [App::DocumentObjectGroupPython] P_element009  label="P_element : 0.107"  # scripted group (container) (typed FeaturePython)
  n = 0.001
FEATURE [App::DocumentObjectGroupPython] S_element020  label="S_element : 0.021"  # scripted group (container) (typed FeaturePython)
  n = 0.002
FEATURE [App::DocumentObjectGroupPython] Cl_element023  label="Cl_element : 0.590"  # scripted group (container) (typed FeaturePython)
  n = 0.003
FEATURE [App::DocumentObjectGroupPython] K_element010  label="K_element : 0.001"  # scripted group (container) (typed FeaturePython)
  n = 0.001
FEATURE [App::DocumentObjectGroupPython] G4_SKIN_ICRP  # scripted group (container) (typed FeaturePython)
  Dunit = g/cm3
  Dvalue = 1.09
  Group = -> [H_element095,C_element103,N_element039,O_element088,Na_element013,P_element009,S_element020,Cl_element023,K_element010]
  conduct = 2
  density = 1
  expand = 3
  formula = G4_SKIN_ICRP
  name = G4_SKIN_ICRP
  specific = 4
FEATURE [App::DocumentObjectGroupPython] Na_element014  label="Na_element : 2"  # scripted group (container) (typed FeaturePython)
  n = 2
  ref = Na_element
FEATURE [App::DocumentObjectGroupPython] C_element104  label="C_element : 058"  # scripted group (container) (typed FeaturePython)
  n = 1
  ref = C_element
FEATURE [App::DocumentObjectGroupPython] O_element089  label="O_element : 049"  # scripted group (container) (typed FeaturePython)
  n = 3
  ref = O_element
FEATURE [App::DocumentObjectGroupPython] G4_SODIUM_CARBONATE  # scripted group (container) (typed FeaturePython)
  Dunit = g/cm3
  Dvalue = 2.532
  Group = -> [Na_element014,C_element104,O_element089]
  conduct = 2
  density = 1
  expand = 3
  formula = G4_SODIUM_CARBONATE
  name = G4_SODIUM_CARBONATE
  specific = 4
FEATURE [App::DocumentObjectGroupPython] Na_element015  label="Na_element : 1"  # scripted group (container) (typed FeaturePython)
  n = 1
  ref = Na_element
FEATURE [App::DocumentObjectGroupPython] I_element009  label="I_element : 005"  # scripted group (container) (typed FeaturePython)
  n = 1
  ref = I_element
FEATURE [App::DocumentObjectGroupPython] G4_SODIUM_IODIDE  # scripted group (container) (typed FeaturePython)
  Dunit = g/cm3
  Dvalue = 3.667
  Group = -> [Na_element015,I_element009]
  conduct = 2
  density = 1
  expand = 3
  formula = G4_SODIUM_IODIDE
  name = G4_SODIUM_IODIDE
  specific = 4
FEATURE [App::DocumentObjectGroupPython] Na_element016  label="Na_element : 003"  # scripted group (container) (typed FeaturePython)
  n = 2
  ref = Na_element
FEATURE [App::DocumentObjectGroupPython] O_element090  label="O_element : 050"  # scripted group (container) (typed FeaturePython)
  n = 1
  ref = O_element
FEATURE [App::DocumentObjectGroupPython] G4_SODIUM_MONOXIDE  # scripted group (container) (typed FeaturePython)
  Dunit = g/cm3
  Dvalue = 2.27
  Group = -> [Na_element016,O_element090]
  conduct = 2
  density = 1
  expand = 3
  formula = G4_SODIUM_MONOXIDE
  name = G4_SODIUM_MONOXIDE
  specific = 4
FEATURE [App::DocumentObjectGroupPython] Na_element017  label="Na_element : 004"  # scripted group (container) (typed FeaturePython)
  n = 1
  ref = Na_element
FEATURE [App::DocumentObjectGroupPython] N_element040  label="N_element : 018"  # scripted group (container) (typed FeaturePython)
  n = 1
  ref = N_element
FEATURE [App::DocumentObjectGroupPython] O_element091  label="O_element : 051"  # scripted group (container) (typed FeaturePython)
  n = 3
  ref = O_element
FEATURE [App::DocumentObjectGroupPython] G4_SODIUM_NITRATE  # scripted group (container) (typed FeaturePython)
  Dunit = g/cm3
  Dvalue = 2.261
  Group = -> [Na_element017,N_element040,O_element091]
  conduct = 2
  density = 1
  expand = 3
  formula = G4_SODIUM_NITRATE
  name = G4_SODIUM_NITRATE
  specific = 4
FEATURE [App::DocumentObjectGroupPython] C_element105  label="C_element : 059"  # scripted group (container) (typed FeaturePython)
  n = 14
  ref = C_element
FEATURE [App::DocumentObjectGroupPython] H_element096  label="H_element : 053"  # scripted group (container) (typed FeaturePython)
  n = 12
  ref = H_element
FEATURE [App::DocumentObjectGroupPython] G4_STILBENE  # scripted group (container) (typed FeaturePython)
  Dunit = g/cm3
  Dvalue = 0.9707
  Group = -> [C_element105,H_element096]
  conduct = 2
  density = 1
  expand = 3
  formula = G4_STILBENE
  name = G4_STILBENE
  specific = 4
FEATURE [App::DocumentObjectGroupPython] C_element106  label="C_element : 12"  # scripted group (container) (typed FeaturePython)
  n = 12
  ref = C_element
FEATURE [App::DocumentObjectGroupPython] H_element097  label="H_element : 22"  # scripted group (container) (typed FeaturePython)
  n = 22
  ref = H_element
FEATURE [App::DocumentObjectGroupPython] O_element092  label="O_element : 11"  # scripted group (container) (typed FeaturePython)
  n = 11
  ref = O_element
FEATURE [App::DocumentObjectGroupPython] G4_SUCROSE  # scripted group (container) (typed FeaturePython)
  Dunit = g/cm3
  Dvalue = 1.5805
  Group = -> [C_element106,H_element097,O_element092]
  conduct = 2
  density = 1
  expand = 3
  formula = G4_SUCROSE
  name = G4_SUCROSE
  specific = 4
FEATURE [App::DocumentObjectGroupPython] C_element107  label="C_element : 18"  # scripted group (container) (typed FeaturePython)
  n = 18
  ref = C_element
FEATURE [App::DocumentObjectGroupPython] H_element098  label="H_element : 054"  # scripted group (container) (typed FeaturePython)
  n = 14
  ref = H_element
FEATURE [App::DocumentObjectGroupPython] G4_TERPHENYL  # scripted group (container) (typed FeaturePython)
  Dunit = g/cm3
  Dvalue = 1.24
  Group = -> [C_element107,H_element098]
  conduct = 2
  density = 1
  expand = 3
  formula = G4_TERPHENYL
  name = G4_TERPHENYL
  specific = 4
FEATURE [App::DocumentObjectGroupPython] H_element099  label="H_element : 0.146"  # scripted group (container) (typed FeaturePython)
  n = 0.106
FEATURE [App::DocumentObjectGroupPython] C_element108  label="C_element : 0.883"  # scripted group (container) (typed FeaturePython)
  n = 0.099
FEATURE [App::DocumentObjectGroupPython] N_element041  label="N_element : 0.020"  # scripted group (container) (typed FeaturePython)
  n = 0.02
FEATURE [App::DocumentObjectGroupPython] O_element093  label="O_element : 0.766"  # scripted group (container) (typed FeaturePython)
  n = 0.766
FEATURE [App::DocumentObjectGroupPython] Na_element018  label="Na_element : 0.101"  # scripted group (container) (typed FeaturePython)
  n = 0.002
FEATURE [App::DocumentObjectGroupPython] P_element010  label="P_element : 0.108"  # scripted group (container) (typed FeaturePython)
  n = 0.001
FEATURE [App::DocumentObjectGroupPython] S_element021  label="S_element : 0.022"  # scripted group (container) (typed FeaturePython)
  n = 0.002
FEATURE [App::DocumentObjectGroupPython] Cl_element024  label="Cl_element : 0.002"  # scripted group (container) (typed FeaturePython)
  n = 0.002
FEATURE [App::DocumentObjectGroupPython] K_element011  label="K_element : 0.017"  # scripted group (container) (typed FeaturePython)
  n = 0.002
FEATURE [App::DocumentObjectGroupPython] G4_TESTIS_ICRP  # scripted group (container) (typed FeaturePython)
  Dunit = g/cm3
  Dvalue = 1.04
  Group = -> [H_element099,C_element108,N_element041,O_element093,Na_element018,P_element010,S_element021,Cl_element024,K_element011]
  conduct = 2
  density = 1
  expand = 3
  formula = G4_TESTIS_ICRP
  name = G4_TESTIS_ICRP
  specific = 4
FEATURE [App::DocumentObjectGroupPython] C_element109  label="C_element : 060"  # scripted group (container) (typed FeaturePython)
  n = 2
  ref = C_element
FEATURE [App::DocumentObjectGroupPython] Cl_element025  label="Cl_element : 012"  # scripted group (container) (typed FeaturePython)
  n = 4
  ref = Cl_element
FEATURE [App::DocumentObjectGroupPython] G4_TETRACHLOROETHYLENE  # scripted group (container) (typed FeaturePython)
  Dunit = g/cm3
  Dvalue = 1.625
  Group = -> [C_element109,Cl_element025]
  conduct = 2
  density = 1
  expand = 3
  formula = G4_TETRACHLOROETHYLENE
  name = G4_TETRACHLOROETHYLENE
  specific = 4
FEATURE [App::DocumentObjectGroupPython] Tl_element001  label="Tl_element : 1"  # scripted group (container) (typed FeaturePython)
  n = 1
  ref = Tl_element
FEATURE [App::DocumentObjectGroupPython] Cl_element026  label="Cl_element : 013"  # scripted group (container) (typed FeaturePython)
  n = 1
  ref = Cl_element
FEATURE [App::DocumentObjectGroupPython] G4_THALLIUM_CHLORIDE  # scripted group (container) (typed FeaturePython)
  Dunit = g/cm3
  Dvalue = 7.004
  Group = -> [Tl_element001,Cl_element026]
  conduct = 2
  density = 1
  expand = 3
  formula = G4_THALLIUM_CHLORIDE
  name = G4_THALLIUM_CHLORIDE
  specific = 4
FEATURE [App::DocumentObjectGroupPython] H_element100  label="H_element : 0.147"  # scripted group (container) (typed FeaturePython)
  n = 0.105
FEATURE [App::DocumentObjectGroupPython] C_element110  label="C_element : 0.256"  # scripted group (container) (typed FeaturePython)
  n = 0.256
FEATURE [App::DocumentObjectGroupPython] N_element042  label="N_element : 0.760"  # scripted group (container) (typed FeaturePython)
  n = 0.027
FEATURE [App::DocumentObjectGroupPython] O_element094  label="O_element : 0.602"  # scripted group (container) (typed FeaturePython)
  n = 0.602
FEATURE [App::DocumentObjectGroupPython] Na_element019  label="Na_element : 0.102"  # scripted group (container) (typed FeaturePython)
  n = 0.001
FEATURE [App::DocumentObjectGroupPython] P_element011  label="P_element : 0.109"  # scripted group (container) (typed FeaturePython)
  n = 0.002
FEATURE [App::DocumentObjectGroupPython] S_element022  label="S_element : 0.023"  # scripted group (container) (typed FeaturePython)
  n = 0.003
FEATURE [App::DocumentObjectGroupPython] Cl_element027  label="Cl_element : 0.591"  # scripted group (container) (typed FeaturePython)
  n = 0.002
FEATURE [App::DocumentObjectGroupPython] K_element012  label="K_element : 0.018"  # scripted group (container) (typed FeaturePython)
  n = 0.002
FEATURE [App::DocumentObjectGroupPython] G4_TISSUE_SOFT_ICRP  # scripted group (container) (typed FeaturePython)
  Dunit = g/cm3
  Dvalue = 1.03
  Group = -> [H_element100,C_element110,N_element042,O_element094,Na_element019,P_element011,S_element022,Cl_element027,K_element012]
  conduct = 2
  density = 1
  expand = 3
  formula = G4_TISSUE_SOFT_ICRP
  name = G4_TISSUE_SOFT_ICRP
  specific = 4
FEATURE [App::DocumentObjectGroupPython] H_element101  label="H_element : 0.148"  # scripted group (container) (typed FeaturePython)
  n = 0.101
FEATURE [App::DocumentObjectGroupPython] C_element111  label="C_element : 0.111"  # scripted group (container) (typed FeaturePython)
  n = 0.111
FEATURE [App::DocumentObjectGroupPython] N_element043  label="N_element : 0.026"  # scripted group (container) (typed FeaturePython)
  n = 0.026
FEATURE [App::DocumentObjectGroupPython] O_element095  label="O_element : 0.762"  # scripted group (container) (typed FeaturePython)
  n = 0.762
FEATURE [App::DocumentObjectGroupPython] G4_TISSUE_SOFT_ICRU_4  label="G4_TISSUE_SOFT_ICRU-4"  # scripted group (container) (typed FeaturePython)
  Dunit = g/cm3
  Dvalue = 1
  Group = -> [H_element101,C_element111,N_element043,O_element095]
  conduct = 2
  density = 1
  expand = 3
  formula = G4_TISSUE_SOFT_ICRU-4
  name = G4_TISSUE_SOFT_ICRU-4
  specific = 4
FEATURE [App::DocumentObjectGroupPython] H_element102  label="H_element : 0.149"  # scripted group (container) (typed FeaturePython)
  n = 0.101869
FEATURE [App::DocumentObjectGroupPython] C_element112  label="C_element : 0.456"  # scripted group (container) (typed FeaturePython)
  n = 0.456179
FEATURE [App::DocumentObjectGroupPython] N_element044  label="N_element : 0.761"  # scripted group (container) (typed FeaturePython)
  n = 0.035172
FEATURE [App::DocumentObjectGroupPython] O_element096  label="O_element : 0.407"  # scripted group (container) (typed FeaturePython)
  n = 0.40678
FEATURE [App::DocumentObjectGroupPython] G4_TISSUE_METHANE  label="G4_TISSUE-METHANE"  # scripted group (container) (typed FeaturePython)
  Dunit = g/cm3
  Dvalue = 0.00106409
  Group = -> [H_element102,C_element112,N_element044,O_element096]
  conduct = 2
  density = 1
  expand = 3
  formula = G4_TISSUE-METHANE
  name = G4_TISSUE-METHANE
  specific = 4
FEATURE [App::DocumentObjectGroupPython] H_element103  label="H_element : 0.103"  # scripted group (container) (typed FeaturePython)
  n = 0.102672
FEATURE [App::DocumentObjectGroupPython] C_element113  label="C_element : 0.569"  # scripted group (container) (typed FeaturePython)
  n = 0.56894
FEATURE [App::DocumentObjectGroupPython] N_element045  label="N_element : 0.762"  # scripted group (container) (typed FeaturePython)
  n = 0.035022
FEATURE [App::DocumentObjectGroupPython] O_element097  label="O_element : 0.293"  # scripted group (container) (typed FeaturePython)
  n = 0.293366
FEATURE [App::DocumentObjectGroupPython] G4_TISSUE_PROPANE  label="G4_TISSUE-PROPANE"  # scripted group (container) (typed FeaturePython)
  Dunit = g/cm3
  Dvalue = 0.00182628
  Group = -> [H_element103,C_element113,N_element045,O_element097]
  conduct = 2
  density = 1
  expand = 3
  formula = G4_TISSUE-PROPANE
  name = G4_TISSUE-PROPANE
  specific = 4
FEATURE [App::DocumentObjectGroupPython] Ti_element003  label="Ti_element : 1"  # scripted group (container) (typed FeaturePython)
  n = 1
  ref = Ti_element
FEATURE [App::DocumentObjectGroupPython] O_element098  label="O_element : 052"  # scripted group (container) (typed FeaturePython)
  n = 2
  ref = O_element
FEATURE [App::DocumentObjectGroupPython] G4_TITANIUM_DIOXIDE  # scripted group (container) (typed FeaturePython)
  Dunit = g/cm3
  Dvalue = 4.26
  Group = -> [Ti_element003,O_element098]
  conduct = 2
  density = 1
  expand = 3
  formula = G4_TITANIUM_DIOXIDE
  name = G4_TITANIUM_DIOXIDE
  specific = 4
FEATURE [App::DocumentObjectGroupPython] C_element114  label="C_element : 061"  # scripted group (container) (typed FeaturePython)
  n = 7
  ref = C_element
FEATURE [App::DocumentObjectGroupPython] H_element104  label="H_element : 055"  # scripted group (container) (typed FeaturePython)
  n = 8
  ref = H_element
FEATURE [App::DocumentObjectGroupPython] G4_TOLUENE  # scripted group (container) (typed FeaturePython)
  Dunit = g/cm3
  Dvalue = 0.8669
  Group = -> [C_element114,H_element104]
  conduct = 2
  density = 1
  expand = 3
  formula = G4_TOLUENE
  name = G4_TOLUENE
  specific = 4
FEATURE [App::DocumentObjectGroupPython] C_element115  label="C_element : 062"  # scripted group (container) (typed FeaturePython)
  n = 2
  ref = C_element
FEATURE [App::DocumentObjectGroupPython] H_element105  label="H_element : 056"  # scripted group (container) (typed FeaturePython)
  n = 1
  ref = H_element
FEATURE [App::DocumentObjectGroupPython] Cl_element028  label="Cl_element : 014"  # scripted group (container) (typed FeaturePython)
  n = 3
  ref = Cl_element
FEATURE [App::DocumentObjectGroupPython] G4_TRICHLOROETHYLENE  # scripted group (container) (typed FeaturePython)
  Dunit = g/cm3
  Dvalue = 1.46
  Group = -> [C_element115,H_element105,Cl_element028]
  conduct = 2
  density = 1
  expand = 3
  formula = G4_TRICHLOROETHYLENE
  name = G4_TRICHLOROETHYLENE
  specific = 4
FEATURE [App::DocumentObjectGroupPython] C_element116  label="C_element : 063"  # scripted group (container) (typed FeaturePython)
  n = 6
  ref = C_element
FEATURE [App::DocumentObjectGroupPython] H_element106  label="H_element : 15"  # scripted group (container) (typed FeaturePython)
  n = 15
  ref = H_element
FEATURE [App::DocumentObjectGroupPython] O_element099  label="O_element : 053"  # scripted group (container) (typed FeaturePython)
  n = 4
  ref = O_element
FEATURE [App::DocumentObjectGroupPython] P_element012  label="P_element : 1"  # scripted group (container) (typed FeaturePython)
  n = 1
  ref = P_element
FEATURE [App::DocumentObjectGroupPython] G4_TRIETHYL_PHOSPHATE  # scripted group (container) (typed FeaturePython)
  Dunit = g/cm3
  Dvalue = 1.07
  Group = -> [C_element116,H_element106,O_element099,P_element012]
  conduct = 2
  density = 1
  expand = 3
  formula = G4_TRIETHYL_PHOSPHATE
  name = G4_TRIETHYL_PHOSPHATE
  specific = 4
FEATURE [App::DocumentObjectGroupPython] W_element003  label="W_element : 003"  # scripted group (container) (typed FeaturePython)
  n = 1
  ref = W_element
FEATURE [App::DocumentObjectGroupPython] F_element017  label="F_element : 6"  # scripted group (container) (typed FeaturePython)
  n = 6
  ref = F_element
FEATURE [App::DocumentObjectGroupPython] G4_TUNGSTEN_HEXAFLUORIDE  # scripted group (container) (typed FeaturePython)
  Dunit = g/cm3
  Dvalue = 2.4
  Group = -> [W_element003,F_element017]
  conduct = 2
  density = 1
  expand = 3
  formula = G4_TUNGSTEN_HEXAFLUORIDE
  name = G4_TUNGSTEN_HEXAFLUORIDE
  specific = 4
FEATURE [App::DocumentObjectGroupPython] U_element001  label="U_element : 1"  # scripted group (container) (typed FeaturePython)
  n = 1
  ref = U_element
FEATURE [App::DocumentObjectGroupPython] C_element117  label="C_element : 064"  # scripted group (container) (typed FeaturePython)
  n = 2
  ref = C_element
FEATURE [App::DocumentObjectGroupPython] G4_URANIUM_DICARBIDE  # scripted group (container) (typed FeaturePython)
  Dunit = g/cm3
  Dvalue = 11.28
  Group = -> [U_element001,C_element117]
  conduct = 2
  density = 1
  expand = 3
  formula = G4_URANIUM_DICARBIDE
  name = G4_URANIUM_DICARBIDE
  specific = 4
FEATURE [App::DocumentObjectGroupPython] U_element002  label="U_element : 002"  # scripted group (container) (typed FeaturePython)
  n = 1
  ref = U_element
FEATURE [App::DocumentObjectGroupPython] C_element118  label="C_element : 065"  # scripted group (container) (typed FeaturePython)
  n = 1
  ref = C_element
FEATURE [App::DocumentObjectGroupPython] G4_URANIUM_MONOCARBIDE  # scripted group (container) (typed FeaturePython)
  Dunit = g/cm3
  Dvalue = 13.63
  Group = -> [U_element002,C_element118]
  conduct = 2
  density = 1
  expand = 3
  formula = G4_URANIUM_MONOCARBIDE
  name = G4_URANIUM_MONOCARBIDE
  specific = 4
FEATURE [App::DocumentObjectGroupPython] U_element003  label="U_element : 003"  # scripted group (container) (typed FeaturePython)
  n = 1
  ref = U_element
FEATURE [App::DocumentObjectGroupPython] O_element100  label="O_element : 054"  # scripted group (container) (typed FeaturePython)
  n = 2
  ref = O_element
FEATURE [App::DocumentObjectGroupPython] G4_URANIUM_OXIDE  # scripted group (container) (typed FeaturePython)
  Dunit = g/cm3
  Dvalue = 10.96
  Group = -> [U_element003,O_element100]
  conduct = 2
  density = 1
  expand = 3
  formula = G4_URANIUM_OXIDE
  name = G4_URANIUM_OXIDE
  specific = 4
FEATURE [App::DocumentObjectGroupPython] C_element119  label="C_element : 066"  # scripted group (container) (typed FeaturePython)
  n = 1
  ref = C_element
FEATURE [App::DocumentObjectGroupPython] H_element107  label="H_element : 057"  # scripted group (container) (typed FeaturePython)
  n = 4
  ref = H_element
FEATURE [App::DocumentObjectGroupPython] N_element046  label="N_element : 019"  # scripted group (container) (typed FeaturePython)
  n = 2
  ref = N_element
FEATURE [App::DocumentObjectGroupPython] O_element101  label="O_element : 055"  # scripted group (container) (typed FeaturePython)
  n = 1
  ref = O_element
FEATURE [App::DocumentObjectGroupPython] G4_UREA  # scripted group (container) (typed FeaturePython)
  Dunit = g/cm3
  Dvalue = 1.323
  Group = -> [C_element119,H_element107,N_element046,O_element101]
  conduct = 2
  density = 1
  expand = 3
  formula = G4_UREA
  name = G4_UREA
  specific = 4
FEATURE [App::DocumentObjectGroupPython] C_element120  label="C_element : 067"  # scripted group (container) (typed FeaturePython)
  n = 5
  ref = C_element
FEATURE [App::DocumentObjectGroupPython] H_element108  label="H_element : 058"  # scripted group (container) (typed FeaturePython)
  n = 11
  ref = H_element
FEATURE [App::DocumentObjectGroupPython] N_element047  label="N_element : 020"  # scripted group (container) (typed FeaturePython)
  n = 1
  ref = N_element
FEATURE [App::DocumentObjectGroupPython] O_element102  label="O_element : 056"  # scripted group (container) (typed FeaturePython)
  n = 2
  ref = O_element
FEATURE [App::DocumentObjectGroupPython] G4_VALINE  # scripted group (container) (typed FeaturePython)
  Dunit = g/cm3
  Dvalue = 1.23
  Group = -> [C_element120,H_element108,N_element047,O_element102]
  conduct = 2
  density = 1
  expand = 3
  formula = G4_VALINE
  name = G4_VALINE
  specific = 4
FEATURE [App::DocumentObjectGroupPython] H_element109  label="H_element : 0.009"  # scripted group (container) (typed FeaturePython)
  n = 0.009417
FEATURE [App::DocumentObjectGroupPython] C_element121  label="C_element : 0.281"  # scripted group (container) (typed FeaturePython)
  n = 0.280555
FEATURE [App::DocumentObjectGroupPython] F_element018  label="F_element : 0.710"  # scripted group (container) (typed FeaturePython)
  n = 0.710028
FEATURE [App::DocumentObjectGroupPython] G4_VITON  # scripted group (container) (typed FeaturePython)
  Dunit = g/cm3
  Dvalue = 1.8
  Group = -> [H_element109,C_element121,F_element018]
  conduct = 2
  density = 1
  expand = 3
  formula = G4_VITON
  name = G4_VITON
  specific = 4
FEATURE [App::DocumentObjectGroupPython] H_element110  label="H_element : 059"  # scripted group (container) (typed FeaturePython)
  n = 2
  ref = H_element
FEATURE [App::DocumentObjectGroupPython] O_element103  label="O_element : 057"  # scripted group (container) (typed FeaturePython)
  n = 1
  ref = O_element
FEATURE [App::DocumentObjectGroupPython] G4_WATER  # scripted group (container) (typed FeaturePython)
  Dunit = g/cm3
  Dvalue = 1
  Group = -> [H_element110,O_element103]
  conduct = 2
  density = 1
  expand = 3
  formula = G4_WATER
  name = G4_WATER
  specific = 4
FEATURE [App::DocumentObjectGroupPython] H_element111  label="H_element : 060"  # scripted group (container) (typed FeaturePython)
  n = 2
  ref = H_element
FEATURE [App::DocumentObjectGroupPython] O_element104  label="O_element : 058"  # scripted group (container) (typed FeaturePython)
  n = 1
  ref = O_element
FEATURE [App::DocumentObjectGroupPython] G4_WATER_VAPOR  # scripted group (container) (typed FeaturePython)
  Dunit = g/cm3
  Dvalue = 0.000756182
  Group = -> [H_element111,O_element104]
  conduct = 2
  density = 1
  expand = 3
  formula = G4_WATER_VAPOR
  name = G4_WATER_VAPOR
  specific = 4
FEATURE [App::DocumentObjectGroupPython] C_element122  label="C_element : 068"  # scripted group (container) (typed FeaturePython)
  n = 8
  ref = C_element
FEATURE [App::DocumentObjectGroupPython] H_element112  label="H_element : 061"  # scripted group (container) (typed FeaturePython)
  n = 10
  ref = H_element
FEATURE [App::DocumentObjectGroupPython] G4_XYLENE  # scripted group (container) (typed FeaturePython)
  Dunit = g/cm3
  Dvalue = 0.87
  Group = -> [C_element122,H_element112]
  conduct = 2
  density = 1
  expand = 3
  formula = G4_XYLENE
  name = G4_XYLENE
  specific = 4
FEATURE [App::DocumentObjectGroupPython] C_element123  label="C_element : 069"  # scripted group (container) (typed FeaturePython)
  n = 1
  ref = C_element
FEATURE [App::DocumentObjectGroupPython] G4_GRAPHITE  # scripted group (container) (typed FeaturePython)
  Dunit = g/cm3
  Dvalue = 2.21
  Group = -> [C_element123]
  conduct = 2
  density = 1
  expand = 3
  formula = G4_GRAPHITE
  name = G4_GRAPHITE
  specific = 4
FEATURE [App::DocumentObjectGroupPython] NIST  # scripted group (container) (typed FeaturePython)
  Group = -> [G4_A_150_TISSUE,G4_ACETONE,G4_ACETYLENE,G4_ADENINE,G4_ADIPOSE_TISSUE_ICRP,G4_AIR,G4_ALANINE,G4_ALUMINUM_OXIDE,G4_AMBER,G4_AMMONIA,G4_ANILINE,G4_ANTHRACENE,G4_B_100_BONE,G4_BAKELITE,G4_BARIUM_FLUORIDE,G4_BARIUM_SULFATE,G4_BENZENE,G4_BERYLLIUM_OXIDE,G4_BGO,G4_BLOOD_ICRP,G4_BONE_COMPACT_ICRU,G4_BONE_CORTICAL_ICRP,G4_BORON_CARBIDE,G4_BORON_OXIDE,G4_BRAIN_ICRP,G4_BUTANE,G4_N_BUTYL_ALCOHOL,G4_C_552,+152 more]
FEATURE [App::DocumentObjectGroupPython] H_element113  label="H_element : 062"  # scripted group (container) (typed FeaturePython)
  n = 1
  ref = H_element
FEATURE [App::DocumentObjectGroupPython] G4_H  # scripted group (container) (typed FeaturePython)
  Dunit = g/cm3
  Dvalue = 8.3748e-05
  Group = -> [H_element113]
  conduct = 2
  density = 1
  expand = 3
  formula = H
  name = G4_H
  specific = 4
FEATURE [App::DocumentObjectGroupPython] He_element001  label="He_element : 1"  # scripted group (container) (typed FeaturePython)
  n = 1
  ref = He_element
FEATURE [App::DocumentObjectGroupPython] G4_He  # scripted group (container) (typed FeaturePython)
  Dunit = g/cm3
  Dvalue = 0.000166322
  Group = -> [He_element001]
  conduct = 2
  density = 1
  expand = 3
  formula = He
  name = G4_He
  specific = 4
FEATURE [App::DocumentObjectGroupPython] Li_element008  label="Li_element : 008"  # scripted group (container) (typed FeaturePython)
  n = 1
  ref = Li_element
FEATURE [App::DocumentObjectGroupPython] G4_Li  # scripted group (container) (typed FeaturePython)
  Dunit = g/cm3
  Dvalue = 0.534
  Group = -> [Li_element008]
  conduct = 2
  density = 1
  expand = 3
  formula = Li
  name = G4_Li
  specific = 4
FEATURE [App::DocumentObjectGroupPython] Be_element002  label="Be_element : 002"  # scripted group (container) (typed FeaturePython)
  n = 1
  ref = Be_element
FEATURE [App::DocumentObjectGroupPython] G4_Be  # scripted group (container) (typed FeaturePython)
  Dunit = g/cm3
  Dvalue = 1.848
  Group = -> [Be_element002]
  conduct = 2
  density = 1
  expand = 3
  formula = Be
  name = G4_Be
  specific = 4
FEATURE [App::DocumentObjectGroupPython] B_element007  label="B_element : 007"  # scripted group (container) (typed FeaturePython)
  n = 1
  ref = B_element
FEATURE [App::DocumentObjectGroupPython] G4_B  # scripted group (container) (typed FeaturePython)
  Dunit = g/cm3
  Dvalue = 2.37
  Group = -> [B_element007]
  conduct = 2
  density = 1
  expand = 3
  formula = B
  name = G4_B
  specific = 4
FEATURE [App::DocumentObjectGroupPython] C_element124  label="C_element : 070"  # scripted group (container) (typed FeaturePython)
  n = 1
  ref = C_element
FEATURE [App::DocumentObjectGroupPython] G4_C  # scripted group (container) (typed FeaturePython)
  Dunit = g/cm3
  Dvalue = 2
  Group = -> [C_element124]
  conduct = 2
  density = 1
  expand = 3
  formula = C
  name = G4_C
  specific = 4
FEATURE [App::DocumentObjectGroupPython] N_element048  label="N_element : 021"  # scripted group (container) (typed FeaturePython)
  n = 1
  ref = N_element
FEATURE [App::DocumentObjectGroupPython] G4_N  # scripted group (container) (typed FeaturePython)
  Dunit = g/cm3
  Dvalue = 0.0011652
  Group = -> [N_element048]
  conduct = 2
  density = 1
  expand = 3
  formula = N
  name = G4_N
  specific = 4
FEATURE [App::DocumentObjectGroupPython] O_element105  label="O_element : 059"  # scripted group (container) (typed FeaturePython)
  n = 1
  ref = O_element
FEATURE [App::DocumentObjectGroupPython] G4_O  # scripted group (container) (typed FeaturePython)
  Dunit = g/cm3
  Dvalue = 0.00133151
  Group = -> [O_element105]
  conduct = 2
  density = 1
  expand = 3
  formula = O
  name = G4_O
  specific = 4
FEATURE [App::DocumentObjectGroupPython] F_element019  label="F_element : 008"  # scripted group (container) (typed FeaturePython)
  n = 1
  ref = F_element
FEATURE [App::DocumentObjectGroupPython] G4_F  # scripted group (container) (typed FeaturePython)
  Dunit = g/cm3
  Dvalue = 0.00158029
  Group = -> [F_element019]
  conduct = 2
  density = 1
  expand = 3
  formula = F
  name = G4_F
  specific = 4
FEATURE [App::DocumentObjectGroupPython] Ne_element001  label="Ne_element : 1"  # scripted group (container) (typed FeaturePython)
  n = 1
  ref = Ne_element
FEATURE [App::DocumentObjectGroupPython] G4_Ne  # scripted group (container) (typed FeaturePython)
  Dunit = g/cm3
  Dvalue = 0.000838505
  Group = -> [Ne_element001]
  conduct = 2
  density = 1
  expand = 3
  formula = Ne
  name = G4_Ne
  specific = 4
FEATURE [App::DocumentObjectGroupPython] Na_element020  label="Na_element : 005"  # scripted group (container) (typed FeaturePython)
  n = 1
  ref = Na_element
FEATURE [App::DocumentObjectGroupPython] G4_Na  # scripted group (container) (typed FeaturePython)
  Dunit = g/cm3
  Dvalue = 0.971
  Group = -> [Na_element020]
  conduct = 2
  density = 1
  expand = 3
  formula = Na
  name = G4_Na
  specific = 4
FEATURE [App::DocumentObjectGroupPython] Mg_element011  label="Mg_element : 005"  # scripted group (container) (typed FeaturePython)
  n = 1
  ref = Mg_element
FEATURE [App::DocumentObjectGroupPython] G4_Mg  # scripted group (container) (typed FeaturePython)
  Dunit = g/cm3
  Dvalue = 1.74
  Group = -> [Mg_element011]
  conduct = 2
  density = 1
  expand = 3
  formula = Mg
  name = G4_Mg
  specific = 4
FEATURE [App::DocumentObjectGroupPython] Al_element004  label="Al_element : 1"  # scripted group (container) (typed FeaturePython)
  n = 1
  ref = Al_element
FEATURE [App::DocumentObjectGroupPython] G4_Al  # scripted group (container) (typed FeaturePython)
  Dunit = g/cm3
  Dvalue = 2.699
  Group = -> [Al_element004]
  conduct = 2
  density = 1
  expand = 3
  formula = Al
  name = G4_Al
  specific = 4
FEATURE [App::DocumentObjectGroupPython] Si_element007  label="Si_element : 002"  # scripted group (container) (typed FeaturePython)
  n = 1
  ref = Si_element
FEATURE [App::DocumentObjectGroupPython] G4_Si  # scripted group (container) (typed FeaturePython)
  Dunit = g/cm3
  Dvalue = 2.33
  Group = -> [Si_element007]
  conduct = 2
  density = 1
  expand = 3
  formula = Si
  name = G4_Si
  specific = 4
FEATURE [App::DocumentObjectGroupPython] P_element013  label="P_element : 002"  # scripted group (container) (typed FeaturePython)
  n = 1
  ref = P_element
FEATURE [App::DocumentObjectGroupPython] G4_P  # scripted group (container) (typed FeaturePython)
  Dunit = g/cm3
  Dvalue = 2.2
  Group = -> [P_element013]
  conduct = 2
  density = 1
  expand = 3
  formula = P
  name = G4_P
  specific = 4
FEATURE [App::DocumentObjectGroupPython] S_element023  label="S_element : 007"  # scripted group (container) (typed FeaturePython)
  n = 1
  ref = S_element
FEATURE [App::DocumentObjectGroupPython] G4_S  # scripted group (container) (typed FeaturePython)
  Dunit = g/cm3
  Dvalue = 2
  Group = -> [S_element023]
  conduct = 2
  density = 1
  expand = 3
  formula = S
  name = G4_S
  specific = 4
FEATURE [App::DocumentObjectGroupPython] Cl_element029  label="Cl_element : 015"  # scripted group (container) (typed FeaturePython)
  n = 1
  ref = Cl_element
FEATURE [App::DocumentObjectGroupPython] G4_Cl  # scripted group (container) (typed FeaturePython)
  Dunit = g/cm3
  Dvalue = 0.00299473
  Group = -> [Cl_element029]
  conduct = 2
  density = 1
  expand = 3
  formula = Cl
  name = G4_Cl
  specific = 4
FEATURE [App::DocumentObjectGroupPython] Ar_element002  label="Ar_element : 1"  # scripted group (container) (typed FeaturePython)
  n = 1
  ref = Ar_element
FEATURE [App::DocumentObjectGroupPython] G4_Ar  # scripted group (container) (typed FeaturePython)
  Dunit = g/cm3
  Dvalue = 0.00166201
  Group = -> [Ar_element002]
  conduct = 2
  density = 1
  expand = 3
  formula = Ar
  name = G4_Ar
  specific = 4
FEATURE [App::DocumentObjectGroupPython] K_element013  label="K_element : 003"  # scripted group (container) (typed FeaturePython)
  n = 1
  ref = K_element
FEATURE [App::DocumentObjectGroupPython] G4_K  # scripted group (container) (typed FeaturePython)
  Dunit = g/cm3
  Dvalue = 0.862
  Group = -> [K_element013]
  conduct = 2
  density = 1
  expand = 3
  formula = K
  name = G4_K
  specific = 4
FEATURE [App::DocumentObjectGroupPython] Ca_element014  label="Ca_element : 007"  # scripted group (container) (typed FeaturePython)
  n = 1
  ref = Ca_element
FEATURE [App::DocumentObjectGroupPython] G4_Ca  # scripted group (container) (typed FeaturePython)
  Dunit = g/cm3
  Dvalue = 1.55
  Group = -> [Ca_element014]
  conduct = 2
  density = 1
  expand = 3
  formula = Ca
  name = G4_Ca
  specific = 4
FEATURE [App::DocumentObjectGroupPython] Sc_element001  label="Sc_element : 1"  # scripted group (container) (typed FeaturePython)
  n = 1
  ref = Sc_element
FEATURE [App::DocumentObjectGroupPython] G4_Sc  # scripted group (container) (typed FeaturePython)
  Dunit = g/cm3
  Dvalue = 2.989
  Group = -> [Sc_element001]
  conduct = 2
  density = 1
  expand = 3
  formula = Sc
  name = G4_Sc
  specific = 4
FEATURE [App::DocumentObjectGroupPython] Ti_element004  label="Ti_element : 002"  # scripted group (container) (typed FeaturePython)
  n = 1
  ref = Ti_element
FEATURE [App::DocumentObjectGroupPython] G4_Ti  # scripted group (container) (typed FeaturePython)
  Dunit = g/cm3
  Dvalue = 4.54
  Group = -> [Ti_element004]
  conduct = 2
  density = 1
  expand = 3
  formula = Ti
  name = G4_Ti
  specific = 4
FEATURE [App::DocumentObjectGroupPython] V_element001  label="V_element : 1"  # scripted group (container) (typed FeaturePython)
  n = 1
  ref = V_element
FEATURE [App::DocumentObjectGroupPython] G4_V  # scripted group (container) (typed FeaturePython)
  Dunit = g/cm3
  Dvalue = 6.11
  Group = -> [V_element001]
  conduct = 2
  density = 1
  expand = 3
  formula = V
  name = G4_V
  specific = 4
FEATURE [App::DocumentObjectGroupPython] Cr_element001  label="Cr_element : 1"  # scripted group (container) (typed FeaturePython)
  n = 1
  ref = Cr_element
FEATURE [App::DocumentObjectGroupPython] G4_Cr  # scripted group (container) (typed FeaturePython)
  Dunit = g/cm3
  Dvalue = 7.18
  Group = -> [Cr_element001]
  conduct = 2
  density = 1
  expand = 3
  formula = Cr
  name = G4_Cr
  specific = 4
FEATURE [App::DocumentObjectGroupPython] Mn_element001  label="Mn_element : 1"  # scripted group (container) (typed FeaturePython)
  n = 1
  ref = Mn_element
FEATURE [App::DocumentObjectGroupPython] G4_Mn  # scripted group (container) (typed FeaturePython)
  Dunit = g/cm3
  Dvalue = 7.44
  Group = -> [Mn_element001]
  conduct = 2
  density = 1
  expand = 3
  formula = Mn
  name = G4_Mn
  specific = 4
FEATURE [App::DocumentObjectGroupPython] Fe_element007  label="Fe_element : 004"  # scripted group (container) (typed FeaturePython)
  n = 1
  ref = Fe_element
FEATURE [App::DocumentObjectGroupPython] G4_Fe  # scripted group (container) (typed FeaturePython)
  Dunit = g/cm3
  Dvalue = 7.874
  Group = -> [Fe_element007]
  conduct = 2
  density = 1
  expand = 3
  formula = Fe
  name = G4_Fe
  specific = 4
FEATURE [App::DocumentObjectGroupPython] Co_element001  label="Co_element : 1"  # scripted group (container) (typed FeaturePython)
  n = 1
  ref = Co_element
FEATURE [App::DocumentObjectGroupPython] G4_Co  # scripted group (container) (typed FeaturePython)
  Dunit = g/cm3
  Dvalue = 8.9
  Group = -> [Co_element001]
  conduct = 2
  density = 1
  expand = 3
  formula = Co
  name = G4_Co
  specific = 4
FEATURE [App::DocumentObjectGroupPython] Ni_element001  label="Ni_element : 1"  # scripted group (container) (typed FeaturePython)
  n = 1
  ref = Ni_element
FEATURE [App::DocumentObjectGroupPython] G4_Ni  # scripted group (container) (typed FeaturePython)
  Dunit = g/cm3
  Dvalue = 8.902
  Group = -> [Ni_element001]
  conduct = 2
  density = 1
  expand = 3
  formula = Ni
  name = G4_Ni
  specific = 4
FEATURE [App::DocumentObjectGroupPython] Cu_element001  label="Cu_element : 1"  # scripted group (container) (typed FeaturePython)
  n = 1
  ref = Cu_element
FEATURE [App::DocumentObjectGroupPython] G4_Cu  # scripted group (container) (typed FeaturePython)
  Dunit = g/cm3
  Dvalue = 8.96
  Group = -> [Cu_element001]
  conduct = 2
  density = 1
  expand = 3
  formula = Cu
  name = G4_Cu
  specific = 4
FEATURE [App::DocumentObjectGroupPython] Zn_element001  label="Zn_element : 1"  # scripted group (container) (typed FeaturePython)
  n = 1
  ref = Zn_element
FEATURE [App::DocumentObjectGroupPython] G4_Zn  # scripted group (container) (typed FeaturePython)
  Dunit = g/cm3
  Dvalue = 7.133
  Group = -> [Zn_element001]
  conduct = 2
  density = 1
  expand = 3
  formula = Zn
  name = G4_Zn
  specific = 4
FEATURE [App::DocumentObjectGroupPython] Ga_element002  label="Ga_element : 002"  # scripted group (container) (typed FeaturePython)
  n = 1
  ref = Ga_element
FEATURE [App::DocumentObjectGroupPython] G4_Ga  # scripted group (container) (typed FeaturePython)
  Dunit = g/cm3
  Dvalue = 5.904
  Group = -> [Ga_element002]
  conduct = 2
  density = 1
  expand = 3
  formula = Ga
  name = G4_Ga
  specific = 4
FEATURE [App::DocumentObjectGroupPython] Ge_element002  label="Ge_element : 1"  # scripted group (container) (typed FeaturePython)
  n = 1
  ref = Ge_element
FEATURE [App::DocumentObjectGroupPython] G4_Ge  # scripted group (container) (typed FeaturePython)
  Dunit = g/cm3
  Dvalue = 5.323
  Group = -> [Ge_element002]
  conduct = 2
  density = 1
  expand = 3
  formula = Ge
  name = G4_Ge
  specific = 4
FEATURE [App::DocumentObjectGroupPython] As_element003  label="As_element : 002"  # scripted group (container) (typed FeaturePython)
  n = 1
  ref = As_element
FEATURE [App::DocumentObjectGroupPython] G4_As  # scripted group (container) (typed FeaturePython)
  Dunit = g/cm3
  Dvalue = 5.73
  Group = -> [As_element003]
  conduct = 2
  density = 1
  expand = 3
  formula = As
  name = G4_As
  specific = 4
FEATURE [App::DocumentObjectGroupPython] Se_element001  label="Se_element : 1"  # scripted group (container) (typed FeaturePython)
  n = 1
  ref = Se_element
FEATURE [App::DocumentObjectGroupPython] G4_Se  # scripted group (container) (typed FeaturePython)
  Dunit = g/cm3
  Dvalue = 4.5
  Group = -> [Se_element001]
  conduct = 2
  density = 1
  expand = 3
  formula = Se
  name = G4_Se
  specific = 4
FEATURE [App::DocumentObjectGroupPython] Br_element007  label="Br_element : 004"  # scripted group (container) (typed FeaturePython)
  n = 1
  ref = Br_element
FEATURE [App::DocumentObjectGroupPython] G4_Br  # scripted group (container) (typed FeaturePython)
  Dunit = g/cm3
  Dvalue = 0.0070721
  Group = -> [Br_element007]
  conduct = 2
  density = 1
  expand = 3
  formula = Br
  name = G4_Br
  specific = 4
FEATURE [App::DocumentObjectGroupPython] Kr_element001  label="Kr_element : 1"  # scripted group (container) (typed FeaturePython)
  n = 1
  ref = Kr_element
FEATURE [App::DocumentObjectGroupPython] G4_Kr  # scripted group (container) (typed FeaturePython)
  Dunit = g/cm3
  Dvalue = 0.00347832
  Group = -> [Kr_element001]
  conduct = 2
  density = 1
  expand = 3
  formula = Kr
  name = G4_Kr
  specific = 4
FEATURE [App::DocumentObjectGroupPython] Rb_element001  label="Rb_element : 1"  # scripted group (container) (typed FeaturePython)
  n = 1
  ref = Rb_element
FEATURE [App::DocumentObjectGroupPython] G4_Rb  # scripted group (container) (typed FeaturePython)
  Dunit = g/cm3
  Dvalue = 1.532
  Group = -> [Rb_element001]
  conduct = 2
  density = 1
  expand = 3
  formula = Rb
  name = G4_Rb
  specific = 4
FEATURE [App::DocumentObjectGroupPython] Sr_element001  label="Sr_element : 1"  # scripted group (container) (typed FeaturePython)
  n = 1
  ref = Sr_element
FEATURE [App::DocumentObjectGroupPython] G4_Sr  # scripted group (container) (typed FeaturePython)
  Dunit = g/cm3
  Dvalue = 2.54
  Group = -> [Sr_element001]
  conduct = 2
  density = 1
  expand = 3
  formula = Sr
  name = G4_Sr
  specific = 4
FEATURE [App::DocumentObjectGroupPython] Y_element001  label="Y_element : 1"  # scripted group (container) (typed FeaturePython)
  n = 1
  ref = Y_element
FEATURE [App::DocumentObjectGroupPython] G4_Y  # scripted group (container) (typed FeaturePython)
  Dunit = g/cm3
  Dvalue = 4.469
  Group = -> [Y_element001]
  conduct = 2
  density = 1
  expand = 3
  formula = Y
  name = G4_Y
  specific = 4
FEATURE [App::DocumentObjectGroupPython] Zr_element001  label="Zr_element : 1"  # scripted group (container) (typed FeaturePython)
  n = 1
  ref = Zr_element
FEATURE [App::DocumentObjectGroupPython] G4_Zr  # scripted group (container) (typed FeaturePython)
  Dunit = g/cm3
  Dvalue = 6.506
  Group = -> [Zr_element001]
  conduct = 2
  density = 1
  expand = 3
  formula = Zr
  name = G4_Zr
  specific = 4
FEATURE [App::DocumentObjectGroupPython] Nb_element001  label="Nb_element : 1"  # scripted group (container) (typed FeaturePython)
  n = 1
  ref = Nb_element
FEATURE [App::DocumentObjectGroupPython] G4_Nb  # scripted group (container) (typed FeaturePython)
  Dunit = g/cm3
  Dvalue = 8.57
  Group = -> [Nb_element001]
  conduct = 2
  density = 1
  expand = 3
  formula = Nb
  name = G4_Nb
  specific = 4
FEATURE [App::DocumentObjectGroupPython] Mo_element001  label="Mo_element : 1"  # scripted group (container) (typed FeaturePython)
  n = 1
  ref = Mo_element
FEATURE [App::DocumentObjectGroupPython] G4_Mo  # scripted group (container) (typed FeaturePython)
  Dunit = g/cm3
  Dvalue = 10.22
  Group = -> [Mo_element001]
  conduct = 2
  density = 1
  expand = 3
  formula = Mo
  name = G4_Mo
  specific = 4
FEATURE [App::DocumentObjectGroupPython] Tc_element001  label="Tc_element : 1"  # scripted group (container) (typed FeaturePython)
  n = 1
  ref = Tc_element
FEATURE [App::DocumentObjectGroupPython] G4_Tc  # scripted group (container) (typed FeaturePython)
  Dunit = g/cm3
  Dvalue = 11.5
  Group = -> [Tc_element001]
  conduct = 2
  density = 1
  expand = 3
  formula = Tc
  name = G4_Tc
  specific = 4
FEATURE [App::DocumentObjectGroupPython] Ru_element001  label="Ru_element : 1"  # scripted group (container) (typed FeaturePython)
  n = 1
  ref = Ru_element
FEATURE [App::DocumentObjectGroupPython] G4_Ru  # scripted group (container) (typed FeaturePython)
  Dunit = g/cm3
  Dvalue = 12.41
  Group = -> [Ru_element001]
  conduct = 2
  density = 1
  expand = 3
  formula = Ru
  name = G4_Ru
  specific = 4
FEATURE [App::DocumentObjectGroupPython] Rh_element001  label="Rh_element : 1"  # scripted group (container) (typed FeaturePython)
  n = 1
  ref = Rh_element
FEATURE [App::DocumentObjectGroupPython] G4_Rh  # scripted group (container) (typed FeaturePython)
  Dunit = g/cm3
  Dvalue = 12.41
  Group = -> [Rh_element001]
  conduct = 2
  density = 1
  expand = 3
  formula = Rh
  name = G4_Rh
  specific = 4
FEATURE [App::DocumentObjectGroupPython] Pd_element001  label="Pd_element : 1"  # scripted group (container) (typed FeaturePython)
  n = 1
  ref = Pd_element
FEATURE [App::DocumentObjectGroupPython] G4_Pd  # scripted group (container) (typed FeaturePython)
  Dunit = g/cm3
  Dvalue = 12.02
  Group = -> [Pd_element001]
  conduct = 2
  density = 1
  expand = 3
  formula = Pd
  name = G4_Pd
  specific = 4
FEATURE [App::DocumentObjectGroupPython] Ag_element006  label="Ag_element : 004"  # scripted group (container) (typed FeaturePython)
  n = 1
  ref = Ag_element
FEATURE [App::DocumentObjectGroupPython] G4_Ag  # scripted group (container) (typed FeaturePython)
  Dunit = g/cm3
  Dvalue = 10.5
  Group = -> [Ag_element006]
  conduct = 2
  density = 1
  expand = 3
  formula = Ag
  name = G4_Ag
  specific = 4
FEATURE [App::DocumentObjectGroupPython] Cd_element003  label="Cd_element : 003"  # scripted group (container) (typed FeaturePython)
  n = 1
  ref = Cd_element
FEATURE [App::DocumentObjectGroupPython] G4_Cd  # scripted group (container) (typed FeaturePython)
  Dunit = g/cm3
  Dvalue = 8.65
  Group = -> [Cd_element003]
  conduct = 2
  density = 1
  expand = 3
  formula = Cd
  name = G4_Cd
  specific = 4
FEATURE [App::DocumentObjectGroupPython] In_element001  label="In_element : 1"  # scripted group (container) (typed FeaturePython)
  n = 1
  ref = In_element
FEATURE [App::DocumentObjectGroupPython] G4_In  # scripted group (container) (typed FeaturePython)
  Dunit = g/cm3
  Dvalue = 7.31
  Group = -> [In_element001]
  conduct = 2
  density = 1
  expand = 3
  formula = In
  name = G4_In
  specific = 4
FEATURE [App::DocumentObjectGroupPython] Sn_element001  label="Sn_element : 1"  # scripted group (container) (typed FeaturePython)
  n = 1
  ref = Sn_element
FEATURE [App::DocumentObjectGroupPython] G4_Sn  # scripted group (container) (typed FeaturePython)
  Dunit = g/cm3
  Dvalue = 7.31
  Group = -> [Sn_element001]
  conduct = 2
  density = 1
  expand = 3
  formula = Sn
  name = G4_Sn
  specific = 4
FEATURE [App::DocumentObjectGroupPython] Sb_element001  label="Sb_element : 1"  # scripted group (container) (typed FeaturePython)
  n = 1
  ref = Sb_element
FEATURE [App::DocumentObjectGroupPython] G4_Sb  # scripted group (container) (typed FeaturePython)
  Dunit = g/cm3
  Dvalue = 6.691
  Group = -> [Sb_element001]
  conduct = 2
  density = 1
  expand = 3
  formula = Sb
  name = G4_Sb
  specific = 4
FEATURE [App::DocumentObjectGroupPython] Te_element002  label="Te_element : 002"  # scripted group (container) (typed FeaturePython)
  n = 1
  ref = Te_element
FEATURE [App::DocumentObjectGroupPython] G4_Te  # scripted group (container) (typed FeaturePython)
  Dunit = g/cm3
  Dvalue = 6.24
  Group = -> [Te_element002]
  conduct = 2
  density = 1
  expand = 3
  formula = Te
  name = G4_Te
  specific = 4
FEATURE [App::DocumentObjectGroupPython] I_element010  label="I_element : 006"  # scripted group (container) (typed FeaturePython)
  n = 1
  ref = I_element
FEATURE [App::DocumentObjectGroupPython] G4_I  # scripted group (container) (typed FeaturePython)
  Dunit = g/cm3
  Dvalue = 4.93
  Group = -> [I_element010]
  conduct = 2
  density = 1
  expand = 3
  formula = I
  name = G4_I
  specific = 4
FEATURE [App::DocumentObjectGroupPython] Xe_element001  label="Xe_element : 1"  # scripted group (container) (typed FeaturePython)
  n = 1
  ref = Xe_element
FEATURE [App::DocumentObjectGroupPython] G4_Xe  # scripted group (container) (typed FeaturePython)
  Dunit = g/cm3
  Dvalue = 0.00548536
  Group = -> [Xe_element001]
  conduct = 2
  density = 1
  expand = 3
  formula = Xe
  name = G4_Xe
  specific = 4
FEATURE [App::DocumentObjectGroupPython] Cs_element003  label="Cs_element : 003"  # scripted group (container) (typed FeaturePython)
  n = 1
  ref = Cs_element
FEATURE [App::DocumentObjectGroupPython] G4_Cs  # scripted group (container) (typed FeaturePython)
  Dunit = g/cm3
  Dvalue = 1.873
  Group = -> [Cs_element003]
  conduct = 2
  density = 1
  expand = 3
  formula = Cs
  name = G4_Cs
  specific = 4
FEATURE [App::DocumentObjectGroupPython] Ba_element003  label="Ba_element : 003"  # scripted group (container) (typed FeaturePython)
  n = 1
  ref = Ba_element
FEATURE [App::DocumentObjectGroupPython] G4_Ba  # scripted group (container) (typed FeaturePython)
  Dunit = g/cm3
  Dvalue = 3.5
  Group = -> [Ba_element003]
  conduct = 2
  density = 1
  expand = 3
  formula = Ba
  name = G4_Ba
  specific = 4
FEATURE [App::DocumentObjectGroupPython] La_element003  label="La_element : 003"  # scripted group (container) (typed FeaturePython)
  n = 1
  ref = La_element
FEATURE [App::DocumentObjectGroupPython] G4_La  # scripted group (container) (typed FeaturePython)
  Dunit = g/cm3
  Dvalue = 6.154
  Group = -> [La_element003]
  conduct = 2
  density = 1
  expand = 3
  formula = La
  name = G4_La
  specific = 4
FEATURE [App::DocumentObjectGroupPython] Ce_element002  label="Ce_element : 1"  # scripted group (container) (typed FeaturePython)
  n = 1
  ref = Ce_element
FEATURE [App::DocumentObjectGroupPython] G4_Ce  # scripted group (container) (typed FeaturePython)
  Dunit = g/cm3
  Dvalue = 6.657
  Group = -> [Ce_element002]
  conduct = 2
  density = 1
  expand = 3
  formula = Ce
  name = G4_Ce
  specific = 4
FEATURE [App::DocumentObjectGroupPython] Pr_element001  label="Pr_element : 1"  # scripted group (container) (typed FeaturePython)
  n = 1
  ref = Pr_element
FEATURE [App::DocumentObjectGroupPython] G4_Pr  # scripted group (container) (typed FeaturePython)
  Dunit = g/cm3
  Dvalue = 6.71
  Group = -> [Pr_element001]
  conduct = 2
  density = 1
  expand = 3
  formula = Pr
  name = G4_Pr
  specific = 4
FEATURE [App::DocumentObjectGroupPython] Nd_element001  label="Nd_element : 1"  # scripted group (container) (typed FeaturePython)
  n = 1
  ref = Nd_element
FEATURE [App::DocumentObjectGroupPython] G4_Nd  # scripted group (container) (typed FeaturePython)
  Dunit = g/cm3
  Dvalue = 6.9
  Group = -> [Nd_element001]
  conduct = 2
  density = 1
  expand = 3
  formula = Nd
  name = G4_Nd
  specific = 4
FEATURE [App::DocumentObjectGroupPython] Pm_element001  label="Pm_element : 1"  # scripted group (container) (typed FeaturePython)
  n = 1
  ref = Pm_element
FEATURE [App::DocumentObjectGroupPython] G4_Pm  # scripted group (container) (typed FeaturePython)
  Dunit = g/cm3
  Dvalue = 7.22
  Group = -> [Pm_element001]
  conduct = 2
  density = 1
  expand = 3
  formula = Pm
  name = G4_Pm
  specific = 4
FEATURE [App::DocumentObjectGroupPython] Sm_element001  label="Sm_element : 1"  # scripted group (container) (typed FeaturePython)
  n = 1
  ref = Sm_element
FEATURE [App::DocumentObjectGroupPython] G4_Sm  # scripted group (container) (typed FeaturePython)
  Dunit = g/cm3
  Dvalue = 7.46
  Group = -> [Sm_element001]
  conduct = 2
  density = 1
  expand = 3
  formula = Sm
  name = G4_Sm
  specific = 4
FEATURE [App::DocumentObjectGroupPython] Eu_element001  label="Eu_element : 1"  # scripted group (container) (typed FeaturePython)
  n = 1
  ref = Eu_element
FEATURE [App::DocumentObjectGroupPython] G4_Eu  # scripted group (container) (typed FeaturePython)
  Dunit = g/cm3
  Dvalue = 5.243
  Group = -> [Eu_element001]
  conduct = 2
  density = 1
  expand = 3
  formula = Eu
  name = G4_Eu
  specific = 4
FEATURE [App::DocumentObjectGroupPython] Gd_element002  label="Gd_element : 1"  # scripted group (container) (typed FeaturePython)
  n = 1
  ref = Gd_element
FEATURE [App::DocumentObjectGroupPython] G4_Gd  # scripted group (container) (typed FeaturePython)
  Dunit = g/cm3
  Dvalue = 7.9004
  Group = -> [Gd_element002]
  conduct = 2
  density = 1
  expand = 3
  formula = Gd
  name = G4_Gd
  specific = 4
FEATURE [App::DocumentObjectGroupPython] Tb_element001  label="Tb_element : 1"  # scripted group (container) (typed FeaturePython)
  n = 1
  ref = Tb_element
FEATURE [App::DocumentObjectGroupPython] G4_Tb  # scripted group (container) (typed FeaturePython)
  Dunit = g/cm3
  Dvalue = 8.229
  Group = -> [Tb_element001]
  conduct = 2
  density = 1
  expand = 3
  formula = Tb
  name = G4_Tb
  specific = 4
FEATURE [App::DocumentObjectGroupPython] Dy_element001  label="Dy_element : 1"  # scripted group (container) (typed FeaturePython)
  n = 1
  ref = Dy_element
FEATURE [App::DocumentObjectGroupPython] G4_Dy  # scripted group (container) (typed FeaturePython)
  Dunit = g/cm3
  Dvalue = 8.55
  Group = -> [Dy_element001]
  conduct = 2
  density = 1
  expand = 3
  formula = Dy
  name = G4_Dy
  specific = 4
FEATURE [App::DocumentObjectGroupPython] Ho_element001  label="Ho_element : 1"  # scripted group (container) (typed FeaturePython)
  n = 1
  ref = Ho_element
FEATURE [App::DocumentObjectGroupPython] G4_Ho  # scripted group (container) (typed FeaturePython)
  Dunit = g/cm3
  Dvalue = 8.795
  Group = -> [Ho_element001]
  conduct = 2
  density = 1
  expand = 3
  formula = Ho
  name = G4_Ho
  specific = 4
FEATURE [App::DocumentObjectGroupPython] Er_element001  label="Er_element : 1"  # scripted group (container) (typed FeaturePython)
  n = 1
  ref = Er_element
FEATURE [App::DocumentObjectGroupPython] G4_Er  # scripted group (container) (typed FeaturePython)
  Dunit = g/cm3
  Dvalue = 9.066
  Group = -> [Er_element001]
  conduct = 2
  density = 1
  expand = 3
  formula = Er
  name = G4_Er
  specific = 4
FEATURE [App::DocumentObjectGroupPython] Tm_element001  label="Tm_element : 1"  # scripted group (container) (typed FeaturePython)
  n = 1
  ref = Tm_element
FEATURE [App::DocumentObjectGroupPython] G4_Tm  # scripted group (container) (typed FeaturePython)
  Dunit = g/cm3
  Dvalue = 9.321
  Group = -> [Tm_element001]
  conduct = 2
  density = 1
  expand = 3
  formula = Tm
  name = G4_Tm
  specific = 4
FEATURE [App::DocumentObjectGroupPython] Yb_element001  label="Yb_element : 1"  # scripted group (container) (typed FeaturePython)
  n = 1
  ref = Yb_element
FEATURE [App::DocumentObjectGroupPython] G4_Yb  # scripted group (container) (typed FeaturePython)
  Dunit = g/cm3
  Dvalue = 6.73
  Group = -> [Yb_element001]
  conduct = 2
  density = 1
  expand = 3
  formula = Yb
  name = G4_Yb
  specific = 4
FEATURE [App::DocumentObjectGroupPython] Lu_element001  label="Lu_element : 1"  # scripted group (container) (typed FeaturePython)
  n = 1
  ref = Lu_element
FEATURE [App::DocumentObjectGroupPython] G4_Lu  # scripted group (container) (typed FeaturePython)
  Dunit = g/cm3
  Dvalue = 9.84
  Group = -> [Lu_element001]
  conduct = 2
  density = 1
  expand = 3
  formula = Lu
  name = G4_Lu
  specific = 4
FEATURE [App::DocumentObjectGroupPython] Hf_element001  label="Hf_element : 1"  # scripted group (container) (typed FeaturePython)
  n = 1
  ref = Hf_element
FEATURE [App::DocumentObjectGroupPython] G4_Hf  # scripted group (container) (typed FeaturePython)
  Dunit = g/cm3
  Dvalue = 13.31
  Group = -> [Hf_element001]
  conduct = 2
  density = 1
  expand = 3
  formula = Hf
  name = G4_Hf
  specific = 4
FEATURE [App::DocumentObjectGroupPython] Ta_element001  label="Ta_element : 1"  # scripted group (container) (typed FeaturePython)
  n = 1
  ref = Ta_element
FEATURE [App::DocumentObjectGroupPython] G4_Ta  # scripted group (container) (typed FeaturePython)
  Dunit = g/cm3
  Dvalue = 16.654
  Group = -> [Ta_element001]
  conduct = 2
  density = 1
  expand = 3
  formula = Ta
  name = G4_Ta
  specific = 4
FEATURE [App::DocumentObjectGroupPython] W_element004  label="W_element : 004"  # scripted group (container) (typed FeaturePython)
  n = 1
  ref = W_element
FEATURE [App::DocumentObjectGroupPython] G4_W  # scripted group (container) (typed FeaturePython)
  Dunit = g/cm3
  Dvalue = 19.3
  Group = -> [W_element004]
  conduct = 2
  density = 1
  expand = 3
  formula = W
  name = G4_W
  specific = 4
FEATURE [App::DocumentObjectGroupPython] Re_element001  label="Re_element : 1"  # scripted group (container) (typed FeaturePython)
  n = 1
  ref = Re_element
FEATURE [App::DocumentObjectGroupPython] G4_Re  # scripted group (container) (typed FeaturePython)
  Dunit = g/cm3
  Dvalue = 21.02
  Group = -> [Re_element001]
  conduct = 2
  density = 1
  expand = 3
  formula = Re
  name = G4_Re
  specific = 4
FEATURE [App::DocumentObjectGroupPython] Os_element001  label="Os_element : 1"  # scripted group (container) (typed FeaturePython)
  n = 1
  ref = Os_element
FEATURE [App::DocumentObjectGroupPython] G4_Os  # scripted group (container) (typed FeaturePython)
  Dunit = g/cm3
  Dvalue = 22.57
  Group = -> [Os_element001]
  conduct = 2
  density = 1
  expand = 3
  formula = Os
  name = G4_Os
  specific = 4
FEATURE [App::DocumentObjectGroupPython] Ir_element001  label="Ir_element : 1"  # scripted group (container) (typed FeaturePython)
  n = 1
  ref = Ir_element
FEATURE [App::DocumentObjectGroupPython] G4_Ir  # scripted group (container) (typed FeaturePython)
  Dunit = g/cm3
  Dvalue = 22.42
  Group = -> [Ir_element001]
  conduct = 2
  density = 1
  expand = 3
  formula = Ir
  name = G4_Ir
  specific = 4
FEATURE [App::DocumentObjectGroupPython] Pt_element001  label="Pt_element : 1"  # scripted group (container) (typed FeaturePython)
  n = 1
  ref = Pt_element
FEATURE [App::DocumentObjectGroupPython] G4_Pt  # scripted group (container) (typed FeaturePython)
  Dunit = g/cm3
  Dvalue = 21.45
  Group = -> [Pt_element001]
  conduct = 2
  density = 1
  expand = 3
  formula = Pt
  name = G4_Pt
  specific = 4
FEATURE [App::DocumentObjectGroupPython] Au_element001  label="Au_element : 1"  # scripted group (container) (typed FeaturePython)
  n = 1
  ref = Au_element
FEATURE [App::DocumentObjectGroupPython] G4_Au  # scripted group (container) (typed FeaturePython)
  Dunit = g/cm3
  Dvalue = 19.32
  Group = -> [Au_element001]
  conduct = 2
  density = 1
  expand = 3
  formula = Au
  name = G4_Au
  specific = 4
FEATURE [App::DocumentObjectGroupPython] Hg_element002  label="Hg_element : 002"  # scripted group (container) (typed FeaturePython)
  n = 1
  ref = Hg_element
FEATURE [App::DocumentObjectGroupPython] G4_Hg  # scripted group (container) (typed FeaturePython)
  Dunit = g/cm3
  Dvalue = 13.546
  Group = -> [Hg_element002]
  conduct = 2
  density = 1
  expand = 3
  formula = Hg
  name = G4_Hg
  specific = 4
FEATURE [App::DocumentObjectGroupPython] Tl_element002  label="Tl_element : 002"  # scripted group (container) (typed FeaturePython)
  n = 1
  ref = Tl_element
FEATURE [App::DocumentObjectGroupPython] G4_Tl  # scripted group (container) (typed FeaturePython)
  Dunit = g/cm3
  Dvalue = 11.72
  Group = -> [Tl_element002]
  conduct = 2
  density = 1
  expand = 3
  formula = Tl
  name = G4_Tl
  specific = 4
FEATURE [App::DocumentObjectGroupPython] Pb_element003  label="Pb_element : 1"  # scripted group (container) (typed FeaturePython)
  n = 1
  ref = Pb_element
FEATURE [App::DocumentObjectGroupPython] G4_Pb  # scripted group (container) (typed FeaturePython)
  Dunit = g/cm3
  Dvalue = 11.35
  Group = -> [Pb_element003]
  conduct = 2
  density = 1
  expand = 3
  formula = Pb
  name = G4_Pb
  specific = 4
FEATURE [App::DocumentObjectGroupPython] Bi_element002  label="Bi_element : 1"  # scripted group (container) (typed FeaturePython)
  n = 1
  ref = Bi_element
FEATURE [App::DocumentObjectGroupPython] G4_Bi  # scripted group (container) (typed FeaturePython)
  Dunit = g/cm3
  Dvalue = 9.747
  Group = -> [Bi_element002]
  conduct = 2
  density = 1
  expand = 3
  formula = Bi
  name = G4_Bi
  specific = 4
FEATURE [App::DocumentObjectGroupPython] Po_element001  label="Po_element : 1"  # scripted group (container) (typed FeaturePython)
  n = 1
  ref = Po_element
FEATURE [App::DocumentObjectGroupPython] G4_Po  # scripted group (container) (typed FeaturePython)
  Dunit = g/cm3
  Dvalue = 9.32
  Group = -> [Po_element001]
  conduct = 2
  density = 1
  expand = 3
  formula = Po
  name = G4_Po
  specific = 4
FEATURE [App::DocumentObjectGroupPython] At_element001  label="At_element : 1"  # scripted group (container) (typed FeaturePython)
  n = 1
  ref = At_element
FEATURE [App::DocumentObjectGroupPython] G4_At  # scripted group (container) (typed FeaturePython)
  Dunit = g/cm3
  Dvalue = 9.32
  Group = -> [At_element001]
  conduct = 2
  density = 1
  expand = 3
  formula = At
  name = G4_At
  specific = 4
FEATURE [App::DocumentObjectGroupPython] Rn_element001  label="Rn_element : 1"  # scripted group (container) (typed FeaturePython)
  n = 1
  ref = Rn_element
FEATURE [App::DocumentObjectGroupPython] G4_Rn  # scripted group (container) (typed FeaturePython)
  Dunit = g/cm3
  Dvalue = 0.00900662
  Group = -> [Rn_element001]
  conduct = 2
  density = 1
  expand = 3
  formula = Rn
  name = G4_Rn
  specific = 4
FEATURE [App::DocumentObjectGroupPython] Fr_element001  label="Fr_element : 1"  # scripted group (container) (typed FeaturePython)
  n = 1
  ref = Fr_element
FEATURE [App::DocumentObjectGroupPython] G4_Fr  # scripted group (container) (typed FeaturePython)
  Dunit = g/cm3
  Dvalue = 1
  Group = -> [Fr_element001]
  conduct = 2
  density = 1
  expand = 3
  formula = Fr
  name = G4_Fr
  specific = 4
FEATURE [App::DocumentObjectGroupPython] Ra_element001  label="Ra_element : 1"  # scripted group (container) (typed FeaturePython)
  n = 1
  ref = Ra_element
FEATURE [App::DocumentObjectGroupPython] G4_Ra  # scripted group (container) (typed FeaturePython)
  Dunit = g/cm3
  Dvalue = 5
  Group = -> [Ra_element001]
  conduct = 2
  density = 1
  expand = 3
  formula = Ra
  name = G4_Ra
  specific = 4
FEATURE [App::DocumentObjectGroupPython] Ac_element001  label="Ac_element : 1"  # scripted group (container) (typed FeaturePython)
  n = 1
  ref = Ac_element
FEATURE [App::DocumentObjectGroupPython] G4_Ac  # scripted group (container) (typed FeaturePython)
  Dunit = g/cm3
  Dvalue = 10.07
  Group = -> [Ac_element001]
  conduct = 2
  density = 1
  expand = 3
  formula = Ac
  name = G4_Ac
  specific = 4
FEATURE [App::DocumentObjectGroupPython] Th_element001  label="Th_element : 1"  # scripted group (container) (typed FeaturePython)
  n = 1
  ref = Th_element
FEATURE [App::DocumentObjectGroupPython] G4_Th  # scripted group (container) (typed FeaturePython)
  Dunit = g/cm3
  Dvalue = 11.72
  Group = -> [Th_element001]
  conduct = 2
  density = 1
  expand = 3
  formula = Th
  name = G4_Th
  specific = 4
FEATURE [App::DocumentObjectGroupPython] Pa_element001  label="Pa_element : 1"  # scripted group (container) (typed FeaturePython)
  n = 1
  ref = Pa_element
FEATURE [App::DocumentObjectGroupPython] G4_Pa  # scripted group (container) (typed FeaturePython)
  Dunit = g/cm3
  Dvalue = 15.37
  Group = -> [Pa_element001]
  conduct = 2
  density = 1
  expand = 3
  formula = Pa
  name = G4_Pa
  specific = 4
FEATURE [App::DocumentObjectGroupPython] U_element004  label="U_element : 004"  # scripted group (container) (typed FeaturePython)
  n = 1
  ref = U_element
FEATURE [App::DocumentObjectGroupPython] G4_U  # scripted group (container) (typed FeaturePython)
  Dunit = g/cm3
  Dvalue = 18.95
  Group = -> [U_element004]
  conduct = 2
  density = 1
  expand = 3
  formula = U
  name = G4_U
  specific = 4
FEATURE [App::DocumentObjectGroupPython] Np_element001  label="Np_element : 1"  # scripted group (container) (typed FeaturePython)
  n = 1
  ref = Np_element
FEATURE [App::DocumentObjectGroupPython] G4_Np  # scripted group (container) (typed FeaturePython)
  Dunit = g/cm3
  Dvalue = 20.25
  Group = -> [Np_element001]
  conduct = 2
  density = 1
  expand = 3
  formula = Np
  name = G4_Np
  specific = 4
FEATURE [App::DocumentObjectGroupPython] Pu_element002  label="Pu_element : 002"  # scripted group (container) (typed FeaturePython)
  n = 1
  ref = Pu_element
FEATURE [App::DocumentObjectGroupPython] G4_Pu  # scripted group (container) (typed FeaturePython)
  Dunit = g/cm3
  Dvalue = 19.84
  Group = -> [Pu_element002]
  conduct = 2
  density = 1
  expand = 3
  formula = Pu
  name = G4_Pu
  specific = 4
FEATURE [App::DocumentObjectGroupPython] Am_element001  label="Am_element : 1"  # scripted group (container) (typed FeaturePython)
  n = 1
  ref = Am_element
FEATURE [App::DocumentObjectGroupPython] G4_Am  # scripted group (container) (typed FeaturePython)
  Dunit = g/cm3
  Dvalue = 13.67
  Group = -> [Am_element001]
  conduct = 2
  density = 1
  expand = 3
  formula = Am
  name = G4_Am
  specific = 4
FEATURE [App::DocumentObjectGroupPython] Cm_element001  label="Cm_element : 1"  # scripted group (container) (typed FeaturePython)
  n = 1
  ref = Cm_element
FEATURE [App::DocumentObjectGroupPython] G4_Cm  # scripted group (container) (typed FeaturePython)
  Dunit = g/cm3
  Dvalue = 13.51
  Group = -> [Cm_element001]
  conduct = 2
  density = 1
  expand = 3
  formula = Cm
  name = G4_Cm
  specific = 4
FEATURE [App::DocumentObjectGroupPython] Bk_element001  label="Bk_element : 1"  # scripted group (container) (typed FeaturePython)
  n = 1
  ref = Bk_element
FEATURE [App::DocumentObjectGroupPython] G4_Bk  # scripted group (container) (typed FeaturePython)
  Dunit = g/cm3
  Dvalue = 14
  Group = -> [Bk_element001]
  conduct = 2
  density = 1
  expand = 3
  formula = Bk
  name = G4_Bk
  specific = 4
FEATURE [App::DocumentObjectGroupPython] Cf_element001  label="Cf_element : 1"  # scripted group (container) (typed FeaturePython)
  n = 1
  ref = Cf_element
FEATURE [App::DocumentObjectGroupPython] G4_Cf  # scripted group (container) (typed FeaturePython)
  Dunit = g/cm3
  Dvalue = 10
  Group = -> [Cf_element001]
  conduct = 2
  density = 1
  expand = 3
  formula = Cf
  name = G4_Cf
  specific = 4
FEATURE [App::DocumentObjectGroupPython] Element  # scripted group (container) (typed FeaturePython)
  Group = -> [G4_H,G4_He,G4_Li,G4_Be,G4_B,G4_C,G4_N,G4_O,G4_F,G4_Ne,G4_Na,G4_Mg,G4_Al,G4_Si,G4_P,G4_S,G4_Cl,G4_Ar,G4_K,G4_Ca,G4_Sc,G4_Ti,G4_V,G4_Cr,G4_Mn,G4_Fe,G4_Co,G4_Ni,G4_Cu,G4_Zn,G4_Ga,G4_Ge,G4_As,G4_Se,G4_Br,G4_Kr,G4_Rb,G4_Sr,G4_Y,G4_Zr,G4_Nb,G4_Mo,G4_Tc,G4_Ru,G4_Rh,G4_Pd,G4_Ag,G4_Cd,G4_In,G4_Sn,G4_Sb,G4_Te,G4_I,G4_Xe,G4_Cs,G4_Ba,G4_La,G4_Ce,G4_Pr,G4_Nd,G4_Pm,G4_Sm,G4_Eu,G4_Gd,G4_Tb,G4_Dy,G4_Ho,G4_Er,+30 more]
FEATURE [App::DocumentObjectGroupPython] H_element114  label="H_element : 063"  # scripted group (container) (typed FeaturePython)
  n = 2
  ref = H_element
FEATURE [App::DocumentObjectGroupPython] G4_lH2  # scripted group (container) (typed FeaturePython)
  Dunit = g/cm3
  Dvalue = 0.0708
  Group = -> [H_element114]
  conduct = 2
  density = 1
  expand = 3
  formula = G4_lH2
  name = G4_lH2
  specific = 4
FEATURE [App::DocumentObjectGroupPython] N_element049  label="N_element : 022"  # scripted group (container) (typed FeaturePython)
  n = 2
  ref = N_element
FEATURE [App::DocumentObjectGroupPython] G4_lN2  # scripted group (container) (typed FeaturePython)
  Dunit = g/cm3
  Dvalue = 0.807
  Group = -> [N_element049]
  conduct = 2
  density = 1
  expand = 3
  formula = G4_lN2
  name = G4_lN2
  specific = 4
FEATURE [App::DocumentObjectGroupPython] O_element106  label="O_element : 060"  # scripted group (container) (typed FeaturePython)
  n = 2
  ref = O_element
FEATURE [App::DocumentObjectGroupPython] G4_lO2  # scripted group (container) (typed FeaturePython)
  Dunit = g/cm3
  Dvalue = 1.141
  Group = -> [O_element106]
  conduct = 2
  density = 1
  expand = 3
  formula = G4_lO2
  name = G4_lO2
  specific = 4
FEATURE [App::DocumentObjectGroupPython] Ar  label="Ar : 1"  # scripted group (container) (typed FeaturePython)
  n = 1
  ref = Ar
FEATURE [App::DocumentObjectGroupPython] G4_lAr  # scripted group (container) (typed FeaturePython)
  Dunit = g/cm3
  Dvalue = 1.396
  Group = -> [Ar]
  conduct = 2
  density = 1
  expand = 3
  formula = G4_lAr
  name = G4_lAr
  specific = 4
FEATURE [App::DocumentObjectGroupPython] Br  label="Br : 1"  # scripted group (container) (typed FeaturePython)
  n = 1
  ref = Br
FEATURE [App::DocumentObjectGroupPython] G4_lBr  # scripted group (container) (typed FeaturePython)
  Dunit = g/cm3
  Dvalue = 3.1028
  Group = -> [Br]
  conduct = 2
  density = 1
  expand = 3
  formula = G4_lBr
  name = G4_lBr
  specific = 4
FEATURE [App::DocumentObjectGroupPython] Kr  label="Kr : 1"  # scripted group (container) (typed FeaturePython)
  n = 1
  ref = Kr
FEATURE [App::DocumentObjectGroupPython] G4_lKr  # scripted group (container) (typed FeaturePython)
  Dunit = g/cm3
  Dvalue = 2.418
  Group = -> [Kr]
  conduct = 2
  density = 1
  expand = 3
  formula = G4_lKr
  name = G4_lKr
  specific = 4
FEATURE [App::DocumentObjectGroupPython] Xe  label="Xe : 1"  # scripted group (container) (typed FeaturePython)
  n = 1
  ref = Xe
FEATURE [App::DocumentObjectGroupPython] G4_lXe  # scripted group (container) (typed FeaturePython)
  Dunit = g/cm3
  Dvalue = 2.953
  Group = -> [Xe]
  conduct = 2
  density = 1
  expand = 3
  formula = G4_lXe
  name = G4_lXe
  specific = 4
FEATURE [App::DocumentObjectGroupPython] O_element107  label="O_element : 061"  # scripted group (container) (typed FeaturePython)
  n = 4
  ref = O_element
FEATURE [App::DocumentObjectGroupPython] Pb_element004  label="Pb_element : 002"  # scripted group (container) (typed FeaturePython)
  n = 1
  ref = Pb_element
FEATURE [App::DocumentObjectGroupPython] W_element005  label="W_element : 005"  # scripted group (container) (typed FeaturePython)
  n = 1
  ref = W_element
FEATURE [App::DocumentObjectGroupPython] G4_PbWO4  # scripted group (container) (typed FeaturePython)
  Dunit = g/cm3
  Dvalue = 8.28
  Group = -> [O_element107,Pb_element004,W_element005]
  conduct = 2
  density = 1
  expand = 3
  formula = G4_PbWO4
  name = G4_PbWO4
  specific = 4
FEATURE [App::DocumentObjectGroupPython] alactic  label="alactic : 1"  # scripted group (container) (typed FeaturePython)
  n = 1
  ref = alactic
FEATURE [App::DocumentObjectGroupPython] G4_Galactic  # scripted group (container) (typed FeaturePython)
  Dunit = g/cm3
  Dvalue = 0
  Group = -> [alactic]
  conduct = 2
  density = 1
  expand = 3
  formula = G4_Galactic
  name = G4_Galactic
  specific = 4
FEATURE [App::DocumentObjectGroupPython] RAPHITE_POROUS  label="RAPHITE_POROUS : 1"  # scripted group (container) (typed FeaturePython)
  n = 1
  ref = RAPHITE_POROUS
FEATURE [App::DocumentObjectGroupPython] G4_GRAPHITE_POROUS  # scripted group (container) (typed FeaturePython)
  Dunit = g/cm3
  Dvalue = 1.7
  Group = -> [RAPHITE_POROUS]
  conduct = 2
  density = 1
  expand = 3
  formula = G4_GRAPHITE_POROUS
  name = G4_GRAPHITE_POROUS
  specific = 4
FEATURE [App::DocumentObjectGroupPython] H_element115  label="H_element : 0.150"  # scripted group (container) (typed FeaturePython)
  n = 0.080538
FEATURE [App::DocumentObjectGroupPython] C_element125  label="C_element : 0.600"  # scripted group (container) (typed FeaturePython)
  n = 0.599848
FEATURE [App::DocumentObjectGroupPython] O_element108  label="O_element : 0.320"  # scripted group (container) (typed FeaturePython)
  n = 0.319614
FEATURE [App::DocumentObjectGroupPython] G4_LUCITE  # scripted group (container) (typed FeaturePython)
  Dunit = g/cm3
  Dvalue = 1.19
  Group = -> [H_element115,C_element125,O_element108]
  conduct = 2
  density = 1
  expand = 3
  formula = G4_LUCITE
  name = G4_LUCITE
  specific = 4
FEATURE [App::DocumentObjectGroupPython] Cu_element002  label="Cu_element : 62"  # scripted group (container) (typed FeaturePython)
  n = 62
  ref = Cu_element
FEATURE [App::DocumentObjectGroupPython] Zn_element002  label="Zn_element : 35"  # scripted group (container) (typed FeaturePython)
  n = 35
  ref = Zn_element
FEATURE [App::DocumentObjectGroupPython] Pb_element005  label="Pb_element : 3"  # scripted group (container) (typed FeaturePython)
  n = 3
  ref = Pb_element
FEATURE [App::DocumentObjectGroupPython] G4_BRASS  # scripted group (container) (typed FeaturePython)
  Dunit = g/cm3
  Dvalue = 8.52
  Group = -> [Cu_element002,Zn_element002,Pb_element005]
  conduct = 2
  density = 1
  expand = 3
  formula = G4_BRASS
  name = G4_BRASS
  specific = 4
FEATURE [App::DocumentObjectGroupPython] Cu_element003  label="Cu_element : 89"  # scripted group (container) (typed FeaturePython)
  n = 89
  ref = Cu_element
FEATURE [App::DocumentObjectGroupPython] Zn_element003  label="Zn_element : 9"  # scripted group (container) (typed FeaturePython)
  n = 9
  ref = Zn_element
FEATURE [App::DocumentObjectGroupPython] Pb_element006  label="Pb_element : 2"  # scripted group (container) (typed FeaturePython)
  n = 2
  ref = Pb_element
FEATURE [App::DocumentObjectGroupPython] G4_BRONZE  # scripted group (container) (typed FeaturePython)
  Dunit = g/cm3
  Dvalue = 8.82
  Group = -> [Cu_element003,Zn_element003,Pb_element006]
  conduct = 2
  density = 1
  expand = 3
  formula = G4_BRONZE
  name = G4_BRONZE
  specific = 4
FEATURE [App::DocumentObjectGroupPython] Fe_element008  label="Fe_element : 74"  # scripted group (container) (typed FeaturePython)
  n = 74
  ref = Fe_element
FEATURE [App::DocumentObjectGroupPython] Cr_element002  label="Cr_element : 18"  # scripted group (container) (typed FeaturePython)
  n = 18
  ref = Cr_element
FEATURE [App::DocumentObjectGroupPython] Ni_element002  label="Ni_element : 8"  # scripted group (container) (typed FeaturePython)
  n = 8
  ref = Ni_element
FEATURE [App::DocumentObjectGroupPython] G4_STAINLESS_STEEL  label="G4_STAINLESS-STEEL"  # scripted group (container) (typed FeaturePython)
  Dunit = g/cm3
  Dvalue = 8
  Group = -> [Fe_element008,Cr_element002,Ni_element002]
  conduct = 2
  density = 1
  expand = 3
  formula = G4_STAINLESS-STEEL
  name = G4_STAINLESS-STEEL
  specific = 4
FEATURE [App::DocumentObjectGroupPython] H_element116  label="H_element : 064"  # scripted group (container) (typed FeaturePython)
  n = 18
  ref = H_element
FEATURE [App::DocumentObjectGroupPython] C_element126  label="C_element : 071"  # scripted group (container) (typed FeaturePython)
  n = 12
  ref = C_element
FEATURE [App::DocumentObjectGroupPython] O_element109  label="O_element : 062"  # scripted group (container) (typed FeaturePython)
  n = 7
  ref = O_element
FEATURE [App::DocumentObjectGroupPython] G4_CR39  # scripted group (container) (typed FeaturePython)
  Dunit = g/cm3
  Dvalue = 1.32
  Group = -> [H_element116,C_element126,O_element109]
  conduct = 2
  density = 1
  expand = 3
  formula = G4_CR39
  name = G4_CR39
  specific = 4
FEATURE [App::DocumentObjectGroupPython] H_element117  label="H_element : 38"  # scripted group (container) (typed FeaturePython)
  n = 38
  ref = H_element
FEATURE [App::DocumentObjectGroupPython] C_element127  label="C_element : 072"  # scripted group (container) (typed FeaturePython)
  n = 18
  ref = C_element
FEATURE [App::DocumentObjectGroupPython] O_element110  label="O_element : 063"  # scripted group (container) (typed FeaturePython)
  n = 1
  ref = O_element
FEATURE [App::DocumentObjectGroupPython] G4_OCTADECANOL  # scripted group (container) (typed FeaturePython)
  Dunit = g/cm3
  Dvalue = 0.812
  Group = -> [H_element117,C_element127,O_element110]
  conduct = 2
  density = 1
  expand = 3
  formula = G4_OCTADECANOL
  name = G4_OCTADECANOL
  specific = 4
FEATURE [App::DocumentObjectGroupPython] HEP  # scripted group (container) (typed FeaturePython)
  Group = -> [G4_lH2,G4_lN2,G4_lO2,G4_lAr,G4_lBr,G4_lKr,G4_lXe,G4_PbWO4,G4_Galactic,G4_GRAPHITE_POROUS,G4_LUCITE,G4_BRASS,G4_BRONZE,G4_STAINLESS_STEEL,G4_CR39,G4_OCTADECANOL]
FEATURE [App::DocumentObjectGroupPython] C_element128  label="C_element : 073"  # scripted group (container) (typed FeaturePython)
  n = 14
  ref = C_element
FEATURE [App::DocumentObjectGroupPython] H_element118  label="H_element : 065"  # scripted group (container) (typed FeaturePython)
  n = 10
  ref = H_element
FEATURE [App::DocumentObjectGroupPython] O_element111  label="O_element : 064"  # scripted group (container) (typed FeaturePython)
  n = 2
  ref = O_element
FEATURE [App::DocumentObjectGroupPython] N_element050  label="N_element : 023"  # scripted group (container) (typed FeaturePython)
  n = 2
  ref = N_element
FEATURE [App::DocumentObjectGroupPython] G4_KEVLAR  # scripted group (container) (typed FeaturePython)
  Dunit = g/cm3
  Dvalue = 1.44
  Group = -> [C_element128,H_element118,O_element111,N_element050]
  conduct = 2
  density = 1
  expand = 3
  formula = G4_KEVLAR
  name = G4_KEVLAR
  specific = 4
FEATURE [App::DocumentObjectGroupPython] C_element129  label="C_element : 074"  # scripted group (container) (typed FeaturePython)
  n = 10
  ref = C_element
FEATURE [App::DocumentObjectGroupPython] H_element119  label="H_element : 066"  # scripted group (container) (typed FeaturePython)
  n = 8
  ref = H_element
FEATURE [App::DocumentObjectGroupPython] O_element112  label="O_element : 065"  # scripted group (container) (typed FeaturePython)
  n = 4
  ref = O_element
FEATURE [App::DocumentObjectGroupPython] G4_DACRON  # scripted group (container) (typed FeaturePython)
  Dunit = g/cm3
  Dvalue = 1.4
  Group = -> [C_element129,H_element119,O_element112]
  conduct = 2
  density = 1
  expand = 3
  formula = G4_DACRON
  name = G4_DACRON
  specific = 4
FEATURE [App::DocumentObjectGroupPython] C_element130  label="C_element : 075"  # scripted group (container) (typed FeaturePython)
  n = 4
  ref = C_element
FEATURE [App::DocumentObjectGroupPython] H_element120  label="H_element : 067"  # scripted group (container) (typed FeaturePython)
  n = 5
  ref = H_element
FEATURE [App::DocumentObjectGroupPython] Cl_element030  label="Cl_element : 016"  # scripted group (container) (typed FeaturePython)
  n = 1
  ref = Cl_element
FEATURE [App::DocumentObjectGroupPython] G4_NEOPRENE  # scripted group (container) (typed FeaturePython)
  Dunit = g/cm3
  Dvalue = 1.23
  Group = -> [C_element130,H_element120,Cl_element030]
  conduct = 2
  density = 1
  expand = 3
  formula = G4_NEOPRENE
  name = G4_NEOPRENE
  specific = 4
FEATURE [App::DocumentObjectGroupPython] Space  # scripted group (container) (typed FeaturePython)
  Group = -> [G4_KEVLAR,G4_DACRON,G4_NEOPRENE]
FEATURE [App::DocumentObjectGroupPython] H_element121  label="H_element : 068"  # scripted group (container) (typed FeaturePython)
  n = 5
  ref = H_element
FEATURE [App::DocumentObjectGroupPython] C_element131  label="C_element : 076"  # scripted group (container) (typed FeaturePython)
  n = 4
  ref = C_element
FEATURE [App::DocumentObjectGroupPython] N_element051  label="N_element : 3"  # scripted group (container) (typed FeaturePython)
  n = 3
  ref = N_element
FEATURE [App::DocumentObjectGroupPython] O_element113  label="O_element : 066"  # scripted group (container) (typed FeaturePython)
  n = 1
  ref = O_element
FEATURE [App::DocumentObjectGroupPython] G4_CYTOSINE  # scripted group (container) (typed FeaturePython)
  Dunit = g/cm3
  Dvalue = 1.55
  Group = -> [H_element121,C_element131,N_element051,O_element113]
  conduct = 2
  density = 1
  expand = 3
  formula = G4_CYTOSINE
  name = G4_CYTOSINE
  specific = 4
FEATURE [App::DocumentObjectGroupPython] H_element122  label="H_element : 069"  # scripted group (container) (typed FeaturePython)
  n = 6
  ref = H_element
FEATURE [App::DocumentObjectGroupPython] C_element132  label="C_element : 077"  # scripted group (container) (typed FeaturePython)
  n = 5
  ref = C_element
FEATURE [App::DocumentObjectGroupPython] N_element052  label="N_element : 024"  # scripted group (container) (typed FeaturePython)
  n = 2
  ref = N_element
FEATURE [App::DocumentObjectGroupPython] O_element114  label="O_element : 067"  # scripted group (container) (typed FeaturePython)
  n = 2
  ref = O_element
FEATURE [App::DocumentObjectGroupPython] G4_THYMINE  # scripted group (container) (typed FeaturePython)
  Dunit = g/cm3
  Dvalue = 1.23
  Group = -> [H_element122,C_element132,N_element052,O_element114]
  conduct = 2
  density = 1
  expand = 3
  formula = G4_THYMINE
  name = G4_THYMINE
  specific = 4
FEATURE [App::DocumentObjectGroupPython] H_element123  label="H_element : 070"  # scripted group (container) (typed FeaturePython)
  n = 4
  ref = H_element
FEATURE [App::DocumentObjectGroupPython] C_element133  label="C_element : 078"  # scripted group (container) (typed FeaturePython)
  n = 4
  ref = C_element
FEATURE [App::DocumentObjectGroupPython] N_element053  label="N_element : 025"  # scripted group (container) (typed FeaturePython)
  n = 2
  ref = N_element
FEATURE [App::DocumentObjectGroupPython] O_element115  label="O_element : 068"  # scripted group (container) (typed FeaturePython)
  n = 2
  ref = O_element
FEATURE [App::DocumentObjectGroupPython] G4_URACIL  # scripted group (container) (typed FeaturePython)
  Dunit = g/cm3
  Dvalue = 1.32
  Group = -> [H_element123,C_element133,N_element053,O_element115]
  conduct = 2
  density = 1
  expand = 3
  formula = G4_URACIL
  name = G4_URACIL
  specific = 4
FEATURE [App::DocumentObjectGroupPython] H_element124  label="H_element : 071"  # scripted group (container) (typed FeaturePython)
  n = 4
  ref = H_element
FEATURE [App::DocumentObjectGroupPython] C_element134  label="C_element : 079"  # scripted group (container) (typed FeaturePython)
  n = 5
  ref = C_element
FEATURE [App::DocumentObjectGroupPython] N_element054  label="N_element : 026"  # scripted group (container) (typed FeaturePython)
  n = 5
  ref = N_element
FEATURE [App::DocumentObjectGroupPython] G4_DNA_ADENINE  # scripted group (container) (typed FeaturePython)
  Dunit = g/cm3
  Dvalue = 1
  Group = -> [H_element124,C_element134,N_element054]
  conduct = 2
  density = 1
  expand = 3
  formula = G4_DNA_ADENINE
  name = G4_DNA_ADENINE
  specific = 4
FEATURE [App::DocumentObjectGroupPython] H_element125  label="H_element : 072"  # scripted group (container) (typed FeaturePython)
  n = 4
  ref = H_element
FEATURE [App::DocumentObjectGroupPython] C_element135  label="C_element : 080"  # scripted group (container) (typed FeaturePython)
  n = 5
  ref = C_element
FEATURE [App::DocumentObjectGroupPython] N_element055  label="N_element : 027"  # scripted group (container) (typed FeaturePython)
  n = 5
  ref = N_element
FEATURE [App::DocumentObjectGroupPython] O_element116  label="O_element : 069"  # scripted group (container) (typed FeaturePython)
  n = 1
  ref = O_element
FEATURE [App::DocumentObjectGroupPython] G4_DNA_GUANINE  # scripted group (container) (typed FeaturePython)
  Dunit = g/cm3
  Dvalue = 1
  Group = -> [H_element125,C_element135,N_element055,O_element116]
  conduct = 2
  density = 1
  expand = 3
  formula = G4_DNA_GUANINE
  name = G4_DNA_GUANINE
  specific = 4
FEATURE [App::DocumentObjectGroupPython] H_element126  label="H_element : 073"  # scripted group (container) (typed FeaturePython)
  n = 4
  ref = H_element
FEATURE [App::DocumentObjectGroupPython] C_element136  label="C_element : 081"  # scripted group (container) (typed FeaturePython)
  n = 4
  ref = C_element
FEATURE [App::DocumentObjectGroupPython] N_element056  label="N_element : 028"  # scripted group (container) (typed FeaturePython)
  n = 3
  ref = N_element
FEATURE [App::DocumentObjectGroupPython] O_element117  label="O_element : 070"  # scripted group (container) (typed FeaturePython)
  n = 1
  ref = O_element
FEATURE [App::DocumentObjectGroupPython] G4_DNA_CYTOSINE  # scripted group (container) (typed FeaturePython)
  Dunit = g/cm3
  Dvalue = 1
  Group = -> [H_element126,C_element136,N_element056,O_element117]
  conduct = 2
  density = 1
  expand = 3
  formula = G4_DNA_CYTOSINE
  name = G4_DNA_CYTOSINE
  specific = 4
FEATURE [App::DocumentObjectGroupPython] H_element127  label="H_element : 074"  # scripted group (container) (typed FeaturePython)
  n = 5
  ref = H_element
FEATURE [App::DocumentObjectGroupPython] C_element137  label="C_element : 082"  # scripted group (container) (typed FeaturePython)
  n = 5
  ref = C_element
FEATURE [App::DocumentObjectGroupPython] N_element057  label="N_element : 029"  # scripted group (container) (typed FeaturePython)
  n = 2
  ref = N_element
FEATURE [App::DocumentObjectGroupPython] O_element118  label="O_element : 071"  # scripted group (container) (typed FeaturePython)
  n = 2
  ref = O_element
FEATURE [App::DocumentObjectGroupPython] G4_DNA_THYMINE  # scripted group (container) (typed FeaturePython)
  Dunit = g/cm3
  Dvalue = 1
  Group = -> [H_element127,C_element137,N_element057,O_element118]
  conduct = 2
  density = 1
  expand = 3
  formula = G4_DNA_THYMINE
  name = G4_DNA_THYMINE
  specific = 4
FEATURE [App::DocumentObjectGroupPython] H_element128  label="H_element : 075"  # scripted group (container) (typed FeaturePython)
  n = 3
  ref = H_element
FEATURE [App::DocumentObjectGroupPython] C_element138  label="C_element : 083"  # scripted group (container) (typed FeaturePython)
  n = 4
  ref = C_element
FEATURE [App::DocumentObjectGroupPython] N_element058  label="N_element : 030"  # scripted group (container) (typed FeaturePython)
  n = 2
  ref = N_element
FEATURE [App::DocumentObjectGroupPython] O_element119  label="O_element : 072"  # scripted group (container) (typed FeaturePython)
  n = 2
  ref = O_element
FEATURE [App::DocumentObjectGroupPython] G4_DNA_URACIL  # scripted group (container) (typed FeaturePython)
  Dunit = g/cm3
  Dvalue = 1
  Group = -> [H_element128,C_element138,N_element058,O_element119]
  conduct = 2
  density = 1
  expand = 3
  formula = G4_DNA_URACIL
  name = G4_DNA_URACIL
  specific = 4
FEATURE [App::DocumentObjectGroupPython] H_element129  label="H_element : 076"  # scripted group (container) (typed FeaturePython)
  n = 10
  ref = H_element
FEATURE [App::DocumentObjectGroupPython] C_element139  label="C_element : 084"  # scripted group (container) (typed FeaturePython)
  n = 10
  ref = C_element
FEATURE [App::DocumentObjectGroupPython] N_element059  label="N_element : 031"  # scripted group (container) (typed FeaturePython)
  n = 5
  ref = N_element
FEATURE [App::DocumentObjectGroupPython] O_element120  label="O_element : 073"  # scripted group (container) (typed FeaturePython)
  n = 4
  ref = O_element
FEATURE [App::DocumentObjectGroupPython] G4_DNA_ADENOSINE  # scripted group (container) (typed FeaturePython)
  Dunit = g/cm3
  Dvalue = 1
  Group = -> [H_element129,C_element139,N_element059,O_element120]
  conduct = 2
  density = 1
  expand = 3
  formula = G4_DNA_ADENOSINE
  name = G4_DNA_ADENOSINE
  specific = 4
FEATURE [App::DocumentObjectGroupPython] H_element130  label="H_element : 077"  # scripted group (container) (typed FeaturePython)
  n = 10
  ref = H_element
FEATURE [App::DocumentObjectGroupPython] C_element140  label="C_element : 085"  # scripted group (container) (typed FeaturePython)
  n = 10
  ref = C_element
FEATURE [App::DocumentObjectGroupPython] N_element060  label="N_element : 032"  # scripted group (container) (typed FeaturePython)
  n = 5
  ref = N_element
FEATURE [App::DocumentObjectGroupPython] O_element121  label="O_element : 074"  # scripted group (container) (typed FeaturePython)
  n = 5
  ref = O_element
FEATURE [App::DocumentObjectGroupPython] G4_DNA_GUANOSINE  # scripted group (container) (typed FeaturePython)
  Dunit = g/cm3
  Dvalue = 1
  Group = -> [H_element130,C_element140,N_element060,O_element121]
  conduct = 2
  density = 1
  expand = 3
  formula = G4_DNA_GUANOSINE
  name = G4_DNA_GUANOSINE
  specific = 4
FEATURE [App::DocumentObjectGroupPython] H_element131  label="H_element : 078"  # scripted group (container) (typed FeaturePython)
  n = 10
  ref = H_element
FEATURE [App::DocumentObjectGroupPython] C_element141  label="C_element : 086"  # scripted group (container) (typed FeaturePython)
  n = 9
  ref = C_element
FEATURE [App::DocumentObjectGroupPython] N_element061  label="N_element : 033"  # scripted group (container) (typed FeaturePython)
  n = 3
  ref = N_element
FEATURE [App::DocumentObjectGroupPython] O_element122  label="O_element : 075"  # scripted group (container) (typed FeaturePython)
  n = 5
  ref = O_element
FEATURE [App::DocumentObjectGroupPython] G4_DNA_CYTIDINE  # scripted group (container) (typed FeaturePython)
  Dunit = g/cm3
  Dvalue = 1
  Group = -> [H_element131,C_element141,N_element061,O_element122]
  conduct = 2
  density = 1
  expand = 3
  formula = G4_DNA_CYTIDINE
  name = G4_DNA_CYTIDINE
  specific = 4
FEATURE [App::DocumentObjectGroupPython] H_element132  label="H_element : 079"  # scripted group (container) (typed FeaturePython)
  n = 9
  ref = H_element
FEATURE [App::DocumentObjectGroupPython] C_element142  label="C_element : 087"  # scripted group (container) (typed FeaturePython)
  n = 9
  ref = C_element
FEATURE [App::DocumentObjectGroupPython] N_element062  label="N_element : 034"  # scripted group (container) (typed FeaturePython)
  n = 2
  ref = N_element
FEATURE [App::DocumentObjectGroupPython] O_element123  label="O_element : 076"  # scripted group (container) (typed FeaturePython)
  n = 6
  ref = O_element
FEATURE [App::DocumentObjectGroupPython] G4_DNA_URIDINE  # scripted group (container) (typed FeaturePython)
  Dunit = g/cm3
  Dvalue = 1
  Group = -> [H_element132,C_element142,N_element062,O_element123]
  conduct = 2
  density = 1
  expand = 3
  formula = G4_DNA_URIDINE
  name = G4_DNA_URIDINE
  specific = 4
FEATURE [App::DocumentObjectGroupPython] H_element133  label="H_element : 080"  # scripted group (container) (typed FeaturePython)
  n = 11
  ref = H_element
FEATURE [App::DocumentObjectGroupPython] C_element143  label="C_element : 088"  # scripted group (container) (typed FeaturePython)
  n = 10
  ref = C_element
FEATURE [App::DocumentObjectGroupPython] N_element063  label="N_element : 035"  # scripted group (container) (typed FeaturePython)
  n = 2
  ref = N_element
FEATURE [App::DocumentObjectGroupPython] O_element124  label="O_element : 077"  # scripted group (container) (typed FeaturePython)
  n = 6
  ref = O_element
FEATURE [App::DocumentObjectGroupPython] G4_DNA_METHYLURIDINE  # scripted group (container) (typed FeaturePython)
  Dunit = g/cm3
  Dvalue = 1
  Group = -> [H_element133,C_element143,N_element063,O_element124]
  conduct = 2
  density = 1
  expand = 3
  formula = G4_DNA_METHYLURIDINE
  name = G4_DNA_METHYLURIDINE
  specific = 4
FEATURE [App::DocumentObjectGroupPython] P_element014  label="P_element : 003"  # scripted group (container) (typed FeaturePython)
  n = 1
  ref = P_element
FEATURE [App::DocumentObjectGroupPython] O_element125  label="O_element : 078"  # scripted group (container) (typed FeaturePython)
  n = 3
  ref = O_element
FEATURE [App::DocumentObjectGroupPython] G4_DNA_MONOPHOSPHATE  # scripted group (container) (typed FeaturePython)
  Dunit = g/cm3
  Dvalue = 1
  Group = -> [P_element014,O_element125]
  conduct = 2
  density = 1
  expand = 3
  formula = G4_DNA_MONOPHOSPHATE
  name = G4_DNA_MONOPHOSPHATE
  specific = 4
FEATURE [App::DocumentObjectGroupPython] H_element134  label="H_element : 081"  # scripted group (container) (typed FeaturePython)
  n = 10
  ref = H_element
FEATURE [App::DocumentObjectGroupPython] C_element144  label="C_element : 089"  # scripted group (container) (typed FeaturePython)
  n = 10
  ref = C_element
FEATURE [App::DocumentObjectGroupPython] N_element064  label="N_element : 036"  # scripted group (container) (typed FeaturePython)
  n = 5
  ref = N_element
FEATURE [App::DocumentObjectGroupPython] O_element126  label="O_element : 079"  # scripted group (container) (typed FeaturePython)
  n = 7
  ref = O_element
FEATURE [App::DocumentObjectGroupPython] P_element015  label="P_element : 004"  # scripted group (container) (typed FeaturePython)
  n = 1
  ref = P_element
FEATURE [App::DocumentObjectGroupPython] G4_DNA_A  # scripted group (container) (typed FeaturePython)
  Dunit = g/cm3
  Dvalue = 1
  Group = -> [H_element134,C_element144,N_element064,O_element126,P_element015]
  conduct = 2
  density = 1
  expand = 3
  formula = G4_DNA_A
  name = G4_DNA_A
  specific = 4
FEATURE [App::DocumentObjectGroupPython] H_element135  label="H_element : 082"  # scripted group (container) (typed FeaturePython)
  n = 10
  ref = H_element
FEATURE [App::DocumentObjectGroupPython] C_element145  label="C_element : 090"  # scripted group (container) (typed FeaturePython)
  n = 10
  ref = C_element
FEATURE [App::DocumentObjectGroupPython] N_element065  label="N_element : 037"  # scripted group (container) (typed FeaturePython)
  n = 5
  ref = N_element
FEATURE [App::DocumentObjectGroupPython] O_element127  label="O_element : 8"  # scripted group (container) (typed FeaturePython)
  n = 8
  ref = O_element
FEATURE [App::DocumentObjectGroupPython] P_element016  label="P_element : 005"  # scripted group (container) (typed FeaturePython)
  n = 1
  ref = P_element
FEATURE [App::DocumentObjectGroupPython] G4_DNA_G  # scripted group (container) (typed FeaturePython)
  Dunit = g/cm3
  Dvalue = 1
  Group = -> [H_element135,C_element145,N_element065,O_element127,P_element016]
  conduct = 2
  density = 1
  expand = 3
  formula = G4_DNA_G
  name = G4_DNA_G
  specific = 4
FEATURE [App::DocumentObjectGroupPython] H_element136  label="H_element : 083"  # scripted group (container) (typed FeaturePython)
  n = 10
  ref = H_element
FEATURE [App::DocumentObjectGroupPython] C_element146  label="C_element : 091"  # scripted group (container) (typed FeaturePython)
  n = 9
  ref = C_element
FEATURE [App::DocumentObjectGroupPython] N_element066  label="N_element : 038"  # scripted group (container) (typed FeaturePython)
  n = 3
  ref = N_element
FEATURE [App::DocumentObjectGroupPython] O_element128  label="O_element : 080"  # scripted group (container) (typed FeaturePython)
  n = 8
  ref = O_element
FEATURE [App::DocumentObjectGroupPython] P_element017  label="P_element : 006"  # scripted group (container) (typed FeaturePython)
  n = 1
  ref = P_element
FEATURE [App::DocumentObjectGroupPython] G4_DNA_C  # scripted group (container) (typed FeaturePython)
  Dunit = g/cm3
  Dvalue = 1
  Group = -> [H_element136,C_element146,N_element066,O_element128,P_element017]
  conduct = 2
  density = 1
  expand = 3
  formula = G4_DNA_C
  name = G4_DNA_C
  specific = 4
FEATURE [App::DocumentObjectGroupPython] H_element137  label="H_element : 084"  # scripted group (container) (typed FeaturePython)
  n = 9
  ref = H_element
FEATURE [App::DocumentObjectGroupPython] C_element147  label="C_element : 092"  # scripted group (container) (typed FeaturePython)
  n = 9
  ref = C_element
FEATURE [App::DocumentObjectGroupPython] N_element067  label="N_element : 039"  # scripted group (container) (typed FeaturePython)
  n = 2
  ref = N_element
FEATURE [App::DocumentObjectGroupPython] O_element129  label="O_element : 9"  # scripted group (container) (typed FeaturePython)
  n = 9
  ref = O_element
FEATURE [App::DocumentObjectGroupPython] P_element018  label="P_element : 007"  # scripted group (container) (typed FeaturePython)
  n = 1
  ref = P_element
FEATURE [App::DocumentObjectGroupPython] G4_DNA_U  # scripted group (container) (typed FeaturePython)
  Dunit = g/cm3
  Dvalue = 1
  Group = -> [H_element137,C_element147,N_element067,O_element129,P_element018]
  conduct = 2
  density = 1
  expand = 3
  formula = G4_DNA_U
  name = G4_DNA_U
  specific = 4
FEATURE [App::DocumentObjectGroupPython] H_element138  label="H_element : 085"  # scripted group (container) (typed FeaturePython)
  n = 11
  ref = H_element
FEATURE [App::DocumentObjectGroupPython] C_element148  label="C_element : 093"  # scripted group (container) (typed FeaturePython)
  n = 10
  ref = C_element
FEATURE [App::DocumentObjectGroupPython] N_element068  label="N_element : 040"  # scripted group (container) (typed FeaturePython)
  n = 2
  ref = N_element
FEATURE [App::DocumentObjectGroupPython] O_element130  label="O_element : 081"  # scripted group (container) (typed FeaturePython)
  n = 9
  ref = O_element
FEATURE [App::DocumentObjectGroupPython] P_element019  label="P_element : 008"  # scripted group (container) (typed FeaturePython)
  n = 1
  ref = P_element
FEATURE [App::DocumentObjectGroupPython] G4_DNA_MU  # scripted group (container) (typed FeaturePython)
  Dunit = g/cm3
  Dvalue = 1
  Group = -> [H_element138,C_element148,N_element068,O_element130,P_element019]
  conduct = 2
  density = 1
  expand = 3
  formula = G4_DNA_MU
  name = G4_DNA_MU
  specific = 4
FEATURE [App::DocumentObjectGroupPython] BioChemical  # scripted group (container) (typed FeaturePython)
  Group = -> [G4_CYTOSINE,G4_THYMINE,G4_URACIL,G4_DNA_ADENINE,G4_DNA_GUANINE,G4_DNA_CYTOSINE,G4_DNA_THYMINE,G4_DNA_URACIL,G4_DNA_ADENOSINE,G4_DNA_GUANOSINE,G4_DNA_CYTIDINE,G4_DNA_URIDINE,G4_DNA_METHYLURIDINE,G4_DNA_MONOPHOSPHATE,G4_DNA_A,G4_DNA_G,G4_DNA_C,G4_DNA_U,G4_DNA_MU]
FEATURE [App::DocumentObjectGroupPython] G4Materials  # scripted group (container) (typed FeaturePython)
  Group = -> [NIST,Element,HEP,Space,BioChemical]
  version = 1
FEATURE [App::DocumentObjectGroupPython] Geant4  # scripted group (container) (typed FeaturePython)
  Group = -> [G4Isotopes,G4Elements,G4Materials]
FEATURE [App::DocumentObjectGroupPython] Materials  # scripted group (container) (typed FeaturePython)
  Group = -> [Geant4]
FEATURE [Part::FeaturePython] GDMLBox_WorldBox  # WARN: FeaturePython — macro-defined, semantics opaque (R4)
  lunit = 2
  material = 5
  x = 100
  y = 100
  z = 100
FEATURE [Part::FeaturePython] GDMLBox_Box  # WARN: FeaturePython — macro-defined, semantics opaque (R4)
  lunit = 2
  material = 0
  x = 5
  y = 5
  z = 5
FEATURE [App::Part] LV_Box
  Group = -> [GDMLBox_Box]
  Origin = -> Origin001
  Placement = pos=(10,0,0) rot=(0,0,1;0rad)
FEATURE [Part::FeaturePython] Array  # Draft array (typed FeaturePython)
  Angle = 360
  ArrayType = 1
  Axis = (0,0,1)
  Base = -> LV_Box
  Center = (0,0,0)
  Fuse = false
  IntervalAxis = (0,0,0)
  IntervalX = (50,0,0)
  IntervalY = (0,50,0)
  IntervalZ = (0,0,50)
  NumberCircles = 3
  NumberPolar = 5
  NumberX = 2
  NumberY = 2
  NumberZ = 1
  RadialDistance = 50
  Symmetry = 1
  TangentialDistance = 25
FEATURE [Part::FeaturePython] Array001  # Draft array (typed FeaturePython)
  Angle = 360
  ArrayType = 0
  Axis = (0,0,1)
  Base = -> Array
  Center = (0,0,0)
  Fuse = false
  IntervalAxis = (0,0,0)
  IntervalX = (50,0,0)
  IntervalY = (0,30,0)
  IntervalZ = (0,0,100)
  NumberCircles = 3
  NumberPolar = 5
  NumberX = 2
  NumberY = 2
  NumberZ = 1
  Placement = pos=(-20,-14,0) rot=(0,0,1;0rad)
  RadialDistance = 50
  Symmetry = 1
  TangentialDistance = 25
FEATURE [App::Part] Part
  Group = -> [LV_Box,Array,Array001]
  Origin = -> Origin002
FEATURE [App::Part] worldVOL
  Group = -> [GDMLBox_WorldBox,Part]
  Origin = -> Origin
